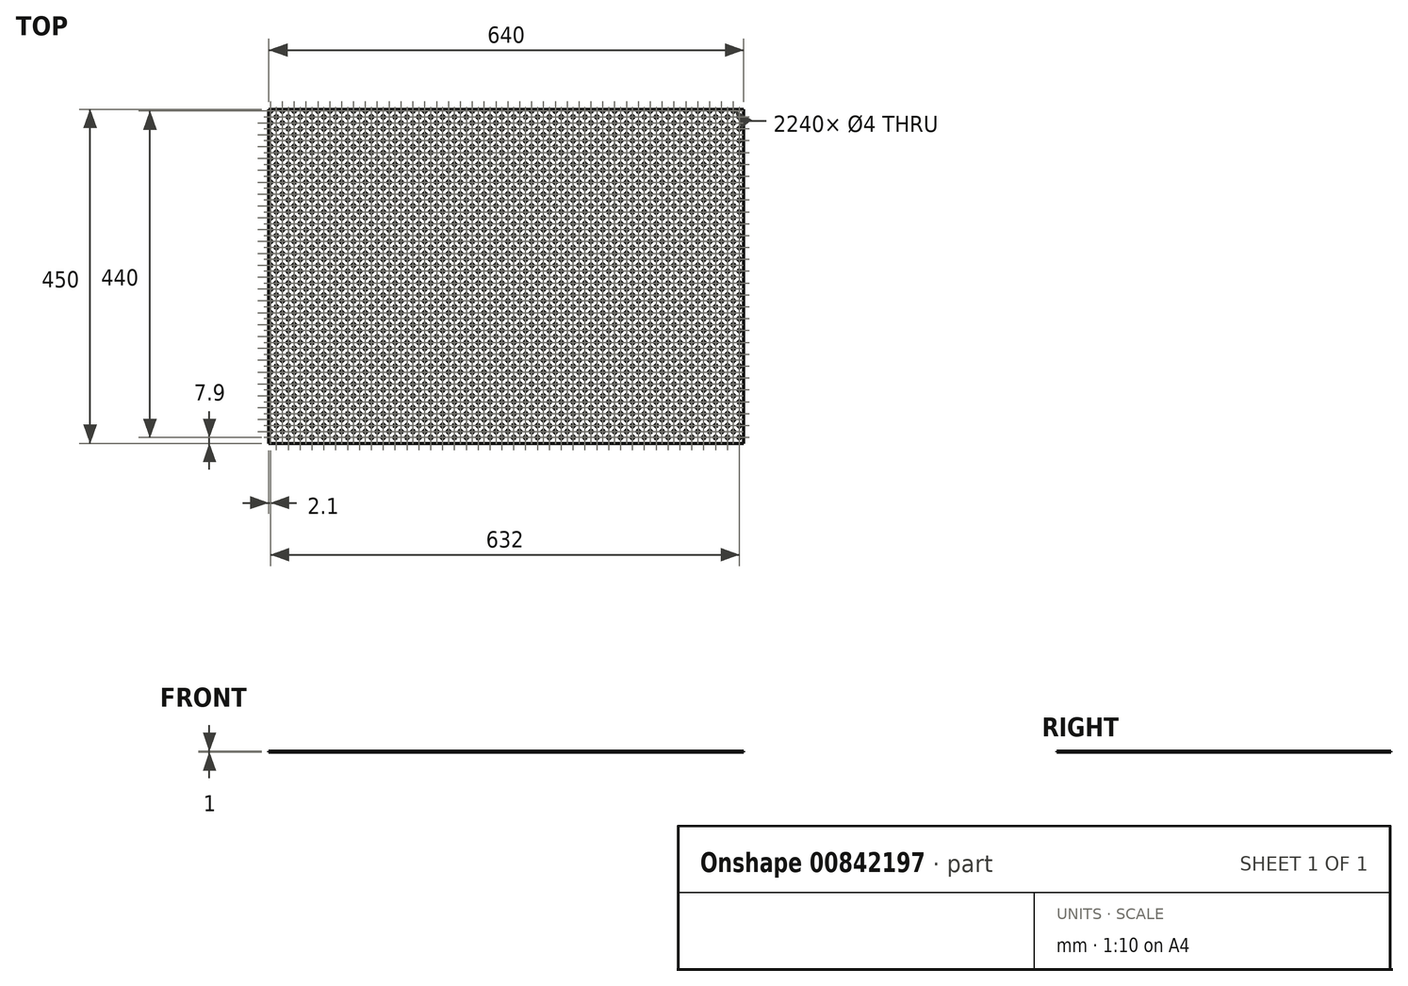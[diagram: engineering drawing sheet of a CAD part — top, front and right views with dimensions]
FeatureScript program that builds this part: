
annotation { "Feature Type Name" : "Feature", "Feature Type Description" : "" }
export const myFeature = defineFeature(function(context is Context, id is Id, definition is map)
    precondition{}
    {
        {
            var Q0;
            Q0=qCreatedBy(makeId("Top.planeOp"),FACE);
            var sketch = newSketch(context, id + "F0", { "sketchPlane" : qUnion([Q0])});
            skLineSegment(sketch, "E0.bottom", {"start": v(-115.44, 0) * mm, "end": v(524.56, 0) * mm});
            skLineSegment(sketch, "E0.top", {"start": v(-115.44, -450) * mm, "end": v(524.56, -450) * mm});
            skLineSegment(sketch, "E0.left", {"start": v(-115.44, 0) * mm, "end": v(-115.44, -450) * mm});
            skLineSegment(sketch, "E0.right", {"start": v(524.56, 0) * mm, "end": v(524.56, -450) * mm});
            skCircle(sketch, "E1", {"center": v(-113.34, -2.1) * mm, "radius": 2 * mm});
            skCircle(sketch, "E2.0.1.0", {"center": v(-113.34, -18.1) * mm, "radius": 2 * mm});
            skCircle(sketch, "E2.0.2.0", {"center": v(-113.34, -34.1) * mm, "radius": 2 * mm});
            skCircle(sketch, "E2.0.3.0", {"center": v(-113.34, -50.1) * mm, "radius": 2 * mm});
            skCircle(sketch, "E2.0.4.0", {"center": v(-113.34, -66.1) * mm, "radius": 2 * mm});
            skCircle(sketch, "E2.0.5.0", {"center": v(-113.34, -82.1) * mm, "radius": 2 * mm});
            skCircle(sketch, "E2.0.6.0", {"center": v(-113.34, -98.1) * mm, "radius": 2 * mm});
            skCircle(sketch, "E2.0.7.0", {"center": v(-113.34, -114.1) * mm, "radius": 2 * mm});
            skCircle(sketch, "E2.0.8.0", {"center": v(-113.34, -130.1) * mm, "radius": 2 * mm});
            skCircle(sketch, "E2.0.9.0", {"center": v(-113.34, -146.1) * mm, "radius": 2 * mm});
            skCircle(sketch, "E2.0.10.0", {"center": v(-113.34, -162.1) * mm, "radius": 2 * mm});
            skCircle(sketch, "E2.0.11.0", {"center": v(-113.34, -178.1) * mm, "radius": 2 * mm});
            skCircle(sketch, "E2.0.12.0", {"center": v(-113.34, -194.1) * mm, "radius": 2 * mm});
            skCircle(sketch, "E2.0.13.0", {"center": v(-113.34, -210.1) * mm, "radius": 2 * mm});
            skCircle(sketch, "E2.0.14.0", {"center": v(-113.34, -226.1) * mm, "radius": 2 * mm});
            skCircle(sketch, "E2.0.15.0", {"center": v(-113.34, -242.1) * mm, "radius": 2 * mm});
            skCircle(sketch, "E2.0.16.0", {"center": v(-113.34, -258.1) * mm, "radius": 2 * mm});
            skCircle(sketch, "E2.0.17.0", {"center": v(-113.34, -274.1) * mm, "radius": 2 * mm});
            skCircle(sketch, "E2.0.18.0", {"center": v(-113.34, -290.1) * mm, "radius": 2 * mm});
            skCircle(sketch, "E2.0.19.0", {"center": v(-113.34, -306.1) * mm, "radius": 2 * mm});
            skCircle(sketch, "E2.0.20.0", {"center": v(-113.34, -322.1) * mm, "radius": 2 * mm});
            skCircle(sketch, "E2.0.21.0", {"center": v(-113.34, -338.1) * mm, "radius": 2 * mm});
            skCircle(sketch, "E2.0.22.0", {"center": v(-113.34, -354.1) * mm, "radius": 2 * mm});
            skCircle(sketch, "E2.0.23.0", {"center": v(-113.34, -370.1) * mm, "radius": 2 * mm});
            skCircle(sketch, "E2.0.24.0", {"center": v(-113.34, -386.1) * mm, "radius": 2 * mm});
            skCircle(sketch, "E2.0.25.0", {"center": v(-113.34, -402.1) * mm, "radius": 2 * mm});
            skCircle(sketch, "E2.0.26.0", {"center": v(-113.34, -418.1) * mm, "radius": 2 * mm});
            skCircle(sketch, "E2.0.27.0", {"center": v(-113.34, -434.1) * mm, "radius": 2 * mm});
            skCircle(sketch, "E2.1.0.0", {"center": v(-97.34, -2.1) * mm, "radius": 2 * mm});
            skCircle(sketch, "E2.1.1.0", {"center": v(-97.34, -18.1) * mm, "radius": 2 * mm});
            skCircle(sketch, "E2.1.2.0", {"center": v(-97.34, -34.1) * mm, "radius": 2 * mm});
            skCircle(sketch, "E2.1.3.0", {"center": v(-97.34, -50.1) * mm, "radius": 2 * mm});
            skCircle(sketch, "E2.1.4.0", {"center": v(-97.34, -66.1) * mm, "radius": 2 * mm});
            skCircle(sketch, "E2.1.5.0", {"center": v(-97.34, -82.1) * mm, "radius": 2 * mm});
            skCircle(sketch, "E2.1.6.0", {"center": v(-97.34, -98.1) * mm, "radius": 2 * mm});
            skCircle(sketch, "E2.1.7.0", {"center": v(-97.34, -114.1) * mm, "radius": 2 * mm});
            skCircle(sketch, "E2.1.8.0", {"center": v(-97.34, -130.1) * mm, "radius": 2 * mm});
            skCircle(sketch, "E2.1.9.0", {"center": v(-97.34, -146.1) * mm, "radius": 2 * mm});
            skCircle(sketch, "E2.1.10.0", {"center": v(-97.34, -162.1) * mm, "radius": 2 * mm});
            skCircle(sketch, "E2.1.11.0", {"center": v(-97.34, -178.1) * mm, "radius": 2 * mm});
            skCircle(sketch, "E2.1.12.0", {"center": v(-97.34, -194.1) * mm, "radius": 2 * mm});
            skCircle(sketch, "E2.1.13.0", {"center": v(-97.34, -210.1) * mm, "radius": 2 * mm});
            skCircle(sketch, "E2.1.14.0", {"center": v(-97.34, -226.1) * mm, "radius": 2 * mm});
            skCircle(sketch, "E2.1.15.0", {"center": v(-97.34, -242.1) * mm, "radius": 2 * mm});
            skCircle(sketch, "E2.1.16.0", {"center": v(-97.34, -258.1) * mm, "radius": 2 * mm});
            skCircle(sketch, "E2.1.17.0", {"center": v(-97.34, -274.1) * mm, "radius": 2 * mm});
            skCircle(sketch, "E2.1.18.0", {"center": v(-97.34, -290.1) * mm, "radius": 2 * mm});
            skCircle(sketch, "E2.1.19.0", {"center": v(-97.34, -306.1) * mm, "radius": 2 * mm});
            skCircle(sketch, "E2.1.20.0", {"center": v(-97.34, -322.1) * mm, "radius": 2 * mm});
            skCircle(sketch, "E2.1.21.0", {"center": v(-97.34, -338.1) * mm, "radius": 2 * mm});
            skCircle(sketch, "E2.1.22.0", {"center": v(-97.34, -354.1) * mm, "radius": 2 * mm});
            skCircle(sketch, "E2.1.23.0", {"center": v(-97.34, -370.1) * mm, "radius": 2 * mm});
            skCircle(sketch, "E2.1.24.0", {"center": v(-97.34, -386.1) * mm, "radius": 2 * mm});
            skCircle(sketch, "E2.1.25.0", {"center": v(-97.34, -402.1) * mm, "radius": 2 * mm});
            skCircle(sketch, "E2.1.26.0", {"center": v(-97.34, -418.1) * mm, "radius": 2 * mm});
            skCircle(sketch, "E2.1.27.0", {"center": v(-97.34, -434.1) * mm, "radius": 2 * mm});
            skCircle(sketch, "E2.2.0.0", {"center": v(-81.34, -2.1) * mm, "radius": 2 * mm});
            skCircle(sketch, "E2.2.1.0", {"center": v(-81.34, -18.1) * mm, "radius": 2 * mm});
            skCircle(sketch, "E2.2.2.0", {"center": v(-81.34, -34.1) * mm, "radius": 2 * mm});
            skCircle(sketch, "E2.2.3.0", {"center": v(-81.34, -50.1) * mm, "radius": 2 * mm});
            skCircle(sketch, "E2.2.4.0", {"center": v(-81.34, -66.1) * mm, "radius": 2 * mm});
            skCircle(sketch, "E2.2.5.0", {"center": v(-81.34, -82.1) * mm, "radius": 2 * mm});
            skCircle(sketch, "E2.2.6.0", {"center": v(-81.34, -98.1) * mm, "radius": 2 * mm});
            skCircle(sketch, "E2.2.7.0", {"center": v(-81.34, -114.1) * mm, "radius": 2 * mm});
            skCircle(sketch, "E2.2.8.0", {"center": v(-81.34, -130.1) * mm, "radius": 2 * mm});
            skCircle(sketch, "E2.2.9.0", {"center": v(-81.34, -146.1) * mm, "radius": 2 * mm});
            skCircle(sketch, "E2.2.10.0", {"center": v(-81.34, -162.1) * mm, "radius": 2 * mm});
            skCircle(sketch, "E2.2.11.0", {"center": v(-81.34, -178.1) * mm, "radius": 2 * mm});
            skCircle(sketch, "E2.2.12.0", {"center": v(-81.34, -194.1) * mm, "radius": 2 * mm});
            skCircle(sketch, "E2.2.13.0", {"center": v(-81.34, -210.1) * mm, "radius": 2 * mm});
            skCircle(sketch, "E2.2.14.0", {"center": v(-81.34, -226.1) * mm, "radius": 2 * mm});
            skCircle(sketch, "E2.2.15.0", {"center": v(-81.34, -242.1) * mm, "radius": 2 * mm});
            skCircle(sketch, "E2.2.16.0", {"center": v(-81.34, -258.1) * mm, "radius": 2 * mm});
            skCircle(sketch, "E2.2.17.0", {"center": v(-81.34, -274.1) * mm, "radius": 2 * mm});
            skCircle(sketch, "E2.2.18.0", {"center": v(-81.34, -290.1) * mm, "radius": 2 * mm});
            skCircle(sketch, "E2.2.19.0", {"center": v(-81.34, -306.1) * mm, "radius": 2 * mm});
            skCircle(sketch, "E2.2.20.0", {"center": v(-81.34, -322.1) * mm, "radius": 2 * mm});
            skCircle(sketch, "E2.2.21.0", {"center": v(-81.34, -338.1) * mm, "radius": 2 * mm});
            skCircle(sketch, "E2.2.22.0", {"center": v(-81.34, -354.1) * mm, "radius": 2 * mm});
            skCircle(sketch, "E2.2.23.0", {"center": v(-81.34, -370.1) * mm, "radius": 2 * mm});
            skCircle(sketch, "E2.2.24.0", {"center": v(-81.34, -386.1) * mm, "radius": 2 * mm});
            skCircle(sketch, "E2.2.25.0", {"center": v(-81.34, -402.1) * mm, "radius": 2 * mm});
            skCircle(sketch, "E2.2.26.0", {"center": v(-81.34, -418.1) * mm, "radius": 2 * mm});
            skCircle(sketch, "E2.2.27.0", {"center": v(-81.34, -434.1) * mm, "radius": 2 * mm});
            skCircle(sketch, "E2.3.0.0", {"center": v(-65.34, -2.1) * mm, "radius": 2 * mm});
            skCircle(sketch, "E2.3.1.0", {"center": v(-65.34, -18.1) * mm, "radius": 2 * mm});
            skCircle(sketch, "E2.3.2.0", {"center": v(-65.34, -34.1) * mm, "radius": 2 * mm});
            skCircle(sketch, "E2.3.3.0", {"center": v(-65.34, -50.1) * mm, "radius": 2 * mm});
            skCircle(sketch, "E2.3.4.0", {"center": v(-65.34, -66.1) * mm, "radius": 2 * mm});
            skCircle(sketch, "E2.3.5.0", {"center": v(-65.34, -82.1) * mm, "radius": 2 * mm});
            skCircle(sketch, "E2.3.6.0", {"center": v(-65.34, -98.1) * mm, "radius": 2 * mm});
            skCircle(sketch, "E2.3.7.0", {"center": v(-65.34, -114.1) * mm, "radius": 2 * mm});
            skCircle(sketch, "E2.3.8.0", {"center": v(-65.34, -130.1) * mm, "radius": 2 * mm});
            skCircle(sketch, "E2.3.9.0", {"center": v(-65.34, -146.1) * mm, "radius": 2 * mm});
            skCircle(sketch, "E2.3.10.0", {"center": v(-65.34, -162.1) * mm, "radius": 2 * mm});
            skCircle(sketch, "E2.3.11.0", {"center": v(-65.34, -178.1) * mm, "radius": 2 * mm});
            skCircle(sketch, "E2.3.12.0", {"center": v(-65.34, -194.1) * mm, "radius": 2 * mm});
            skCircle(sketch, "E2.3.13.0", {"center": v(-65.34, -210.1) * mm, "radius": 2 * mm});
            skCircle(sketch, "E2.3.14.0", {"center": v(-65.34, -226.1) * mm, "radius": 2 * mm});
            skCircle(sketch, "E2.3.15.0", {"center": v(-65.34, -242.1) * mm, "radius": 2 * mm});
            skCircle(sketch, "E2.3.16.0", {"center": v(-65.34, -258.1) * mm, "radius": 2 * mm});
            skCircle(sketch, "E2.3.17.0", {"center": v(-65.34, -274.1) * mm, "radius": 2 * mm});
            skCircle(sketch, "E2.3.18.0", {"center": v(-65.34, -290.1) * mm, "radius": 2 * mm});
            skCircle(sketch, "E2.3.19.0", {"center": v(-65.34, -306.1) * mm, "radius": 2 * mm});
            skCircle(sketch, "E2.3.20.0", {"center": v(-65.34, -322.1) * mm, "radius": 2 * mm});
            skCircle(sketch, "E2.3.21.0", {"center": v(-65.34, -338.1) * mm, "radius": 2 * mm});
            skCircle(sketch, "E2.3.22.0", {"center": v(-65.34, -354.1) * mm, "radius": 2 * mm});
            skCircle(sketch, "E2.3.23.0", {"center": v(-65.34, -370.1) * mm, "radius": 2 * mm});
            skCircle(sketch, "E2.3.24.0", {"center": v(-65.34, -386.1) * mm, "radius": 2 * mm});
            skCircle(sketch, "E2.3.25.0", {"center": v(-65.34, -402.1) * mm, "radius": 2 * mm});
            skCircle(sketch, "E2.3.26.0", {"center": v(-65.34, -418.1) * mm, "radius": 2 * mm});
            skCircle(sketch, "E2.3.27.0", {"center": v(-65.34, -434.1) * mm, "radius": 2 * mm});
            skCircle(sketch, "E2.4.0.0", {"center": v(-49.34, -2.1) * mm, "radius": 2 * mm});
            skCircle(sketch, "E2.4.1.0", {"center": v(-49.34, -18.1) * mm, "radius": 2 * mm});
            skCircle(sketch, "E2.4.2.0", {"center": v(-49.34, -34.1) * mm, "radius": 2 * mm});
            skCircle(sketch, "E2.4.3.0", {"center": v(-49.34, -50.1) * mm, "radius": 2 * mm});
            skCircle(sketch, "E2.4.4.0", {"center": v(-49.34, -66.1) * mm, "radius": 2 * mm});
            skCircle(sketch, "E2.4.5.0", {"center": v(-49.34, -82.1) * mm, "radius": 2 * mm});
            skCircle(sketch, "E2.4.6.0", {"center": v(-49.34, -98.1) * mm, "radius": 2 * mm});
            skCircle(sketch, "E2.4.7.0", {"center": v(-49.34, -114.1) * mm, "radius": 2 * mm});
            skCircle(sketch, "E2.4.8.0", {"center": v(-49.34, -130.1) * mm, "radius": 2 * mm});
            skCircle(sketch, "E2.4.9.0", {"center": v(-49.34, -146.1) * mm, "radius": 2 * mm});
            skCircle(sketch, "E2.4.10.0", {"center": v(-49.34, -162.1) * mm, "radius": 2 * mm});
            skCircle(sketch, "E2.4.11.0", {"center": v(-49.34, -178.1) * mm, "radius": 2 * mm});
            skCircle(sketch, "E2.4.12.0", {"center": v(-49.34, -194.1) * mm, "radius": 2 * mm});
            skCircle(sketch, "E2.4.13.0", {"center": v(-49.34, -210.1) * mm, "radius": 2 * mm});
            skCircle(sketch, "E2.4.14.0", {"center": v(-49.34, -226.1) * mm, "radius": 2 * mm});
            skCircle(sketch, "E2.4.15.0", {"center": v(-49.34, -242.1) * mm, "radius": 2 * mm});
            skCircle(sketch, "E2.4.16.0", {"center": v(-49.34, -258.1) * mm, "radius": 2 * mm});
            skCircle(sketch, "E2.4.17.0", {"center": v(-49.34, -274.1) * mm, "radius": 2 * mm});
            skCircle(sketch, "E2.4.18.0", {"center": v(-49.34, -290.1) * mm, "radius": 2 * mm});
            skCircle(sketch, "E2.4.19.0", {"center": v(-49.34, -306.1) * mm, "radius": 2 * mm});
            skCircle(sketch, "E2.4.20.0", {"center": v(-49.34, -322.1) * mm, "radius": 2 * mm});
            skCircle(sketch, "E2.4.21.0", {"center": v(-49.34, -338.1) * mm, "radius": 2 * mm});
            skCircle(sketch, "E2.4.22.0", {"center": v(-49.34, -354.1) * mm, "radius": 2 * mm});
            skCircle(sketch, "E2.4.23.0", {"center": v(-49.34, -370.1) * mm, "radius": 2 * mm});
            skCircle(sketch, "E2.4.24.0", {"center": v(-49.34, -386.1) * mm, "radius": 2 * mm});
            skCircle(sketch, "E2.4.25.0", {"center": v(-49.34, -402.1) * mm, "radius": 2 * mm});
            skCircle(sketch, "E2.4.26.0", {"center": v(-49.34, -418.1) * mm, "radius": 2 * mm});
            skCircle(sketch, "E2.4.27.0", {"center": v(-49.34, -434.1) * mm, "radius": 2 * mm});
            skCircle(sketch, "E2.5.0.0", {"center": v(-33.34, -2.1) * mm, "radius": 2 * mm});
            skCircle(sketch, "E2.5.1.0", {"center": v(-33.34, -18.1) * mm, "radius": 2 * mm});
            skCircle(sketch, "E2.5.2.0", {"center": v(-33.34, -34.1) * mm, "radius": 2 * mm});
            skCircle(sketch, "E2.5.3.0", {"center": v(-33.34, -50.1) * mm, "radius": 2 * mm});
            skCircle(sketch, "E2.5.4.0", {"center": v(-33.34, -66.1) * mm, "radius": 2 * mm});
            skCircle(sketch, "E2.5.5.0", {"center": v(-33.34, -82.1) * mm, "radius": 2 * mm});
            skCircle(sketch, "E2.5.6.0", {"center": v(-33.34, -98.1) * mm, "radius": 2 * mm});
            skCircle(sketch, "E2.5.7.0", {"center": v(-33.34, -114.1) * mm, "radius": 2 * mm});
            skCircle(sketch, "E2.5.8.0", {"center": v(-33.34, -130.1) * mm, "radius": 2 * mm});
            skCircle(sketch, "E2.5.9.0", {"center": v(-33.34, -146.1) * mm, "radius": 2 * mm});
            skCircle(sketch, "E2.5.10.0", {"center": v(-33.34, -162.1) * mm, "radius": 2 * mm});
            skCircle(sketch, "E2.5.11.0", {"center": v(-33.34, -178.1) * mm, "radius": 2 * mm});
            skCircle(sketch, "E2.5.12.0", {"center": v(-33.34, -194.1) * mm, "radius": 2 * mm});
            skCircle(sketch, "E2.5.13.0", {"center": v(-33.34, -210.1) * mm, "radius": 2 * mm});
            skCircle(sketch, "E2.5.14.0", {"center": v(-33.34, -226.1) * mm, "radius": 2 * mm});
            skCircle(sketch, "E2.5.15.0", {"center": v(-33.34, -242.1) * mm, "radius": 2 * mm});
            skCircle(sketch, "E2.5.16.0", {"center": v(-33.34, -258.1) * mm, "radius": 2 * mm});
            skCircle(sketch, "E2.5.17.0", {"center": v(-33.34, -274.1) * mm, "radius": 2 * mm});
            skCircle(sketch, "E2.5.18.0", {"center": v(-33.34, -290.1) * mm, "radius": 2 * mm});
            skCircle(sketch, "E2.5.19.0", {"center": v(-33.34, -306.1) * mm, "radius": 2 * mm});
            skCircle(sketch, "E2.5.20.0", {"center": v(-33.34, -322.1) * mm, "radius": 2 * mm});
            skCircle(sketch, "E2.5.21.0", {"center": v(-33.34, -338.1) * mm, "radius": 2 * mm});
            skCircle(sketch, "E2.5.22.0", {"center": v(-33.34, -354.1) * mm, "radius": 2 * mm});
            skCircle(sketch, "E2.5.23.0", {"center": v(-33.34, -370.1) * mm, "radius": 2 * mm});
            skCircle(sketch, "E2.5.24.0", {"center": v(-33.34, -386.1) * mm, "radius": 2 * mm});
            skCircle(sketch, "E2.5.25.0", {"center": v(-33.34, -402.1) * mm, "radius": 2 * mm});
            skCircle(sketch, "E2.5.26.0", {"center": v(-33.34, -418.1) * mm, "radius": 2 * mm});
            skCircle(sketch, "E2.5.27.0", {"center": v(-33.34, -434.1) * mm, "radius": 2 * mm});
            skCircle(sketch, "E2.6.0.0", {"center": v(-17.34, -2.1) * mm, "radius": 2 * mm});
            skCircle(sketch, "E2.6.1.0", {"center": v(-17.34, -18.1) * mm, "radius": 2 * mm});
            skCircle(sketch, "E2.6.2.0", {"center": v(-17.34, -34.1) * mm, "radius": 2 * mm});
            skCircle(sketch, "E2.6.3.0", {"center": v(-17.34, -50.1) * mm, "radius": 2 * mm});
            skCircle(sketch, "E2.6.4.0", {"center": v(-17.34, -66.1) * mm, "radius": 2 * mm});
            skCircle(sketch, "E2.6.5.0", {"center": v(-17.34, -82.1) * mm, "radius": 2 * mm});
            skCircle(sketch, "E2.6.6.0", {"center": v(-17.34, -98.1) * mm, "radius": 2 * mm});
            skCircle(sketch, "E2.6.7.0", {"center": v(-17.34, -114.1) * mm, "radius": 2 * mm});
            skCircle(sketch, "E2.6.8.0", {"center": v(-17.34, -130.1) * mm, "radius": 2 * mm});
            skCircle(sketch, "E2.6.9.0", {"center": v(-17.34, -146.1) * mm, "radius": 2 * mm});
            skCircle(sketch, "E2.6.10.0", {"center": v(-17.34, -162.1) * mm, "radius": 2 * mm});
            skCircle(sketch, "E2.6.11.0", {"center": v(-17.34, -178.1) * mm, "radius": 2 * mm});
            skCircle(sketch, "E2.6.12.0", {"center": v(-17.34, -194.1) * mm, "radius": 2 * mm});
            skCircle(sketch, "E2.6.13.0", {"center": v(-17.34, -210.1) * mm, "radius": 2 * mm});
            skCircle(sketch, "E2.6.14.0", {"center": v(-17.34, -226.1) * mm, "radius": 2 * mm});
            skCircle(sketch, "E2.6.15.0", {"center": v(-17.34, -242.1) * mm, "radius": 2 * mm});
            skCircle(sketch, "E2.6.16.0", {"center": v(-17.34, -258.1) * mm, "radius": 2 * mm});
            skCircle(sketch, "E2.6.17.0", {"center": v(-17.34, -274.1) * mm, "radius": 2 * mm});
            skCircle(sketch, "E2.6.18.0", {"center": v(-17.34, -290.1) * mm, "radius": 2 * mm});
            skCircle(sketch, "E2.6.19.0", {"center": v(-17.34, -306.1) * mm, "radius": 2 * mm});
            skCircle(sketch, "E2.6.20.0", {"center": v(-17.34, -322.1) * mm, "radius": 2 * mm});
            skCircle(sketch, "E2.6.21.0", {"center": v(-17.34, -338.1) * mm, "radius": 2 * mm});
            skCircle(sketch, "E2.6.22.0", {"center": v(-17.34, -354.1) * mm, "radius": 2 * mm});
            skCircle(sketch, "E2.6.23.0", {"center": v(-17.34, -370.1) * mm, "radius": 2 * mm});
            skCircle(sketch, "E2.6.24.0", {"center": v(-17.34, -386.1) * mm, "radius": 2 * mm});
            skCircle(sketch, "E2.6.25.0", {"center": v(-17.34, -402.1) * mm, "radius": 2 * mm});
            skCircle(sketch, "E2.6.26.0", {"center": v(-17.34, -418.1) * mm, "radius": 2 * mm});
            skCircle(sketch, "E2.6.27.0", {"center": v(-17.34, -434.1) * mm, "radius": 2 * mm});
            skCircle(sketch, "E2.7.0.0", {"center": v(-1.34, -2.1) * mm, "radius": 2 * mm});
            skCircle(sketch, "E2.7.1.0", {"center": v(-1.34, -18.1) * mm, "radius": 2 * mm});
            skCircle(sketch, "E2.7.2.0", {"center": v(-1.34, -34.1) * mm, "radius": 2 * mm});
            skCircle(sketch, "E2.7.3.0", {"center": v(-1.34, -50.1) * mm, "radius": 2 * mm});
            skCircle(sketch, "E2.7.4.0", {"center": v(-1.34, -66.1) * mm, "radius": 2 * mm});
            skCircle(sketch, "E2.7.5.0", {"center": v(-1.34, -82.1) * mm, "radius": 2 * mm});
            skCircle(sketch, "E2.7.6.0", {"center": v(-1.34, -98.1) * mm, "radius": 2 * mm});
            skCircle(sketch, "E2.7.7.0", {"center": v(-1.34, -114.1) * mm, "radius": 2 * mm});
            skCircle(sketch, "E2.7.8.0", {"center": v(-1.34, -130.1) * mm, "radius": 2 * mm});
            skCircle(sketch, "E2.7.9.0", {"center": v(-1.34, -146.1) * mm, "radius": 2 * mm});
            skCircle(sketch, "E2.7.10.0", {"center": v(-1.34, -162.1) * mm, "radius": 2 * mm});
            skCircle(sketch, "E2.7.11.0", {"center": v(-1.34, -178.1) * mm, "radius": 2 * mm});
            skCircle(sketch, "E2.7.12.0", {"center": v(-1.34, -194.1) * mm, "radius": 2 * mm});
            skCircle(sketch, "E2.7.13.0", {"center": v(-1.34, -210.1) * mm, "radius": 2 * mm});
            skCircle(sketch, "E2.7.14.0", {"center": v(-1.34, -226.1) * mm, "radius": 2 * mm});
            skCircle(sketch, "E2.7.15.0", {"center": v(-1.34, -242.1) * mm, "radius": 2 * mm});
            skCircle(sketch, "E2.7.16.0", {"center": v(-1.34, -258.1) * mm, "radius": 2 * mm});
            skCircle(sketch, "E2.7.17.0", {"center": v(-1.34, -274.1) * mm, "radius": 2 * mm});
            skCircle(sketch, "E2.7.18.0", {"center": v(-1.34, -290.1) * mm, "radius": 2 * mm});
            skCircle(sketch, "E2.7.19.0", {"center": v(-1.34, -306.1) * mm, "radius": 2 * mm});
            skCircle(sketch, "E2.7.20.0", {"center": v(-1.34, -322.1) * mm, "radius": 2 * mm});
            skCircle(sketch, "E2.7.21.0", {"center": v(-1.34, -338.1) * mm, "radius": 2 * mm});
            skCircle(sketch, "E2.7.22.0", {"center": v(-1.34, -354.1) * mm, "radius": 2 * mm});
            skCircle(sketch, "E2.7.23.0", {"center": v(-1.34, -370.1) * mm, "radius": 2 * mm});
            skCircle(sketch, "E2.7.24.0", {"center": v(-1.34, -386.1) * mm, "radius": 2 * mm});
            skCircle(sketch, "E2.7.25.0", {"center": v(-1.34, -402.1) * mm, "radius": 2 * mm});
            skCircle(sketch, "E2.7.26.0", {"center": v(-1.34, -418.1) * mm, "radius": 2 * mm});
            skCircle(sketch, "E2.7.27.0", {"center": v(-1.34, -434.1) * mm, "radius": 2 * mm});
            skCircle(sketch, "E2.8.0.0", {"center": v(14.66, -2.1) * mm, "radius": 2 * mm});
            skCircle(sketch, "E2.8.1.0", {"center": v(14.66, -18.1) * mm, "radius": 2 * mm});
            skCircle(sketch, "E2.8.2.0", {"center": v(14.66, -34.1) * mm, "radius": 2 * mm});
            skCircle(sketch, "E2.8.3.0", {"center": v(14.66, -50.1) * mm, "radius": 2 * mm});
            skCircle(sketch, "E2.8.4.0", {"center": v(14.66, -66.1) * mm, "radius": 2 * mm});
            skCircle(sketch, "E2.8.5.0", {"center": v(14.66, -82.1) * mm, "radius": 2 * mm});
            skCircle(sketch, "E2.8.6.0", {"center": v(14.66, -98.1) * mm, "radius": 2 * mm});
            skCircle(sketch, "E2.8.7.0", {"center": v(14.66, -114.1) * mm, "radius": 2 * mm});
            skCircle(sketch, "E2.8.8.0", {"center": v(14.66, -130.1) * mm, "radius": 2 * mm});
            skCircle(sketch, "E2.8.9.0", {"center": v(14.66, -146.1) * mm, "radius": 2 * mm});
            skCircle(sketch, "E2.8.10.0", {"center": v(14.66, -162.1) * mm, "radius": 2 * mm});
            skCircle(sketch, "E2.8.11.0", {"center": v(14.66, -178.1) * mm, "radius": 2 * mm});
            skCircle(sketch, "E2.8.12.0", {"center": v(14.66, -194.1) * mm, "radius": 2 * mm});
            skCircle(sketch, "E2.8.13.0", {"center": v(14.66, -210.1) * mm, "radius": 2 * mm});
            skCircle(sketch, "E2.8.14.0", {"center": v(14.66, -226.1) * mm, "radius": 2 * mm});
            skCircle(sketch, "E2.8.15.0", {"center": v(14.66, -242.1) * mm, "radius": 2 * mm});
            skCircle(sketch, "E2.8.16.0", {"center": v(14.66, -258.1) * mm, "radius": 2 * mm});
            skCircle(sketch, "E2.8.17.0", {"center": v(14.66, -274.1) * mm, "radius": 2 * mm});
            skCircle(sketch, "E2.8.18.0", {"center": v(14.66, -290.1) * mm, "radius": 2 * mm});
            skCircle(sketch, "E2.8.19.0", {"center": v(14.66, -306.1) * mm, "radius": 2 * mm});
            skCircle(sketch, "E2.8.20.0", {"center": v(14.66, -322.1) * mm, "radius": 2 * mm});
            skCircle(sketch, "E2.8.21.0", {"center": v(14.66, -338.1) * mm, "radius": 2 * mm});
            skCircle(sketch, "E2.8.22.0", {"center": v(14.66, -354.1) * mm, "radius": 2 * mm});
            skCircle(sketch, "E2.8.23.0", {"center": v(14.66, -370.1) * mm, "radius": 2 * mm});
            skCircle(sketch, "E2.8.24.0", {"center": v(14.66, -386.1) * mm, "radius": 2 * mm});
            skCircle(sketch, "E2.8.25.0", {"center": v(14.66, -402.1) * mm, "radius": 2 * mm});
            skCircle(sketch, "E2.8.26.0", {"center": v(14.66, -418.1) * mm, "radius": 2 * mm});
            skCircle(sketch, "E2.8.27.0", {"center": v(14.66, -434.1) * mm, "radius": 2 * mm});
            skCircle(sketch, "E2.9.0.0", {"center": v(30.66, -2.1) * mm, "radius": 2 * mm});
            skCircle(sketch, "E2.9.1.0", {"center": v(30.66, -18.1) * mm, "radius": 2 * mm});
            skCircle(sketch, "E2.9.2.0", {"center": v(30.66, -34.1) * mm, "radius": 2 * mm});
            skCircle(sketch, "E2.9.3.0", {"center": v(30.66, -50.1) * mm, "radius": 2 * mm});
            skCircle(sketch, "E2.9.4.0", {"center": v(30.66, -66.1) * mm, "radius": 2 * mm});
            skCircle(sketch, "E2.9.5.0", {"center": v(30.66, -82.1) * mm, "radius": 2 * mm});
            skCircle(sketch, "E2.9.6.0", {"center": v(30.66, -98.1) * mm, "radius": 2 * mm});
            skCircle(sketch, "E2.9.7.0", {"center": v(30.66, -114.1) * mm, "radius": 2 * mm});
            skCircle(sketch, "E2.9.8.0", {"center": v(30.66, -130.1) * mm, "radius": 2 * mm});
            skCircle(sketch, "E2.9.9.0", {"center": v(30.66, -146.1) * mm, "radius": 2 * mm});
            skCircle(sketch, "E2.9.10.0", {"center": v(30.66, -162.1) * mm, "radius": 2 * mm});
            skCircle(sketch, "E2.9.11.0", {"center": v(30.66, -178.1) * mm, "radius": 2 * mm});
            skCircle(sketch, "E2.9.12.0", {"center": v(30.66, -194.1) * mm, "radius": 2 * mm});
            skCircle(sketch, "E2.9.13.0", {"center": v(30.66, -210.1) * mm, "radius": 2 * mm});
            skCircle(sketch, "E2.9.14.0", {"center": v(30.66, -226.1) * mm, "radius": 2 * mm});
            skCircle(sketch, "E2.9.15.0", {"center": v(30.66, -242.1) * mm, "radius": 2 * mm});
            skCircle(sketch, "E2.9.16.0", {"center": v(30.66, -258.1) * mm, "radius": 2 * mm});
            skCircle(sketch, "E2.9.17.0", {"center": v(30.66, -274.1) * mm, "radius": 2 * mm});
            skCircle(sketch, "E2.9.18.0", {"center": v(30.66, -290.1) * mm, "radius": 2 * mm});
            skCircle(sketch, "E2.9.19.0", {"center": v(30.66, -306.1) * mm, "radius": 2 * mm});
            skCircle(sketch, "E2.9.20.0", {"center": v(30.66, -322.1) * mm, "radius": 2 * mm});
            skCircle(sketch, "E2.9.21.0", {"center": v(30.66, -338.1) * mm, "radius": 2 * mm});
            skCircle(sketch, "E2.9.22.0", {"center": v(30.66, -354.1) * mm, "radius": 2 * mm});
            skCircle(sketch, "E2.9.23.0", {"center": v(30.66, -370.1) * mm, "radius": 2 * mm});
            skCircle(sketch, "E2.9.24.0", {"center": v(30.66, -386.1) * mm, "radius": 2 * mm});
            skCircle(sketch, "E2.9.25.0", {"center": v(30.66, -402.1) * mm, "radius": 2 * mm});
            skCircle(sketch, "E2.9.26.0", {"center": v(30.66, -418.1) * mm, "radius": 2 * mm});
            skCircle(sketch, "E2.9.27.0", {"center": v(30.66, -434.1) * mm, "radius": 2 * mm});
            skCircle(sketch, "E2.10.0.0", {"center": v(46.66, -2.1) * mm, "radius": 2 * mm});
            skCircle(sketch, "E2.10.1.0", {"center": v(46.66, -18.1) * mm, "radius": 2 * mm});
            skCircle(sketch, "E2.10.2.0", {"center": v(46.66, -34.1) * mm, "radius": 2 * mm});
            skCircle(sketch, "E2.10.3.0", {"center": v(46.66, -50.1) * mm, "radius": 2 * mm});
            skCircle(sketch, "E2.10.4.0", {"center": v(46.66, -66.1) * mm, "radius": 2 * mm});
            skCircle(sketch, "E2.10.5.0", {"center": v(46.66, -82.1) * mm, "radius": 2 * mm});
            skCircle(sketch, "E2.10.6.0", {"center": v(46.66, -98.1) * mm, "radius": 2 * mm});
            skCircle(sketch, "E2.10.7.0", {"center": v(46.66, -114.1) * mm, "radius": 2 * mm});
            skCircle(sketch, "E2.10.8.0", {"center": v(46.66, -130.1) * mm, "radius": 2 * mm});
            skCircle(sketch, "E2.10.9.0", {"center": v(46.66, -146.1) * mm, "radius": 2 * mm});
            skCircle(sketch, "E2.10.10.0", {"center": v(46.66, -162.1) * mm, "radius": 2 * mm});
            skCircle(sketch, "E2.10.11.0", {"center": v(46.66, -178.1) * mm, "radius": 2 * mm});
            skCircle(sketch, "E2.10.12.0", {"center": v(46.66, -194.1) * mm, "radius": 2 * mm});
            skCircle(sketch, "E2.10.13.0", {"center": v(46.66, -210.1) * mm, "radius": 2 * mm});
            skCircle(sketch, "E2.10.14.0", {"center": v(46.66, -226.1) * mm, "radius": 2 * mm});
            skCircle(sketch, "E2.10.15.0", {"center": v(46.66, -242.1) * mm, "radius": 2 * mm});
            skCircle(sketch, "E2.10.16.0", {"center": v(46.66, -258.1) * mm, "radius": 2 * mm});
            skCircle(sketch, "E2.10.17.0", {"center": v(46.66, -274.1) * mm, "radius": 2 * mm});
            skCircle(sketch, "E2.10.18.0", {"center": v(46.66, -290.1) * mm, "radius": 2 * mm});
            skCircle(sketch, "E2.10.19.0", {"center": v(46.66, -306.1) * mm, "radius": 2 * mm});
            skCircle(sketch, "E2.10.20.0", {"center": v(46.66, -322.1) * mm, "radius": 2 * mm});
            skCircle(sketch, "E2.10.21.0", {"center": v(46.66, -338.1) * mm, "radius": 2 * mm});
            skCircle(sketch, "E2.10.22.0", {"center": v(46.66, -354.1) * mm, "radius": 2 * mm});
            skCircle(sketch, "E2.10.23.0", {"center": v(46.66, -370.1) * mm, "radius": 2 * mm});
            skCircle(sketch, "E2.10.24.0", {"center": v(46.66, -386.1) * mm, "radius": 2 * mm});
            skCircle(sketch, "E2.10.25.0", {"center": v(46.66, -402.1) * mm, "radius": 2 * mm});
            skCircle(sketch, "E2.10.26.0", {"center": v(46.66, -418.1) * mm, "radius": 2 * mm});
            skCircle(sketch, "E2.10.27.0", {"center": v(46.66, -434.1) * mm, "radius": 2 * mm});
            skCircle(sketch, "E2.11.0.0", {"center": v(62.66, -2.1) * mm, "radius": 2 * mm});
            skCircle(sketch, "E2.11.1.0", {"center": v(62.66, -18.1) * mm, "radius": 2 * mm});
            skCircle(sketch, "E2.11.2.0", {"center": v(62.66, -34.1) * mm, "radius": 2 * mm});
            skCircle(sketch, "E2.11.3.0", {"center": v(62.66, -50.1) * mm, "radius": 2 * mm});
            skCircle(sketch, "E2.11.4.0", {"center": v(62.66, -66.1) * mm, "radius": 2 * mm});
            skCircle(sketch, "E2.11.5.0", {"center": v(62.66, -82.1) * mm, "radius": 2 * mm});
            skCircle(sketch, "E2.11.6.0", {"center": v(62.66, -98.1) * mm, "radius": 2 * mm});
            skCircle(sketch, "E2.11.7.0", {"center": v(62.66, -114.1) * mm, "radius": 2 * mm});
            skCircle(sketch, "E2.11.8.0", {"center": v(62.66, -130.1) * mm, "radius": 2 * mm});
            skCircle(sketch, "E2.11.9.0", {"center": v(62.66, -146.1) * mm, "radius": 2 * mm});
            skCircle(sketch, "E2.11.10.0", {"center": v(62.66, -162.1) * mm, "radius": 2 * mm});
            skCircle(sketch, "E2.11.11.0", {"center": v(62.66, -178.1) * mm, "radius": 2 * mm});
            skCircle(sketch, "E2.11.12.0", {"center": v(62.66, -194.1) * mm, "radius": 2 * mm});
            skCircle(sketch, "E2.11.13.0", {"center": v(62.66, -210.1) * mm, "radius": 2 * mm});
            skCircle(sketch, "E2.11.14.0", {"center": v(62.66, -226.1) * mm, "radius": 2 * mm});
            skCircle(sketch, "E2.11.15.0", {"center": v(62.66, -242.1) * mm, "radius": 2 * mm});
            skCircle(sketch, "E2.11.16.0", {"center": v(62.66, -258.1) * mm, "radius": 2 * mm});
            skCircle(sketch, "E2.11.17.0", {"center": v(62.66, -274.1) * mm, "radius": 2 * mm});
            skCircle(sketch, "E2.11.18.0", {"center": v(62.66, -290.1) * mm, "radius": 2 * mm});
            skCircle(sketch, "E2.11.19.0", {"center": v(62.66, -306.1) * mm, "radius": 2 * mm});
            skCircle(sketch, "E2.11.20.0", {"center": v(62.66, -322.1) * mm, "radius": 2 * mm});
            skCircle(sketch, "E2.11.21.0", {"center": v(62.66, -338.1) * mm, "radius": 2 * mm});
            skCircle(sketch, "E2.11.22.0", {"center": v(62.66, -354.1) * mm, "radius": 2 * mm});
            skCircle(sketch, "E2.11.23.0", {"center": v(62.66, -370.1) * mm, "radius": 2 * mm});
            skCircle(sketch, "E2.11.24.0", {"center": v(62.66, -386.1) * mm, "radius": 2 * mm});
            skCircle(sketch, "E2.11.25.0", {"center": v(62.66, -402.1) * mm, "radius": 2 * mm});
            skCircle(sketch, "E2.11.26.0", {"center": v(62.66, -418.1) * mm, "radius": 2 * mm});
            skCircle(sketch, "E2.11.27.0", {"center": v(62.66, -434.1) * mm, "radius": 2 * mm});
            skCircle(sketch, "E2.12.0.0", {"center": v(78.66, -2.1) * mm, "radius": 2 * mm});
            skCircle(sketch, "E2.12.1.0", {"center": v(78.66, -18.1) * mm, "radius": 2 * mm});
            skCircle(sketch, "E2.12.2.0", {"center": v(78.66, -34.1) * mm, "radius": 2 * mm});
            skCircle(sketch, "E2.12.3.0", {"center": v(78.66, -50.1) * mm, "radius": 2 * mm});
            skCircle(sketch, "E2.12.4.0", {"center": v(78.66, -66.1) * mm, "radius": 2 * mm});
            skCircle(sketch, "E2.12.5.0", {"center": v(78.66, -82.1) * mm, "radius": 2 * mm});
            skCircle(sketch, "E2.12.6.0", {"center": v(78.66, -98.1) * mm, "radius": 2 * mm});
            skCircle(sketch, "E2.12.7.0", {"center": v(78.66, -114.1) * mm, "radius": 2 * mm});
            skCircle(sketch, "E2.12.8.0", {"center": v(78.66, -130.1) * mm, "radius": 2 * mm});
            skCircle(sketch, "E2.12.9.0", {"center": v(78.66, -146.1) * mm, "radius": 2 * mm});
            skCircle(sketch, "E2.12.10.0", {"center": v(78.66, -162.1) * mm, "radius": 2 * mm});
            skCircle(sketch, "E2.12.11.0", {"center": v(78.66, -178.1) * mm, "radius": 2 * mm});
            skCircle(sketch, "E2.12.12.0", {"center": v(78.66, -194.1) * mm, "radius": 2 * mm});
            skCircle(sketch, "E2.12.13.0", {"center": v(78.66, -210.1) * mm, "radius": 2 * mm});
            skCircle(sketch, "E2.12.14.0", {"center": v(78.66, -226.1) * mm, "radius": 2 * mm});
            skCircle(sketch, "E2.12.15.0", {"center": v(78.66, -242.1) * mm, "radius": 2 * mm});
            skCircle(sketch, "E2.12.16.0", {"center": v(78.66, -258.1) * mm, "radius": 2 * mm});
            skCircle(sketch, "E2.12.17.0", {"center": v(78.66, -274.1) * mm, "radius": 2 * mm});
            skCircle(sketch, "E2.12.18.0", {"center": v(78.66, -290.1) * mm, "radius": 2 * mm});
            skCircle(sketch, "E2.12.19.0", {"center": v(78.66, -306.1) * mm, "radius": 2 * mm});
            skCircle(sketch, "E2.12.20.0", {"center": v(78.66, -322.1) * mm, "radius": 2 * mm});
            skCircle(sketch, "E2.12.21.0", {"center": v(78.66, -338.1) * mm, "radius": 2 * mm});
            skCircle(sketch, "E2.12.22.0", {"center": v(78.66, -354.1) * mm, "radius": 2 * mm});
            skCircle(sketch, "E2.12.23.0", {"center": v(78.66, -370.1) * mm, "radius": 2 * mm});
            skCircle(sketch, "E2.12.24.0", {"center": v(78.66, -386.1) * mm, "radius": 2 * mm});
            skCircle(sketch, "E2.12.25.0", {"center": v(78.66, -402.1) * mm, "radius": 2 * mm});
            skCircle(sketch, "E2.12.26.0", {"center": v(78.66, -418.1) * mm, "radius": 2 * mm});
            skCircle(sketch, "E2.12.27.0", {"center": v(78.66, -434.1) * mm, "radius": 2 * mm});
            skCircle(sketch, "E2.13.0.0", {"center": v(94.66, -2.1) * mm, "radius": 2 * mm});
            skCircle(sketch, "E2.13.1.0", {"center": v(94.66, -18.1) * mm, "radius": 2 * mm});
            skCircle(sketch, "E2.13.2.0", {"center": v(94.66, -34.1) * mm, "radius": 2 * mm});
            skCircle(sketch, "E2.13.3.0", {"center": v(94.66, -50.1) * mm, "radius": 2 * mm});
            skCircle(sketch, "E2.13.4.0", {"center": v(94.66, -66.1) * mm, "radius": 2 * mm});
            skCircle(sketch, "E2.13.5.0", {"center": v(94.66, -82.1) * mm, "radius": 2 * mm});
            skCircle(sketch, "E2.13.6.0", {"center": v(94.66, -98.1) * mm, "radius": 2 * mm});
            skCircle(sketch, "E2.13.7.0", {"center": v(94.66, -114.1) * mm, "radius": 2 * mm});
            skCircle(sketch, "E2.13.8.0", {"center": v(94.66, -130.1) * mm, "radius": 2 * mm});
            skCircle(sketch, "E2.13.9.0", {"center": v(94.66, -146.1) * mm, "radius": 2 * mm});
            skCircle(sketch, "E2.13.10.0", {"center": v(94.66, -162.1) * mm, "radius": 2 * mm});
            skCircle(sketch, "E2.13.11.0", {"center": v(94.66, -178.1) * mm, "radius": 2 * mm});
            skCircle(sketch, "E2.13.12.0", {"center": v(94.66, -194.1) * mm, "radius": 2 * mm});
            skCircle(sketch, "E2.13.13.0", {"center": v(94.66, -210.1) * mm, "radius": 2 * mm});
            skCircle(sketch, "E2.13.14.0", {"center": v(94.66, -226.1) * mm, "radius": 2 * mm});
            skCircle(sketch, "E2.13.15.0", {"center": v(94.66, -242.1) * mm, "radius": 2 * mm});
            skCircle(sketch, "E2.13.16.0", {"center": v(94.66, -258.1) * mm, "radius": 2 * mm});
            skCircle(sketch, "E2.13.17.0", {"center": v(94.66, -274.1) * mm, "radius": 2 * mm});
            skCircle(sketch, "E2.13.18.0", {"center": v(94.66, -290.1) * mm, "radius": 2 * mm});
            skCircle(sketch, "E2.13.19.0", {"center": v(94.66, -306.1) * mm, "radius": 2 * mm});
            skCircle(sketch, "E2.13.20.0", {"center": v(94.66, -322.1) * mm, "radius": 2 * mm});
            skCircle(sketch, "E2.13.21.0", {"center": v(94.66, -338.1) * mm, "radius": 2 * mm});
            skCircle(sketch, "E2.13.22.0", {"center": v(94.66, -354.1) * mm, "radius": 2 * mm});
            skCircle(sketch, "E2.13.23.0", {"center": v(94.66, -370.1) * mm, "radius": 2 * mm});
            skCircle(sketch, "E2.13.24.0", {"center": v(94.66, -386.1) * mm, "radius": 2 * mm});
            skCircle(sketch, "E2.13.25.0", {"center": v(94.66, -402.1) * mm, "radius": 2 * mm});
            skCircle(sketch, "E2.13.26.0", {"center": v(94.66, -418.1) * mm, "radius": 2 * mm});
            skCircle(sketch, "E2.13.27.0", {"center": v(94.66, -434.1) * mm, "radius": 2 * mm});
            skCircle(sketch, "E2.14.0.0", {"center": v(110.66, -2.1) * mm, "radius": 2 * mm});
            skCircle(sketch, "E2.14.1.0", {"center": v(110.66, -18.1) * mm, "radius": 2 * mm});
            skCircle(sketch, "E2.14.2.0", {"center": v(110.66, -34.1) * mm, "radius": 2 * mm});
            skCircle(sketch, "E2.14.3.0", {"center": v(110.66, -50.1) * mm, "radius": 2 * mm});
            skCircle(sketch, "E2.14.4.0", {"center": v(110.66, -66.1) * mm, "radius": 2 * mm});
            skCircle(sketch, "E2.14.5.0", {"center": v(110.66, -82.1) * mm, "radius": 2 * mm});
            skCircle(sketch, "E2.14.6.0", {"center": v(110.66, -98.1) * mm, "radius": 2 * mm});
            skCircle(sketch, "E2.14.7.0", {"center": v(110.66, -114.1) * mm, "radius": 2 * mm});
            skCircle(sketch, "E2.14.8.0", {"center": v(110.66, -130.1) * mm, "radius": 2 * mm});
            skCircle(sketch, "E2.14.9.0", {"center": v(110.66, -146.1) * mm, "radius": 2 * mm});
            skCircle(sketch, "E2.14.10.0", {"center": v(110.66, -162.1) * mm, "radius": 2 * mm});
            skCircle(sketch, "E2.14.11.0", {"center": v(110.66, -178.1) * mm, "radius": 2 * mm});
            skCircle(sketch, "E2.14.12.0", {"center": v(110.66, -194.1) * mm, "radius": 2 * mm});
            skCircle(sketch, "E2.14.13.0", {"center": v(110.66, -210.1) * mm, "radius": 2 * mm});
            skCircle(sketch, "E2.14.14.0", {"center": v(110.66, -226.1) * mm, "radius": 2 * mm});
            skCircle(sketch, "E2.14.15.0", {"center": v(110.66, -242.1) * mm, "radius": 2 * mm});
            skCircle(sketch, "E2.14.16.0", {"center": v(110.66, -258.1) * mm, "radius": 2 * mm});
            skCircle(sketch, "E2.14.17.0", {"center": v(110.66, -274.1) * mm, "radius": 2 * mm});
            skCircle(sketch, "E2.14.18.0", {"center": v(110.66, -290.1) * mm, "radius": 2 * mm});
            skCircle(sketch, "E2.14.19.0", {"center": v(110.66, -306.1) * mm, "radius": 2 * mm});
            skCircle(sketch, "E2.14.20.0", {"center": v(110.66, -322.1) * mm, "radius": 2 * mm});
            skCircle(sketch, "E2.14.21.0", {"center": v(110.66, -338.1) * mm, "radius": 2 * mm});
            skCircle(sketch, "E2.14.22.0", {"center": v(110.66, -354.1) * mm, "radius": 2 * mm});
            skCircle(sketch, "E2.14.23.0", {"center": v(110.66, -370.1) * mm, "radius": 2 * mm});
            skCircle(sketch, "E2.14.24.0", {"center": v(110.66, -386.1) * mm, "radius": 2 * mm});
            skCircle(sketch, "E2.14.25.0", {"center": v(110.66, -402.1) * mm, "radius": 2 * mm});
            skCircle(sketch, "E2.14.26.0", {"center": v(110.66, -418.1) * mm, "radius": 2 * mm});
            skCircle(sketch, "E2.14.27.0", {"center": v(110.66, -434.1) * mm, "radius": 2 * mm});
            skCircle(sketch, "E2.15.0.0", {"center": v(126.66, -2.1) * mm, "radius": 2 * mm});
            skCircle(sketch, "E2.15.1.0", {"center": v(126.66, -18.1) * mm, "radius": 2 * mm});
            skCircle(sketch, "E2.15.2.0", {"center": v(126.66, -34.1) * mm, "radius": 2 * mm});
            skCircle(sketch, "E2.15.3.0", {"center": v(126.66, -50.1) * mm, "radius": 2 * mm});
            skCircle(sketch, "E2.15.4.0", {"center": v(126.66, -66.1) * mm, "radius": 2 * mm});
            skCircle(sketch, "E2.15.5.0", {"center": v(126.66, -82.1) * mm, "radius": 2 * mm});
            skCircle(sketch, "E2.15.6.0", {"center": v(126.66, -98.1) * mm, "radius": 2 * mm});
            skCircle(sketch, "E2.15.7.0", {"center": v(126.66, -114.1) * mm, "radius": 2 * mm});
            skCircle(sketch, "E2.15.8.0", {"center": v(126.66, -130.1) * mm, "radius": 2 * mm});
            skCircle(sketch, "E2.15.9.0", {"center": v(126.66, -146.1) * mm, "radius": 2 * mm});
            skCircle(sketch, "E2.15.10.0", {"center": v(126.66, -162.1) * mm, "radius": 2 * mm});
            skCircle(sketch, "E2.15.11.0", {"center": v(126.66, -178.1) * mm, "radius": 2 * mm});
            skCircle(sketch, "E2.15.12.0", {"center": v(126.66, -194.1) * mm, "radius": 2 * mm});
            skCircle(sketch, "E2.15.13.0", {"center": v(126.66, -210.1) * mm, "radius": 2 * mm});
            skCircle(sketch, "E2.15.14.0", {"center": v(126.66, -226.1) * mm, "radius": 2 * mm});
            skCircle(sketch, "E2.15.15.0", {"center": v(126.66, -242.1) * mm, "radius": 2 * mm});
            skCircle(sketch, "E2.15.16.0", {"center": v(126.66, -258.1) * mm, "radius": 2 * mm});
            skCircle(sketch, "E2.15.17.0", {"center": v(126.66, -274.1) * mm, "radius": 2 * mm});
            skCircle(sketch, "E2.15.18.0", {"center": v(126.66, -290.1) * mm, "radius": 2 * mm});
            skCircle(sketch, "E2.15.19.0", {"center": v(126.66, -306.1) * mm, "radius": 2 * mm});
            skCircle(sketch, "E2.15.20.0", {"center": v(126.66, -322.1) * mm, "radius": 2 * mm});
            skCircle(sketch, "E2.15.21.0", {"center": v(126.66, -338.1) * mm, "radius": 2 * mm});
            skCircle(sketch, "E2.15.22.0", {"center": v(126.66, -354.1) * mm, "radius": 2 * mm});
            skCircle(sketch, "E2.15.23.0", {"center": v(126.66, -370.1) * mm, "radius": 2 * mm});
            skCircle(sketch, "E2.15.24.0", {"center": v(126.66, -386.1) * mm, "radius": 2 * mm});
            skCircle(sketch, "E2.15.25.0", {"center": v(126.66, -402.1) * mm, "radius": 2 * mm});
            skCircle(sketch, "E2.15.26.0", {"center": v(126.66, -418.1) * mm, "radius": 2 * mm});
            skCircle(sketch, "E2.15.27.0", {"center": v(126.66, -434.1) * mm, "radius": 2 * mm});
            skCircle(sketch, "E2.16.0.0", {"center": v(142.66, -2.1) * mm, "radius": 2 * mm});
            skCircle(sketch, "E2.16.1.0", {"center": v(142.66, -18.1) * mm, "radius": 2 * mm});
            skCircle(sketch, "E2.16.2.0", {"center": v(142.66, -34.1) * mm, "radius": 2 * mm});
            skCircle(sketch, "E2.16.3.0", {"center": v(142.66, -50.1) * mm, "radius": 2 * mm});
            skCircle(sketch, "E2.16.4.0", {"center": v(142.66, -66.1) * mm, "radius": 2 * mm});
            skCircle(sketch, "E2.16.5.0", {"center": v(142.66, -82.1) * mm, "radius": 2 * mm});
            skCircle(sketch, "E2.16.6.0", {"center": v(142.66, -98.1) * mm, "radius": 2 * mm});
            skCircle(sketch, "E2.16.7.0", {"center": v(142.66, -114.1) * mm, "radius": 2 * mm});
            skCircle(sketch, "E2.16.8.0", {"center": v(142.66, -130.1) * mm, "radius": 2 * mm});
            skCircle(sketch, "E2.16.9.0", {"center": v(142.66, -146.1) * mm, "radius": 2 * mm});
            skCircle(sketch, "E2.16.10.0", {"center": v(142.66, -162.1) * mm, "radius": 2 * mm});
            skCircle(sketch, "E2.16.11.0", {"center": v(142.66, -178.1) * mm, "radius": 2 * mm});
            skCircle(sketch, "E2.16.12.0", {"center": v(142.66, -194.1) * mm, "radius": 2 * mm});
            skCircle(sketch, "E2.16.13.0", {"center": v(142.66, -210.1) * mm, "radius": 2 * mm});
            skCircle(sketch, "E2.16.14.0", {"center": v(142.66, -226.1) * mm, "radius": 2 * mm});
            skCircle(sketch, "E2.16.15.0", {"center": v(142.66, -242.1) * mm, "radius": 2 * mm});
            skCircle(sketch, "E2.16.16.0", {"center": v(142.66, -258.1) * mm, "radius": 2 * mm});
            skCircle(sketch, "E2.16.17.0", {"center": v(142.66, -274.1) * mm, "radius": 2 * mm});
            skCircle(sketch, "E2.16.18.0", {"center": v(142.66, -290.1) * mm, "radius": 2 * mm});
            skCircle(sketch, "E2.16.19.0", {"center": v(142.66, -306.1) * mm, "radius": 2 * mm});
            skCircle(sketch, "E2.16.20.0", {"center": v(142.66, -322.1) * mm, "radius": 2 * mm});
            skCircle(sketch, "E2.16.21.0", {"center": v(142.66, -338.1) * mm, "radius": 2 * mm});
            skCircle(sketch, "E2.16.22.0", {"center": v(142.66, -354.1) * mm, "radius": 2 * mm});
            skCircle(sketch, "E2.16.23.0", {"center": v(142.66, -370.1) * mm, "radius": 2 * mm});
            skCircle(sketch, "E2.16.24.0", {"center": v(142.66, -386.1) * mm, "radius": 2 * mm});
            skCircle(sketch, "E2.16.25.0", {"center": v(142.66, -402.1) * mm, "radius": 2 * mm});
            skCircle(sketch, "E2.16.26.0", {"center": v(142.66, -418.1) * mm, "radius": 2 * mm});
            skCircle(sketch, "E2.16.27.0", {"center": v(142.66, -434.1) * mm, "radius": 2 * mm});
            skCircle(sketch, "E2.17.0.0", {"center": v(158.66, -2.1) * mm, "radius": 2 * mm});
            skCircle(sketch, "E2.17.1.0", {"center": v(158.66, -18.1) * mm, "radius": 2 * mm});
            skCircle(sketch, "E2.17.2.0", {"center": v(158.66, -34.1) * mm, "radius": 2 * mm});
            skCircle(sketch, "E2.17.3.0", {"center": v(158.66, -50.1) * mm, "radius": 2 * mm});
            skCircle(sketch, "E2.17.4.0", {"center": v(158.66, -66.1) * mm, "radius": 2 * mm});
            skCircle(sketch, "E2.17.5.0", {"center": v(158.66, -82.1) * mm, "radius": 2 * mm});
            skCircle(sketch, "E2.17.6.0", {"center": v(158.66, -98.1) * mm, "radius": 2 * mm});
            skCircle(sketch, "E2.17.7.0", {"center": v(158.66, -114.1) * mm, "radius": 2 * mm});
            skCircle(sketch, "E2.17.8.0", {"center": v(158.66, -130.1) * mm, "radius": 2 * mm});
            skCircle(sketch, "E2.17.9.0", {"center": v(158.66, -146.1) * mm, "radius": 2 * mm});
            skCircle(sketch, "E2.17.10.0", {"center": v(158.66, -162.1) * mm, "radius": 2 * mm});
            skCircle(sketch, "E2.17.11.0", {"center": v(158.66, -178.1) * mm, "radius": 2 * mm});
            skCircle(sketch, "E2.17.12.0", {"center": v(158.66, -194.1) * mm, "radius": 2 * mm});
            skCircle(sketch, "E2.17.13.0", {"center": v(158.66, -210.1) * mm, "radius": 2 * mm});
            skCircle(sketch, "E2.17.14.0", {"center": v(158.66, -226.1) * mm, "radius": 2 * mm});
            skCircle(sketch, "E2.17.15.0", {"center": v(158.66, -242.1) * mm, "radius": 2 * mm});
            skCircle(sketch, "E2.17.16.0", {"center": v(158.66, -258.1) * mm, "radius": 2 * mm});
            skCircle(sketch, "E2.17.17.0", {"center": v(158.66, -274.1) * mm, "radius": 2 * mm});
            skCircle(sketch, "E2.17.18.0", {"center": v(158.66, -290.1) * mm, "radius": 2 * mm});
            skCircle(sketch, "E2.17.19.0", {"center": v(158.66, -306.1) * mm, "radius": 2 * mm});
            skCircle(sketch, "E2.17.20.0", {"center": v(158.66, -322.1) * mm, "radius": 2 * mm});
            skCircle(sketch, "E2.17.21.0", {"center": v(158.66, -338.1) * mm, "radius": 2 * mm});
            skCircle(sketch, "E2.17.22.0", {"center": v(158.66, -354.1) * mm, "radius": 2 * mm});
            skCircle(sketch, "E2.17.23.0", {"center": v(158.66, -370.1) * mm, "radius": 2 * mm});
            skCircle(sketch, "E2.17.24.0", {"center": v(158.66, -386.1) * mm, "radius": 2 * mm});
            skCircle(sketch, "E2.17.25.0", {"center": v(158.66, -402.1) * mm, "radius": 2 * mm});
            skCircle(sketch, "E2.17.26.0", {"center": v(158.66, -418.1) * mm, "radius": 2 * mm});
            skCircle(sketch, "E2.17.27.0", {"center": v(158.66, -434.1) * mm, "radius": 2 * mm});
            skCircle(sketch, "E2.18.0.0", {"center": v(174.66, -2.1) * mm, "radius": 2 * mm});
            skCircle(sketch, "E2.18.1.0", {"center": v(174.66, -18.1) * mm, "radius": 2 * mm});
            skCircle(sketch, "E2.18.2.0", {"center": v(174.66, -34.1) * mm, "radius": 2 * mm});
            skCircle(sketch, "E2.18.3.0", {"center": v(174.66, -50.1) * mm, "radius": 2 * mm});
            skCircle(sketch, "E2.18.4.0", {"center": v(174.66, -66.1) * mm, "radius": 2 * mm});
            skCircle(sketch, "E2.18.5.0", {"center": v(174.66, -82.1) * mm, "radius": 2 * mm});
            skCircle(sketch, "E2.18.6.0", {"center": v(174.66, -98.1) * mm, "radius": 2 * mm});
            skCircle(sketch, "E2.18.7.0", {"center": v(174.66, -114.1) * mm, "radius": 2 * mm});
            skCircle(sketch, "E2.18.8.0", {"center": v(174.66, -130.1) * mm, "radius": 2 * mm});
            skCircle(sketch, "E2.18.9.0", {"center": v(174.66, -146.1) * mm, "radius": 2 * mm});
            skCircle(sketch, "E2.18.10.0", {"center": v(174.66, -162.1) * mm, "radius": 2 * mm});
            skCircle(sketch, "E2.18.11.0", {"center": v(174.66, -178.1) * mm, "radius": 2 * mm});
            skCircle(sketch, "E2.18.12.0", {"center": v(174.66, -194.1) * mm, "radius": 2 * mm});
            skCircle(sketch, "E2.18.13.0", {"center": v(174.66, -210.1) * mm, "radius": 2 * mm});
            skCircle(sketch, "E2.18.14.0", {"center": v(174.66, -226.1) * mm, "radius": 2 * mm});
            skCircle(sketch, "E2.18.15.0", {"center": v(174.66, -242.1) * mm, "radius": 2 * mm});
            skCircle(sketch, "E2.18.16.0", {"center": v(174.66, -258.1) * mm, "radius": 2 * mm});
            skCircle(sketch, "E2.18.17.0", {"center": v(174.66, -274.1) * mm, "radius": 2 * mm});
            skCircle(sketch, "E2.18.18.0", {"center": v(174.66, -290.1) * mm, "radius": 2 * mm});
            skCircle(sketch, "E2.18.19.0", {"center": v(174.66, -306.1) * mm, "radius": 2 * mm});
            skCircle(sketch, "E2.18.20.0", {"center": v(174.66, -322.1) * mm, "radius": 2 * mm});
            skCircle(sketch, "E2.18.21.0", {"center": v(174.66, -338.1) * mm, "radius": 2 * mm});
            skCircle(sketch, "E2.18.22.0", {"center": v(174.66, -354.1) * mm, "radius": 2 * mm});
            skCircle(sketch, "E2.18.23.0", {"center": v(174.66, -370.1) * mm, "radius": 2 * mm});
            skCircle(sketch, "E2.18.24.0", {"center": v(174.66, -386.1) * mm, "radius": 2 * mm});
            skCircle(sketch, "E2.18.25.0", {"center": v(174.66, -402.1) * mm, "radius": 2 * mm});
            skCircle(sketch, "E2.18.26.0", {"center": v(174.66, -418.1) * mm, "radius": 2 * mm});
            skCircle(sketch, "E2.18.27.0", {"center": v(174.66, -434.1) * mm, "radius": 2 * mm});
            skCircle(sketch, "E2.19.0.0", {"center": v(190.66, -2.1) * mm, "radius": 2 * mm});
            skCircle(sketch, "E2.19.1.0", {"center": v(190.66, -18.1) * mm, "radius": 2 * mm});
            skCircle(sketch, "E2.19.2.0", {"center": v(190.66, -34.1) * mm, "radius": 2 * mm});
            skCircle(sketch, "E2.19.3.0", {"center": v(190.66, -50.1) * mm, "radius": 2 * mm});
            skCircle(sketch, "E2.19.4.0", {"center": v(190.66, -66.1) * mm, "radius": 2 * mm});
            skCircle(sketch, "E2.19.5.0", {"center": v(190.66, -82.1) * mm, "radius": 2 * mm});
            skCircle(sketch, "E2.19.6.0", {"center": v(190.66, -98.1) * mm, "radius": 2 * mm});
            skCircle(sketch, "E2.19.7.0", {"center": v(190.66, -114.1) * mm, "radius": 2 * mm});
            skCircle(sketch, "E2.19.8.0", {"center": v(190.66, -130.1) * mm, "radius": 2 * mm});
            skCircle(sketch, "E2.19.9.0", {"center": v(190.66, -146.1) * mm, "radius": 2 * mm});
            skCircle(sketch, "E2.19.10.0", {"center": v(190.66, -162.1) * mm, "radius": 2 * mm});
            skCircle(sketch, "E2.19.11.0", {"center": v(190.66, -178.1) * mm, "radius": 2 * mm});
            skCircle(sketch, "E2.19.12.0", {"center": v(190.66, -194.1) * mm, "radius": 2 * mm});
            skCircle(sketch, "E2.19.13.0", {"center": v(190.66, -210.1) * mm, "radius": 2 * mm});
            skCircle(sketch, "E2.19.14.0", {"center": v(190.66, -226.1) * mm, "radius": 2 * mm});
            skCircle(sketch, "E2.19.15.0", {"center": v(190.66, -242.1) * mm, "radius": 2 * mm});
            skCircle(sketch, "E2.19.16.0", {"center": v(190.66, -258.1) * mm, "radius": 2 * mm});
            skCircle(sketch, "E2.19.17.0", {"center": v(190.66, -274.1) * mm, "radius": 2 * mm});
            skCircle(sketch, "E2.19.18.0", {"center": v(190.66, -290.1) * mm, "radius": 2 * mm});
            skCircle(sketch, "E2.19.19.0", {"center": v(190.66, -306.1) * mm, "radius": 2 * mm});
            skCircle(sketch, "E2.19.20.0", {"center": v(190.66, -322.1) * mm, "radius": 2 * mm});
            skCircle(sketch, "E2.19.21.0", {"center": v(190.66, -338.1) * mm, "radius": 2 * mm});
            skCircle(sketch, "E2.19.22.0", {"center": v(190.66, -354.1) * mm, "radius": 2 * mm});
            skCircle(sketch, "E2.19.23.0", {"center": v(190.66, -370.1) * mm, "radius": 2 * mm});
            skCircle(sketch, "E2.19.24.0", {"center": v(190.66, -386.1) * mm, "radius": 2 * mm});
            skCircle(sketch, "E2.19.25.0", {"center": v(190.66, -402.1) * mm, "radius": 2 * mm});
            skCircle(sketch, "E2.19.26.0", {"center": v(190.66, -418.1) * mm, "radius": 2 * mm});
            skCircle(sketch, "E2.19.27.0", {"center": v(190.66, -434.1) * mm, "radius": 2 * mm});
            skCircle(sketch, "E2.20.0.0", {"center": v(206.66, -2.1) * mm, "radius": 2 * mm});
            skCircle(sketch, "E2.20.1.0", {"center": v(206.66, -18.1) * mm, "radius": 2 * mm});
            skCircle(sketch, "E2.20.2.0", {"center": v(206.66, -34.1) * mm, "radius": 2 * mm});
            skCircle(sketch, "E2.20.3.0", {"center": v(206.66, -50.1) * mm, "radius": 2 * mm});
            skCircle(sketch, "E2.20.4.0", {"center": v(206.66, -66.1) * mm, "radius": 2 * mm});
            skCircle(sketch, "E2.20.5.0", {"center": v(206.66, -82.1) * mm, "radius": 2 * mm});
            skCircle(sketch, "E2.20.6.0", {"center": v(206.66, -98.1) * mm, "radius": 2 * mm});
            skCircle(sketch, "E2.20.7.0", {"center": v(206.66, -114.1) * mm, "radius": 2 * mm});
            skCircle(sketch, "E2.20.8.0", {"center": v(206.66, -130.1) * mm, "radius": 2 * mm});
            skCircle(sketch, "E2.20.9.0", {"center": v(206.66, -146.1) * mm, "radius": 2 * mm});
            skCircle(sketch, "E2.20.10.0", {"center": v(206.66, -162.1) * mm, "radius": 2 * mm});
            skCircle(sketch, "E2.20.11.0", {"center": v(206.66, -178.1) * mm, "radius": 2 * mm});
            skCircle(sketch, "E2.20.12.0", {"center": v(206.66, -194.1) * mm, "radius": 2 * mm});
            skCircle(sketch, "E2.20.13.0", {"center": v(206.66, -210.1) * mm, "radius": 2 * mm});
            skCircle(sketch, "E2.20.14.0", {"center": v(206.66, -226.1) * mm, "radius": 2 * mm});
            skCircle(sketch, "E2.20.15.0", {"center": v(206.66, -242.1) * mm, "radius": 2 * mm});
            skCircle(sketch, "E2.20.16.0", {"center": v(206.66, -258.1) * mm, "radius": 2 * mm});
            skCircle(sketch, "E2.20.17.0", {"center": v(206.66, -274.1) * mm, "radius": 2 * mm});
            skCircle(sketch, "E2.20.18.0", {"center": v(206.66, -290.1) * mm, "radius": 2 * mm});
            skCircle(sketch, "E2.20.19.0", {"center": v(206.66, -306.1) * mm, "radius": 2 * mm});
            skCircle(sketch, "E2.20.20.0", {"center": v(206.66, -322.1) * mm, "radius": 2 * mm});
            skCircle(sketch, "E2.20.21.0", {"center": v(206.66, -338.1) * mm, "radius": 2 * mm});
            skCircle(sketch, "E2.20.22.0", {"center": v(206.66, -354.1) * mm, "radius": 2 * mm});
            skCircle(sketch, "E2.20.23.0", {"center": v(206.66, -370.1) * mm, "radius": 2 * mm});
            skCircle(sketch, "E2.20.24.0", {"center": v(206.66, -386.1) * mm, "radius": 2 * mm});
            skCircle(sketch, "E2.20.25.0", {"center": v(206.66, -402.1) * mm, "radius": 2 * mm});
            skCircle(sketch, "E2.20.26.0", {"center": v(206.66, -418.1) * mm, "radius": 2 * mm});
            skCircle(sketch, "E2.20.27.0", {"center": v(206.66, -434.1) * mm, "radius": 2 * mm});
            skCircle(sketch, "E2.21.0.0", {"center": v(222.66, -2.1) * mm, "radius": 2 * mm});
            skCircle(sketch, "E2.21.1.0", {"center": v(222.66, -18.1) * mm, "radius": 2 * mm});
            skCircle(sketch, "E2.21.2.0", {"center": v(222.66, -34.1) * mm, "radius": 2 * mm});
            skCircle(sketch, "E2.21.3.0", {"center": v(222.66, -50.1) * mm, "radius": 2 * mm});
            skCircle(sketch, "E2.21.4.0", {"center": v(222.66, -66.1) * mm, "radius": 2 * mm});
            skCircle(sketch, "E2.21.5.0", {"center": v(222.66, -82.1) * mm, "radius": 2 * mm});
            skCircle(sketch, "E2.21.6.0", {"center": v(222.66, -98.1) * mm, "radius": 2 * mm});
            skCircle(sketch, "E2.21.7.0", {"center": v(222.66, -114.1) * mm, "radius": 2 * mm});
            skCircle(sketch, "E2.21.8.0", {"center": v(222.66, -130.1) * mm, "radius": 2 * mm});
            skCircle(sketch, "E2.21.9.0", {"center": v(222.66, -146.1) * mm, "radius": 2 * mm});
            skCircle(sketch, "E2.21.10.0", {"center": v(222.66, -162.1) * mm, "radius": 2 * mm});
            skCircle(sketch, "E2.21.11.0", {"center": v(222.66, -178.1) * mm, "radius": 2 * mm});
            skCircle(sketch, "E2.21.12.0", {"center": v(222.66, -194.1) * mm, "radius": 2 * mm});
            skCircle(sketch, "E2.21.13.0", {"center": v(222.66, -210.1) * mm, "radius": 2 * mm});
            skCircle(sketch, "E2.21.14.0", {"center": v(222.66, -226.1) * mm, "radius": 2 * mm});
            skCircle(sketch, "E2.21.15.0", {"center": v(222.66, -242.1) * mm, "radius": 2 * mm});
            skCircle(sketch, "E2.21.16.0", {"center": v(222.66, -258.1) * mm, "radius": 2 * mm});
            skCircle(sketch, "E2.21.17.0", {"center": v(222.66, -274.1) * mm, "radius": 2 * mm});
            skCircle(sketch, "E2.21.18.0", {"center": v(222.66, -290.1) * mm, "radius": 2 * mm});
            skCircle(sketch, "E2.21.19.0", {"center": v(222.66, -306.1) * mm, "radius": 2 * mm});
            skCircle(sketch, "E2.21.20.0", {"center": v(222.66, -322.1) * mm, "radius": 2 * mm});
            skCircle(sketch, "E2.21.21.0", {"center": v(222.66, -338.1) * mm, "radius": 2 * mm});
            skCircle(sketch, "E2.21.22.0", {"center": v(222.66, -354.1) * mm, "radius": 2 * mm});
            skCircle(sketch, "E2.21.23.0", {"center": v(222.66, -370.1) * mm, "radius": 2 * mm});
            skCircle(sketch, "E2.21.24.0", {"center": v(222.66, -386.1) * mm, "radius": 2 * mm});
            skCircle(sketch, "E2.21.25.0", {"center": v(222.66, -402.1) * mm, "radius": 2 * mm});
            skCircle(sketch, "E2.21.26.0", {"center": v(222.66, -418.1) * mm, "radius": 2 * mm});
            skCircle(sketch, "E2.21.27.0", {"center": v(222.66, -434.1) * mm, "radius": 2 * mm});
            skCircle(sketch, "E2.22.0.0", {"center": v(238.66, -2.1) * mm, "radius": 2 * mm});
            skCircle(sketch, "E2.22.1.0", {"center": v(238.66, -18.1) * mm, "radius": 2 * mm});
            skCircle(sketch, "E2.22.2.0", {"center": v(238.66, -34.1) * mm, "radius": 2 * mm});
            skCircle(sketch, "E2.22.3.0", {"center": v(238.66, -50.1) * mm, "radius": 2 * mm});
            skCircle(sketch, "E2.22.4.0", {"center": v(238.66, -66.1) * mm, "radius": 2 * mm});
            skCircle(sketch, "E2.22.5.0", {"center": v(238.66, -82.1) * mm, "radius": 2 * mm});
            skCircle(sketch, "E2.22.6.0", {"center": v(238.66, -98.1) * mm, "radius": 2 * mm});
            skCircle(sketch, "E2.22.7.0", {"center": v(238.66, -114.1) * mm, "radius": 2 * mm});
            skCircle(sketch, "E2.22.8.0", {"center": v(238.66, -130.1) * mm, "radius": 2 * mm});
            skCircle(sketch, "E2.22.9.0", {"center": v(238.66, -146.1) * mm, "radius": 2 * mm});
            skCircle(sketch, "E2.22.10.0", {"center": v(238.66, -162.1) * mm, "radius": 2 * mm});
            skCircle(sketch, "E2.22.11.0", {"center": v(238.66, -178.1) * mm, "radius": 2 * mm});
            skCircle(sketch, "E2.22.12.0", {"center": v(238.66, -194.1) * mm, "radius": 2 * mm});
            skCircle(sketch, "E2.22.13.0", {"center": v(238.66, -210.1) * mm, "radius": 2 * mm});
            skCircle(sketch, "E2.22.14.0", {"center": v(238.66, -226.1) * mm, "radius": 2 * mm});
            skCircle(sketch, "E2.22.15.0", {"center": v(238.66, -242.1) * mm, "radius": 2 * mm});
            skCircle(sketch, "E2.22.16.0", {"center": v(238.66, -258.1) * mm, "radius": 2 * mm});
            skCircle(sketch, "E2.22.17.0", {"center": v(238.66, -274.1) * mm, "radius": 2 * mm});
            skCircle(sketch, "E2.22.18.0", {"center": v(238.66, -290.1) * mm, "radius": 2 * mm});
            skCircle(sketch, "E2.22.19.0", {"center": v(238.66, -306.1) * mm, "radius": 2 * mm});
            skCircle(sketch, "E2.22.20.0", {"center": v(238.66, -322.1) * mm, "radius": 2 * mm});
            skCircle(sketch, "E2.22.21.0", {"center": v(238.66, -338.1) * mm, "radius": 2 * mm});
            skCircle(sketch, "E2.22.22.0", {"center": v(238.66, -354.1) * mm, "radius": 2 * mm});
            skCircle(sketch, "E2.22.23.0", {"center": v(238.66, -370.1) * mm, "radius": 2 * mm});
            skCircle(sketch, "E2.22.24.0", {"center": v(238.66, -386.1) * mm, "radius": 2 * mm});
            skCircle(sketch, "E2.22.25.0", {"center": v(238.66, -402.1) * mm, "radius": 2 * mm});
            skCircle(sketch, "E2.22.26.0", {"center": v(238.66, -418.1) * mm, "radius": 2 * mm});
            skCircle(sketch, "E2.22.27.0", {"center": v(238.66, -434.1) * mm, "radius": 2 * mm});
            skCircle(sketch, "E2.23.0.0", {"center": v(254.66, -2.1) * mm, "radius": 2 * mm});
            skCircle(sketch, "E2.23.1.0", {"center": v(254.66, -18.1) * mm, "radius": 2 * mm});
            skCircle(sketch, "E2.23.2.0", {"center": v(254.66, -34.1) * mm, "radius": 2 * mm});
            skCircle(sketch, "E2.23.3.0", {"center": v(254.66, -50.1) * mm, "radius": 2 * mm});
            skCircle(sketch, "E2.23.4.0", {"center": v(254.66, -66.1) * mm, "radius": 2 * mm});
            skCircle(sketch, "E2.23.5.0", {"center": v(254.66, -82.1) * mm, "radius": 2 * mm});
            skCircle(sketch, "E2.23.6.0", {"center": v(254.66, -98.1) * mm, "radius": 2 * mm});
            skCircle(sketch, "E2.23.7.0", {"center": v(254.66, -114.1) * mm, "radius": 2 * mm});
            skCircle(sketch, "E2.23.8.0", {"center": v(254.66, -130.1) * mm, "radius": 2 * mm});
            skCircle(sketch, "E2.23.9.0", {"center": v(254.66, -146.1) * mm, "radius": 2 * mm});
            skCircle(sketch, "E2.23.10.0", {"center": v(254.66, -162.1) * mm, "radius": 2 * mm});
            skCircle(sketch, "E2.23.11.0", {"center": v(254.66, -178.1) * mm, "radius": 2 * mm});
            skCircle(sketch, "E2.23.12.0", {"center": v(254.66, -194.1) * mm, "radius": 2 * mm});
            skCircle(sketch, "E2.23.13.0", {"center": v(254.66, -210.1) * mm, "radius": 2 * mm});
            skCircle(sketch, "E2.23.14.0", {"center": v(254.66, -226.1) * mm, "radius": 2 * mm});
            skCircle(sketch, "E2.23.15.0", {"center": v(254.66, -242.1) * mm, "radius": 2 * mm});
            skCircle(sketch, "E2.23.16.0", {"center": v(254.66, -258.1) * mm, "radius": 2 * mm});
            skCircle(sketch, "E2.23.17.0", {"center": v(254.66, -274.1) * mm, "radius": 2 * mm});
            skCircle(sketch, "E2.23.18.0", {"center": v(254.66, -290.1) * mm, "radius": 2 * mm});
            skCircle(sketch, "E2.23.19.0", {"center": v(254.66, -306.1) * mm, "radius": 2 * mm});
            skCircle(sketch, "E2.23.20.0", {"center": v(254.66, -322.1) * mm, "radius": 2 * mm});
            skCircle(sketch, "E2.23.21.0", {"center": v(254.66, -338.1) * mm, "radius": 2 * mm});
            skCircle(sketch, "E2.23.22.0", {"center": v(254.66, -354.1) * mm, "radius": 2 * mm});
            skCircle(sketch, "E2.23.23.0", {"center": v(254.66, -370.1) * mm, "radius": 2 * mm});
            skCircle(sketch, "E2.23.24.0", {"center": v(254.66, -386.1) * mm, "radius": 2 * mm});
            skCircle(sketch, "E2.23.25.0", {"center": v(254.66, -402.1) * mm, "radius": 2 * mm});
            skCircle(sketch, "E2.23.26.0", {"center": v(254.66, -418.1) * mm, "radius": 2 * mm});
            skCircle(sketch, "E2.23.27.0", {"center": v(254.66, -434.1) * mm, "radius": 2 * mm});
            skCircle(sketch, "E2.24.0.0", {"center": v(270.66, -2.1) * mm, "radius": 2 * mm});
            skCircle(sketch, "E2.24.1.0", {"center": v(270.66, -18.1) * mm, "radius": 2 * mm});
            skCircle(sketch, "E2.24.2.0", {"center": v(270.66, -34.1) * mm, "radius": 2 * mm});
            skCircle(sketch, "E2.24.3.0", {"center": v(270.66, -50.1) * mm, "radius": 2 * mm});
            skCircle(sketch, "E2.24.4.0", {"center": v(270.66, -66.1) * mm, "radius": 2 * mm});
            skCircle(sketch, "E2.24.5.0", {"center": v(270.66, -82.1) * mm, "radius": 2 * mm});
            skCircle(sketch, "E2.24.6.0", {"center": v(270.66, -98.1) * mm, "radius": 2 * mm});
            skCircle(sketch, "E2.24.7.0", {"center": v(270.66, -114.1) * mm, "radius": 2 * mm});
            skCircle(sketch, "E2.24.8.0", {"center": v(270.66, -130.1) * mm, "radius": 2 * mm});
            skCircle(sketch, "E2.24.9.0", {"center": v(270.66, -146.1) * mm, "radius": 2 * mm});
            skCircle(sketch, "E2.24.10.0", {"center": v(270.66, -162.1) * mm, "radius": 2 * mm});
            skCircle(sketch, "E2.24.11.0", {"center": v(270.66, -178.1) * mm, "radius": 2 * mm});
            skCircle(sketch, "E2.24.12.0", {"center": v(270.66, -194.1) * mm, "radius": 2 * mm});
            skCircle(sketch, "E2.24.13.0", {"center": v(270.66, -210.1) * mm, "radius": 2 * mm});
            skCircle(sketch, "E2.24.14.0", {"center": v(270.66, -226.1) * mm, "radius": 2 * mm});
            skCircle(sketch, "E2.24.15.0", {"center": v(270.66, -242.1) * mm, "radius": 2 * mm});
            skCircle(sketch, "E2.24.16.0", {"center": v(270.66, -258.1) * mm, "radius": 2 * mm});
            skCircle(sketch, "E2.24.17.0", {"center": v(270.66, -274.1) * mm, "radius": 2 * mm});
            skCircle(sketch, "E2.24.18.0", {"center": v(270.66, -290.1) * mm, "radius": 2 * mm});
            skCircle(sketch, "E2.24.19.0", {"center": v(270.66, -306.1) * mm, "radius": 2 * mm});
            skCircle(sketch, "E2.24.20.0", {"center": v(270.66, -322.1) * mm, "radius": 2 * mm});
            skCircle(sketch, "E2.24.21.0", {"center": v(270.66, -338.1) * mm, "radius": 2 * mm});
            skCircle(sketch, "E2.24.22.0", {"center": v(270.66, -354.1) * mm, "radius": 2 * mm});
            skCircle(sketch, "E2.24.23.0", {"center": v(270.66, -370.1) * mm, "radius": 2 * mm});
            skCircle(sketch, "E2.24.24.0", {"center": v(270.66, -386.1) * mm, "radius": 2 * mm});
            skCircle(sketch, "E2.24.25.0", {"center": v(270.66, -402.1) * mm, "radius": 2 * mm});
            skCircle(sketch, "E2.24.26.0", {"center": v(270.66, -418.1) * mm, "radius": 2 * mm});
            skCircle(sketch, "E2.24.27.0", {"center": v(270.66, -434.1) * mm, "radius": 2 * mm});
            skCircle(sketch, "E2.25.0.0", {"center": v(286.66, -2.1) * mm, "radius": 2 * mm});
            skCircle(sketch, "E2.25.1.0", {"center": v(286.66, -18.1) * mm, "radius": 2 * mm});
            skCircle(sketch, "E2.25.2.0", {"center": v(286.66, -34.1) * mm, "radius": 2 * mm});
            skCircle(sketch, "E2.25.3.0", {"center": v(286.66, -50.1) * mm, "radius": 2 * mm});
            skCircle(sketch, "E2.25.4.0", {"center": v(286.66, -66.1) * mm, "radius": 2 * mm});
            skCircle(sketch, "E2.25.5.0", {"center": v(286.66, -82.1) * mm, "radius": 2 * mm});
            skCircle(sketch, "E2.25.6.0", {"center": v(286.66, -98.1) * mm, "radius": 2 * mm});
            skCircle(sketch, "E2.25.7.0", {"center": v(286.66, -114.1) * mm, "radius": 2 * mm});
            skCircle(sketch, "E2.25.8.0", {"center": v(286.66, -130.1) * mm, "radius": 2 * mm});
            skCircle(sketch, "E2.25.9.0", {"center": v(286.66, -146.1) * mm, "radius": 2 * mm});
            skCircle(sketch, "E2.25.10.0", {"center": v(286.66, -162.1) * mm, "radius": 2 * mm});
            skCircle(sketch, "E2.25.11.0", {"center": v(286.66, -178.1) * mm, "radius": 2 * mm});
            skCircle(sketch, "E2.25.12.0", {"center": v(286.66, -194.1) * mm, "radius": 2 * mm});
            skCircle(sketch, "E2.25.13.0", {"center": v(286.66, -210.1) * mm, "radius": 2 * mm});
            skCircle(sketch, "E2.25.14.0", {"center": v(286.66, -226.1) * mm, "radius": 2 * mm});
            skCircle(sketch, "E2.25.15.0", {"center": v(286.66, -242.1) * mm, "radius": 2 * mm});
            skCircle(sketch, "E2.25.16.0", {"center": v(286.66, -258.1) * mm, "radius": 2 * mm});
            skCircle(sketch, "E2.25.17.0", {"center": v(286.66, -274.1) * mm, "radius": 2 * mm});
            skCircle(sketch, "E2.25.18.0", {"center": v(286.66, -290.1) * mm, "radius": 2 * mm});
            skCircle(sketch, "E2.25.19.0", {"center": v(286.66, -306.1) * mm, "radius": 2 * mm});
            skCircle(sketch, "E2.25.20.0", {"center": v(286.66, -322.1) * mm, "radius": 2 * mm});
            skCircle(sketch, "E2.25.21.0", {"center": v(286.66, -338.1) * mm, "radius": 2 * mm});
            skCircle(sketch, "E2.25.22.0", {"center": v(286.66, -354.1) * mm, "radius": 2 * mm});
            skCircle(sketch, "E2.25.23.0", {"center": v(286.66, -370.1) * mm, "radius": 2 * mm});
            skCircle(sketch, "E2.25.24.0", {"center": v(286.66, -386.1) * mm, "radius": 2 * mm});
            skCircle(sketch, "E2.25.25.0", {"center": v(286.66, -402.1) * mm, "radius": 2 * mm});
            skCircle(sketch, "E2.25.26.0", {"center": v(286.66, -418.1) * mm, "radius": 2 * mm});
            skCircle(sketch, "E2.25.27.0", {"center": v(286.66, -434.1) * mm, "radius": 2 * mm});
            skCircle(sketch, "E2.26.0.0", {"center": v(302.66, -2.1) * mm, "radius": 2 * mm});
            skCircle(sketch, "E2.26.1.0", {"center": v(302.66, -18.1) * mm, "radius": 2 * mm});
            skCircle(sketch, "E2.26.2.0", {"center": v(302.66, -34.1) * mm, "radius": 2 * mm});
            skCircle(sketch, "E2.26.3.0", {"center": v(302.66, -50.1) * mm, "radius": 2 * mm});
            skCircle(sketch, "E2.26.4.0", {"center": v(302.66, -66.1) * mm, "radius": 2 * mm});
            skCircle(sketch, "E2.26.5.0", {"center": v(302.66, -82.1) * mm, "radius": 2 * mm});
            skCircle(sketch, "E2.26.6.0", {"center": v(302.66, -98.1) * mm, "radius": 2 * mm});
            skCircle(sketch, "E2.26.7.0", {"center": v(302.66, -114.1) * mm, "radius": 2 * mm});
            skCircle(sketch, "E2.26.8.0", {"center": v(302.66, -130.1) * mm, "radius": 2 * mm});
            skCircle(sketch, "E2.26.9.0", {"center": v(302.66, -146.1) * mm, "radius": 2 * mm});
            skCircle(sketch, "E2.26.10.0", {"center": v(302.66, -162.1) * mm, "radius": 2 * mm});
            skCircle(sketch, "E2.26.11.0", {"center": v(302.66, -178.1) * mm, "radius": 2 * mm});
            skCircle(sketch, "E2.26.12.0", {"center": v(302.66, -194.1) * mm, "radius": 2 * mm});
            skCircle(sketch, "E2.26.13.0", {"center": v(302.66, -210.1) * mm, "radius": 2 * mm});
            skCircle(sketch, "E2.26.14.0", {"center": v(302.66, -226.1) * mm, "radius": 2 * mm});
            skCircle(sketch, "E2.26.15.0", {"center": v(302.66, -242.1) * mm, "radius": 2 * mm});
            skCircle(sketch, "E2.26.16.0", {"center": v(302.66, -258.1) * mm, "radius": 2 * mm});
            skCircle(sketch, "E2.26.17.0", {"center": v(302.66, -274.1) * mm, "radius": 2 * mm});
            skCircle(sketch, "E2.26.18.0", {"center": v(302.66, -290.1) * mm, "radius": 2 * mm});
            skCircle(sketch, "E2.26.19.0", {"center": v(302.66, -306.1) * mm, "radius": 2 * mm});
            skCircle(sketch, "E2.26.20.0", {"center": v(302.66, -322.1) * mm, "radius": 2 * mm});
            skCircle(sketch, "E2.26.21.0", {"center": v(302.66, -338.1) * mm, "radius": 2 * mm});
            skCircle(sketch, "E2.26.22.0", {"center": v(302.66, -354.1) * mm, "radius": 2 * mm});
            skCircle(sketch, "E2.26.23.0", {"center": v(302.66, -370.1) * mm, "radius": 2 * mm});
            skCircle(sketch, "E2.26.24.0", {"center": v(302.66, -386.1) * mm, "radius": 2 * mm});
            skCircle(sketch, "E2.26.25.0", {"center": v(302.66, -402.1) * mm, "radius": 2 * mm});
            skCircle(sketch, "E2.26.26.0", {"center": v(302.66, -418.1) * mm, "radius": 2 * mm});
            skCircle(sketch, "E2.26.27.0", {"center": v(302.66, -434.1) * mm, "radius": 2 * mm});
            skCircle(sketch, "E2.27.0.0", {"center": v(318.66, -2.1) * mm, "radius": 2 * mm});
            skCircle(sketch, "E2.27.1.0", {"center": v(318.66, -18.1) * mm, "radius": 2 * mm});
            skCircle(sketch, "E2.27.2.0", {"center": v(318.66, -34.1) * mm, "radius": 2 * mm});
            skCircle(sketch, "E2.27.3.0", {"center": v(318.66, -50.1) * mm, "radius": 2 * mm});
            skCircle(sketch, "E2.27.4.0", {"center": v(318.66, -66.1) * mm, "radius": 2 * mm});
            skCircle(sketch, "E2.27.5.0", {"center": v(318.66, -82.1) * mm, "radius": 2 * mm});
            skCircle(sketch, "E2.27.6.0", {"center": v(318.66, -98.1) * mm, "radius": 2 * mm});
            skCircle(sketch, "E2.27.7.0", {"center": v(318.66, -114.1) * mm, "radius": 2 * mm});
            skCircle(sketch, "E2.27.8.0", {"center": v(318.66, -130.1) * mm, "radius": 2 * mm});
            skCircle(sketch, "E2.27.9.0", {"center": v(318.66, -146.1) * mm, "radius": 2 * mm});
            skCircle(sketch, "E2.27.10.0", {"center": v(318.66, -162.1) * mm, "radius": 2 * mm});
            skCircle(sketch, "E2.27.11.0", {"center": v(318.66, -178.1) * mm, "radius": 2 * mm});
            skCircle(sketch, "E2.27.12.0", {"center": v(318.66, -194.1) * mm, "radius": 2 * mm});
            skCircle(sketch, "E2.27.13.0", {"center": v(318.66, -210.1) * mm, "radius": 2 * mm});
            skCircle(sketch, "E2.27.14.0", {"center": v(318.66, -226.1) * mm, "radius": 2 * mm});
            skCircle(sketch, "E2.27.15.0", {"center": v(318.66, -242.1) * mm, "radius": 2 * mm});
            skCircle(sketch, "E2.27.16.0", {"center": v(318.66, -258.1) * mm, "radius": 2 * mm});
            skCircle(sketch, "E2.27.17.0", {"center": v(318.66, -274.1) * mm, "radius": 2 * mm});
            skCircle(sketch, "E2.27.18.0", {"center": v(318.66, -290.1) * mm, "radius": 2 * mm});
            skCircle(sketch, "E2.27.19.0", {"center": v(318.66, -306.1) * mm, "radius": 2 * mm});
            skCircle(sketch, "E2.27.20.0", {"center": v(318.66, -322.1) * mm, "radius": 2 * mm});
            skCircle(sketch, "E2.27.21.0", {"center": v(318.66, -338.1) * mm, "radius": 2 * mm});
            skCircle(sketch, "E2.27.22.0", {"center": v(318.66, -354.1) * mm, "radius": 2 * mm});
            skCircle(sketch, "E2.27.23.0", {"center": v(318.66, -370.1) * mm, "radius": 2 * mm});
            skCircle(sketch, "E2.27.24.0", {"center": v(318.66, -386.1) * mm, "radius": 2 * mm});
            skCircle(sketch, "E2.27.25.0", {"center": v(318.66, -402.1) * mm, "radius": 2 * mm});
            skCircle(sketch, "E2.27.26.0", {"center": v(318.66, -418.1) * mm, "radius": 2 * mm});
            skCircle(sketch, "E2.27.27.0", {"center": v(318.66, -434.1) * mm, "radius": 2 * mm});
            skCircle(sketch, "E2.28.0.0", {"center": v(334.66, -2.1) * mm, "radius": 2 * mm});
            skCircle(sketch, "E2.28.1.0", {"center": v(334.66, -18.1) * mm, "radius": 2 * mm});
            skCircle(sketch, "E2.28.2.0", {"center": v(334.66, -34.1) * mm, "radius": 2 * mm});
            skCircle(sketch, "E2.28.3.0", {"center": v(334.66, -50.1) * mm, "radius": 2 * mm});
            skCircle(sketch, "E2.28.4.0", {"center": v(334.66, -66.1) * mm, "radius": 2 * mm});
            skCircle(sketch, "E2.28.5.0", {"center": v(334.66, -82.1) * mm, "radius": 2 * mm});
            skCircle(sketch, "E2.28.6.0", {"center": v(334.66, -98.1) * mm, "radius": 2 * mm});
            skCircle(sketch, "E2.28.7.0", {"center": v(334.66, -114.1) * mm, "radius": 2 * mm});
            skCircle(sketch, "E2.28.8.0", {"center": v(334.66, -130.1) * mm, "radius": 2 * mm});
            skCircle(sketch, "E2.28.9.0", {"center": v(334.66, -146.1) * mm, "radius": 2 * mm});
            skCircle(sketch, "E2.28.10.0", {"center": v(334.66, -162.1) * mm, "radius": 2 * mm});
            skCircle(sketch, "E2.28.11.0", {"center": v(334.66, -178.1) * mm, "radius": 2 * mm});
            skCircle(sketch, "E2.28.12.0", {"center": v(334.66, -194.1) * mm, "radius": 2 * mm});
            skCircle(sketch, "E2.28.13.0", {"center": v(334.66, -210.1) * mm, "radius": 2 * mm});
            skCircle(sketch, "E2.28.14.0", {"center": v(334.66, -226.1) * mm, "radius": 2 * mm});
            skCircle(sketch, "E2.28.15.0", {"center": v(334.66, -242.1) * mm, "radius": 2 * mm});
            skCircle(sketch, "E2.28.16.0", {"center": v(334.66, -258.1) * mm, "radius": 2 * mm});
            skCircle(sketch, "E2.28.17.0", {"center": v(334.66, -274.1) * mm, "radius": 2 * mm});
            skCircle(sketch, "E2.28.18.0", {"center": v(334.66, -290.1) * mm, "radius": 2 * mm});
            skCircle(sketch, "E2.28.19.0", {"center": v(334.66, -306.1) * mm, "radius": 2 * mm});
            skCircle(sketch, "E2.28.20.0", {"center": v(334.66, -322.1) * mm, "radius": 2 * mm});
            skCircle(sketch, "E2.28.21.0", {"center": v(334.66, -338.1) * mm, "radius": 2 * mm});
            skCircle(sketch, "E2.28.22.0", {"center": v(334.66, -354.1) * mm, "radius": 2 * mm});
            skCircle(sketch, "E2.28.23.0", {"center": v(334.66, -370.1) * mm, "radius": 2 * mm});
            skCircle(sketch, "E2.28.24.0", {"center": v(334.66, -386.1) * mm, "radius": 2 * mm});
            skCircle(sketch, "E2.28.25.0", {"center": v(334.66, -402.1) * mm, "radius": 2 * mm});
            skCircle(sketch, "E2.28.26.0", {"center": v(334.66, -418.1) * mm, "radius": 2 * mm});
            skCircle(sketch, "E2.28.27.0", {"center": v(334.66, -434.1) * mm, "radius": 2 * mm});
            skCircle(sketch, "E2.29.0.0", {"center": v(350.66, -2.1) * mm, "radius": 2 * mm});
            skCircle(sketch, "E2.29.1.0", {"center": v(350.66, -18.1) * mm, "radius": 2 * mm});
            skCircle(sketch, "E2.29.2.0", {"center": v(350.66, -34.1) * mm, "radius": 2 * mm});
            skCircle(sketch, "E2.29.3.0", {"center": v(350.66, -50.1) * mm, "radius": 2 * mm});
            skCircle(sketch, "E2.29.4.0", {"center": v(350.66, -66.1) * mm, "radius": 2 * mm});
            skCircle(sketch, "E2.29.5.0", {"center": v(350.66, -82.1) * mm, "radius": 2 * mm});
            skCircle(sketch, "E2.29.6.0", {"center": v(350.66, -98.1) * mm, "radius": 2 * mm});
            skCircle(sketch, "E2.29.7.0", {"center": v(350.66, -114.1) * mm, "radius": 2 * mm});
            skCircle(sketch, "E2.29.8.0", {"center": v(350.66, -130.1) * mm, "radius": 2 * mm});
            skCircle(sketch, "E2.29.9.0", {"center": v(350.66, -146.1) * mm, "radius": 2 * mm});
            skCircle(sketch, "E2.29.10.0", {"center": v(350.66, -162.1) * mm, "radius": 2 * mm});
            skCircle(sketch, "E2.29.11.0", {"center": v(350.66, -178.1) * mm, "radius": 2 * mm});
            skCircle(sketch, "E2.29.12.0", {"center": v(350.66, -194.1) * mm, "radius": 2 * mm});
            skCircle(sketch, "E2.29.13.0", {"center": v(350.66, -210.1) * mm, "radius": 2 * mm});
            skCircle(sketch, "E2.29.14.0", {"center": v(350.66, -226.1) * mm, "radius": 2 * mm});
            skCircle(sketch, "E2.29.15.0", {"center": v(350.66, -242.1) * mm, "radius": 2 * mm});
            skCircle(sketch, "E2.29.16.0", {"center": v(350.66, -258.1) * mm, "radius": 2 * mm});
            skCircle(sketch, "E2.29.17.0", {"center": v(350.66, -274.1) * mm, "radius": 2 * mm});
            skCircle(sketch, "E2.29.18.0", {"center": v(350.66, -290.1) * mm, "radius": 2 * mm});
            skCircle(sketch, "E2.29.19.0", {"center": v(350.66, -306.1) * mm, "radius": 2 * mm});
            skCircle(sketch, "E2.29.20.0", {"center": v(350.66, -322.1) * mm, "radius": 2 * mm});
            skCircle(sketch, "E2.29.21.0", {"center": v(350.66, -338.1) * mm, "radius": 2 * mm});
            skCircle(sketch, "E2.29.22.0", {"center": v(350.66, -354.1) * mm, "radius": 2 * mm});
            skCircle(sketch, "E2.29.23.0", {"center": v(350.66, -370.1) * mm, "radius": 2 * mm});
            skCircle(sketch, "E2.29.24.0", {"center": v(350.66, -386.1) * mm, "radius": 2 * mm});
            skCircle(sketch, "E2.29.25.0", {"center": v(350.66, -402.1) * mm, "radius": 2 * mm});
            skCircle(sketch, "E2.29.26.0", {"center": v(350.66, -418.1) * mm, "radius": 2 * mm});
            skCircle(sketch, "E2.29.27.0", {"center": v(350.66, -434.1) * mm, "radius": 2 * mm});
            skCircle(sketch, "E2.30.0.0", {"center": v(366.66, -2.1) * mm, "radius": 2 * mm});
            skCircle(sketch, "E2.30.1.0", {"center": v(366.66, -18.1) * mm, "radius": 2 * mm});
            skCircle(sketch, "E2.30.2.0", {"center": v(366.66, -34.1) * mm, "radius": 2 * mm});
            skCircle(sketch, "E2.30.3.0", {"center": v(366.66, -50.1) * mm, "radius": 2 * mm});
            skCircle(sketch, "E2.30.4.0", {"center": v(366.66, -66.1) * mm, "radius": 2 * mm});
            skCircle(sketch, "E2.30.5.0", {"center": v(366.66, -82.1) * mm, "radius": 2 * mm});
            skCircle(sketch, "E2.30.6.0", {"center": v(366.66, -98.1) * mm, "radius": 2 * mm});
            skCircle(sketch, "E2.30.7.0", {"center": v(366.66, -114.1) * mm, "radius": 2 * mm});
            skCircle(sketch, "E2.30.8.0", {"center": v(366.66, -130.1) * mm, "radius": 2 * mm});
            skCircle(sketch, "E2.30.9.0", {"center": v(366.66, -146.1) * mm, "radius": 2 * mm});
            skCircle(sketch, "E2.30.10.0", {"center": v(366.66, -162.1) * mm, "radius": 2 * mm});
            skCircle(sketch, "E2.30.11.0", {"center": v(366.66, -178.1) * mm, "radius": 2 * mm});
            skCircle(sketch, "E2.30.12.0", {"center": v(366.66, -194.1) * mm, "radius": 2 * mm});
            skCircle(sketch, "E2.30.13.0", {"center": v(366.66, -210.1) * mm, "radius": 2 * mm});
            skCircle(sketch, "E2.30.14.0", {"center": v(366.66, -226.1) * mm, "radius": 2 * mm});
            skCircle(sketch, "E2.30.15.0", {"center": v(366.66, -242.1) * mm, "radius": 2 * mm});
            skCircle(sketch, "E2.30.16.0", {"center": v(366.66, -258.1) * mm, "radius": 2 * mm});
            skCircle(sketch, "E2.30.17.0", {"center": v(366.66, -274.1) * mm, "radius": 2 * mm});
            skCircle(sketch, "E2.30.18.0", {"center": v(366.66, -290.1) * mm, "radius": 2 * mm});
            skCircle(sketch, "E2.30.19.0", {"center": v(366.66, -306.1) * mm, "radius": 2 * mm});
            skCircle(sketch, "E2.30.20.0", {"center": v(366.66, -322.1) * mm, "radius": 2 * mm});
            skCircle(sketch, "E2.30.21.0", {"center": v(366.66, -338.1) * mm, "radius": 2 * mm});
            skCircle(sketch, "E2.30.22.0", {"center": v(366.66, -354.1) * mm, "radius": 2 * mm});
            skCircle(sketch, "E2.30.23.0", {"center": v(366.66, -370.1) * mm, "radius": 2 * mm});
            skCircle(sketch, "E2.30.24.0", {"center": v(366.66, -386.1) * mm, "radius": 2 * mm});
            skCircle(sketch, "E2.30.25.0", {"center": v(366.66, -402.1) * mm, "radius": 2 * mm});
            skCircle(sketch, "E2.30.26.0", {"center": v(366.66, -418.1) * mm, "radius": 2 * mm});
            skCircle(sketch, "E2.30.27.0", {"center": v(366.66, -434.1) * mm, "radius": 2 * mm});
            skCircle(sketch, "E2.31.0.0", {"center": v(382.66, -2.1) * mm, "radius": 2 * mm});
            skCircle(sketch, "E2.31.1.0", {"center": v(382.66, -18.1) * mm, "radius": 2 * mm});
            skCircle(sketch, "E2.31.2.0", {"center": v(382.66, -34.1) * mm, "radius": 2 * mm});
            skCircle(sketch, "E2.31.3.0", {"center": v(382.66, -50.1) * mm, "radius": 2 * mm});
            skCircle(sketch, "E2.31.4.0", {"center": v(382.66, -66.1) * mm, "radius": 2 * mm});
            skCircle(sketch, "E2.31.5.0", {"center": v(382.66, -82.1) * mm, "radius": 2 * mm});
            skCircle(sketch, "E2.31.6.0", {"center": v(382.66, -98.1) * mm, "radius": 2 * mm});
            skCircle(sketch, "E2.31.7.0", {"center": v(382.66, -114.1) * mm, "radius": 2 * mm});
            skCircle(sketch, "E2.31.8.0", {"center": v(382.66, -130.1) * mm, "radius": 2 * mm});
            skCircle(sketch, "E2.31.9.0", {"center": v(382.66, -146.1) * mm, "radius": 2 * mm});
            skCircle(sketch, "E2.31.10.0", {"center": v(382.66, -162.1) * mm, "radius": 2 * mm});
            skCircle(sketch, "E2.31.11.0", {"center": v(382.66, -178.1) * mm, "radius": 2 * mm});
            skCircle(sketch, "E2.31.12.0", {"center": v(382.66, -194.1) * mm, "radius": 2 * mm});
            skCircle(sketch, "E2.31.13.0", {"center": v(382.66, -210.1) * mm, "radius": 2 * mm});
            skCircle(sketch, "E2.31.14.0", {"center": v(382.66, -226.1) * mm, "radius": 2 * mm});
            skCircle(sketch, "E2.31.15.0", {"center": v(382.66, -242.1) * mm, "radius": 2 * mm});
            skCircle(sketch, "E2.31.16.0", {"center": v(382.66, -258.1) * mm, "radius": 2 * mm});
            skCircle(sketch, "E2.31.17.0", {"center": v(382.66, -274.1) * mm, "radius": 2 * mm});
            skCircle(sketch, "E2.31.18.0", {"center": v(382.66, -290.1) * mm, "radius": 2 * mm});
            skCircle(sketch, "E2.31.19.0", {"center": v(382.66, -306.1) * mm, "radius": 2 * mm});
            skCircle(sketch, "E2.31.20.0", {"center": v(382.66, -322.1) * mm, "radius": 2 * mm});
            skCircle(sketch, "E2.31.21.0", {"center": v(382.66, -338.1) * mm, "radius": 2 * mm});
            skCircle(sketch, "E2.31.22.0", {"center": v(382.66, -354.1) * mm, "radius": 2 * mm});
            skCircle(sketch, "E2.31.23.0", {"center": v(382.66, -370.1) * mm, "radius": 2 * mm});
            skCircle(sketch, "E2.31.24.0", {"center": v(382.66, -386.1) * mm, "radius": 2 * mm});
            skCircle(sketch, "E2.31.25.0", {"center": v(382.66, -402.1) * mm, "radius": 2 * mm});
            skCircle(sketch, "E2.31.26.0", {"center": v(382.66, -418.1) * mm, "radius": 2 * mm});
            skCircle(sketch, "E2.31.27.0", {"center": v(382.66, -434.1) * mm, "radius": 2 * mm});
            skCircle(sketch, "E2.32.0.0", {"center": v(398.66, -2.1) * mm, "radius": 2 * mm});
            skCircle(sketch, "E2.32.1.0", {"center": v(398.66, -18.1) * mm, "radius": 2 * mm});
            skCircle(sketch, "E2.32.2.0", {"center": v(398.66, -34.1) * mm, "radius": 2 * mm});
            skCircle(sketch, "E2.32.3.0", {"center": v(398.66, -50.1) * mm, "radius": 2 * mm});
            skCircle(sketch, "E2.32.4.0", {"center": v(398.66, -66.1) * mm, "radius": 2 * mm});
            skCircle(sketch, "E2.32.5.0", {"center": v(398.66, -82.1) * mm, "radius": 2 * mm});
            skCircle(sketch, "E2.32.6.0", {"center": v(398.66, -98.1) * mm, "radius": 2 * mm});
            skCircle(sketch, "E2.32.7.0", {"center": v(398.66, -114.1) * mm, "radius": 2 * mm});
            skCircle(sketch, "E2.32.8.0", {"center": v(398.66, -130.1) * mm, "radius": 2 * mm});
            skCircle(sketch, "E2.32.9.0", {"center": v(398.66, -146.1) * mm, "radius": 2 * mm});
            skCircle(sketch, "E2.32.10.0", {"center": v(398.66, -162.1) * mm, "radius": 2 * mm});
            skCircle(sketch, "E2.32.11.0", {"center": v(398.66, -178.1) * mm, "radius": 2 * mm});
            skCircle(sketch, "E2.32.12.0", {"center": v(398.66, -194.1) * mm, "radius": 2 * mm});
            skCircle(sketch, "E2.32.13.0", {"center": v(398.66, -210.1) * mm, "radius": 2 * mm});
            skCircle(sketch, "E2.32.14.0", {"center": v(398.66, -226.1) * mm, "radius": 2 * mm});
            skCircle(sketch, "E2.32.15.0", {"center": v(398.66, -242.1) * mm, "radius": 2 * mm});
            skCircle(sketch, "E2.32.16.0", {"center": v(398.66, -258.1) * mm, "radius": 2 * mm});
            skCircle(sketch, "E2.32.17.0", {"center": v(398.66, -274.1) * mm, "radius": 2 * mm});
            skCircle(sketch, "E2.32.18.0", {"center": v(398.66, -290.1) * mm, "radius": 2 * mm});
            skCircle(sketch, "E2.32.19.0", {"center": v(398.66, -306.1) * mm, "radius": 2 * mm});
            skCircle(sketch, "E2.32.20.0", {"center": v(398.66, -322.1) * mm, "radius": 2 * mm});
            skCircle(sketch, "E2.32.21.0", {"center": v(398.66, -338.1) * mm, "radius": 2 * mm});
            skCircle(sketch, "E2.32.22.0", {"center": v(398.66, -354.1) * mm, "radius": 2 * mm});
            skCircle(sketch, "E2.32.23.0", {"center": v(398.66, -370.1) * mm, "radius": 2 * mm});
            skCircle(sketch, "E2.32.24.0", {"center": v(398.66, -386.1) * mm, "radius": 2 * mm});
            skCircle(sketch, "E2.32.25.0", {"center": v(398.66, -402.1) * mm, "radius": 2 * mm});
            skCircle(sketch, "E2.32.26.0", {"center": v(398.66, -418.1) * mm, "radius": 2 * mm});
            skCircle(sketch, "E2.32.27.0", {"center": v(398.66, -434.1) * mm, "radius": 2 * mm});
            skCircle(sketch, "E2.33.0.0", {"center": v(414.66, -2.1) * mm, "radius": 2 * mm});
            skCircle(sketch, "E2.33.1.0", {"center": v(414.66, -18.1) * mm, "radius": 2 * mm});
            skCircle(sketch, "E2.33.2.0", {"center": v(414.66, -34.1) * mm, "radius": 2 * mm});
            skCircle(sketch, "E2.33.3.0", {"center": v(414.66, -50.1) * mm, "radius": 2 * mm});
            skCircle(sketch, "E2.33.4.0", {"center": v(414.66, -66.1) * mm, "radius": 2 * mm});
            skCircle(sketch, "E2.33.5.0", {"center": v(414.66, -82.1) * mm, "radius": 2 * mm});
            skCircle(sketch, "E2.33.6.0", {"center": v(414.66, -98.1) * mm, "radius": 2 * mm});
            skCircle(sketch, "E2.33.7.0", {"center": v(414.66, -114.1) * mm, "radius": 2 * mm});
            skCircle(sketch, "E2.33.8.0", {"center": v(414.66, -130.1) * mm, "radius": 2 * mm});
            skCircle(sketch, "E2.33.9.0", {"center": v(414.66, -146.1) * mm, "radius": 2 * mm});
            skCircle(sketch, "E2.33.10.0", {"center": v(414.66, -162.1) * mm, "radius": 2 * mm});
            skCircle(sketch, "E2.33.11.0", {"center": v(414.66, -178.1) * mm, "radius": 2 * mm});
            skCircle(sketch, "E2.33.12.0", {"center": v(414.66, -194.1) * mm, "radius": 2 * mm});
            skCircle(sketch, "E2.33.13.0", {"center": v(414.66, -210.1) * mm, "radius": 2 * mm});
            skCircle(sketch, "E2.33.14.0", {"center": v(414.66, -226.1) * mm, "radius": 2 * mm});
            skCircle(sketch, "E2.33.15.0", {"center": v(414.66, -242.1) * mm, "radius": 2 * mm});
            skCircle(sketch, "E2.33.16.0", {"center": v(414.66, -258.1) * mm, "radius": 2 * mm});
            skCircle(sketch, "E2.33.17.0", {"center": v(414.66, -274.1) * mm, "radius": 2 * mm});
            skCircle(sketch, "E2.33.18.0", {"center": v(414.66, -290.1) * mm, "radius": 2 * mm});
            skCircle(sketch, "E2.33.19.0", {"center": v(414.66, -306.1) * mm, "radius": 2 * mm});
            skCircle(sketch, "E2.33.20.0", {"center": v(414.66, -322.1) * mm, "radius": 2 * mm});
            skCircle(sketch, "E2.33.21.0", {"center": v(414.66, -338.1) * mm, "radius": 2 * mm});
            skCircle(sketch, "E2.33.22.0", {"center": v(414.66, -354.1) * mm, "radius": 2 * mm});
            skCircle(sketch, "E2.33.23.0", {"center": v(414.66, -370.1) * mm, "radius": 2 * mm});
            skCircle(sketch, "E2.33.24.0", {"center": v(414.66, -386.1) * mm, "radius": 2 * mm});
            skCircle(sketch, "E2.33.25.0", {"center": v(414.66, -402.1) * mm, "radius": 2 * mm});
            skCircle(sketch, "E2.33.26.0", {"center": v(414.66, -418.1) * mm, "radius": 2 * mm});
            skCircle(sketch, "E2.33.27.0", {"center": v(414.66, -434.1) * mm, "radius": 2 * mm});
            skCircle(sketch, "E2.34.0.0", {"center": v(430.66, -2.1) * mm, "radius": 2 * mm});
            skCircle(sketch, "E2.34.1.0", {"center": v(430.66, -18.1) * mm, "radius": 2 * mm});
            skCircle(sketch, "E2.34.2.0", {"center": v(430.66, -34.1) * mm, "radius": 2 * mm});
            skCircle(sketch, "E2.34.3.0", {"center": v(430.66, -50.1) * mm, "radius": 2 * mm});
            skCircle(sketch, "E2.34.4.0", {"center": v(430.66, -66.1) * mm, "radius": 2 * mm});
            skCircle(sketch, "E2.34.5.0", {"center": v(430.66, -82.1) * mm, "radius": 2 * mm});
            skCircle(sketch, "E2.34.6.0", {"center": v(430.66, -98.1) * mm, "radius": 2 * mm});
            skCircle(sketch, "E2.34.7.0", {"center": v(430.66, -114.1) * mm, "radius": 2 * mm});
            skCircle(sketch, "E2.34.8.0", {"center": v(430.66, -130.1) * mm, "radius": 2 * mm});
            skCircle(sketch, "E2.34.9.0", {"center": v(430.66, -146.1) * mm, "radius": 2 * mm});
            skCircle(sketch, "E2.34.10.0", {"center": v(430.66, -162.1) * mm, "radius": 2 * mm});
            skCircle(sketch, "E2.34.11.0", {"center": v(430.66, -178.1) * mm, "radius": 2 * mm});
            skCircle(sketch, "E2.34.12.0", {"center": v(430.66, -194.1) * mm, "radius": 2 * mm});
            skCircle(sketch, "E2.34.13.0", {"center": v(430.66, -210.1) * mm, "radius": 2 * mm});
            skCircle(sketch, "E2.34.14.0", {"center": v(430.66, -226.1) * mm, "radius": 2 * mm});
            skCircle(sketch, "E2.34.15.0", {"center": v(430.66, -242.1) * mm, "radius": 2 * mm});
            skCircle(sketch, "E2.34.16.0", {"center": v(430.66, -258.1) * mm, "radius": 2 * mm});
            skCircle(sketch, "E2.34.17.0", {"center": v(430.66, -274.1) * mm, "radius": 2 * mm});
            skCircle(sketch, "E2.34.18.0", {"center": v(430.66, -290.1) * mm, "radius": 2 * mm});
            skCircle(sketch, "E2.34.19.0", {"center": v(430.66, -306.1) * mm, "radius": 2 * mm});
            skCircle(sketch, "E2.34.20.0", {"center": v(430.66, -322.1) * mm, "radius": 2 * mm});
            skCircle(sketch, "E2.34.21.0", {"center": v(430.66, -338.1) * mm, "radius": 2 * mm});
            skCircle(sketch, "E2.34.22.0", {"center": v(430.66, -354.1) * mm, "radius": 2 * mm});
            skCircle(sketch, "E2.34.23.0", {"center": v(430.66, -370.1) * mm, "radius": 2 * mm});
            skCircle(sketch, "E2.34.24.0", {"center": v(430.66, -386.1) * mm, "radius": 2 * mm});
            skCircle(sketch, "E2.34.25.0", {"center": v(430.66, -402.1) * mm, "radius": 2 * mm});
            skCircle(sketch, "E2.34.26.0", {"center": v(430.66, -418.1) * mm, "radius": 2 * mm});
            skCircle(sketch, "E2.34.27.0", {"center": v(430.66, -434.1) * mm, "radius": 2 * mm});
            skCircle(sketch, "E2.35.0.0", {"center": v(446.66, -2.1) * mm, "radius": 2 * mm});
            skCircle(sketch, "E2.35.1.0", {"center": v(446.66, -18.1) * mm, "radius": 2 * mm});
            skCircle(sketch, "E2.35.2.0", {"center": v(446.66, -34.1) * mm, "radius": 2 * mm});
            skCircle(sketch, "E2.35.3.0", {"center": v(446.66, -50.1) * mm, "radius": 2 * mm});
            skCircle(sketch, "E2.35.4.0", {"center": v(446.66, -66.1) * mm, "radius": 2 * mm});
            skCircle(sketch, "E2.35.5.0", {"center": v(446.66, -82.1) * mm, "radius": 2 * mm});
            skCircle(sketch, "E2.35.6.0", {"center": v(446.66, -98.1) * mm, "radius": 2 * mm});
            skCircle(sketch, "E2.35.7.0", {"center": v(446.66, -114.1) * mm, "radius": 2 * mm});
            skCircle(sketch, "E2.35.8.0", {"center": v(446.66, -130.1) * mm, "radius": 2 * mm});
            skCircle(sketch, "E2.35.9.0", {"center": v(446.66, -146.1) * mm, "radius": 2 * mm});
            skCircle(sketch, "E2.35.10.0", {"center": v(446.66, -162.1) * mm, "radius": 2 * mm});
            skCircle(sketch, "E2.35.11.0", {"center": v(446.66, -178.1) * mm, "radius": 2 * mm});
            skCircle(sketch, "E2.35.12.0", {"center": v(446.66, -194.1) * mm, "radius": 2 * mm});
            skCircle(sketch, "E2.35.13.0", {"center": v(446.66, -210.1) * mm, "radius": 2 * mm});
            skCircle(sketch, "E2.35.14.0", {"center": v(446.66, -226.1) * mm, "radius": 2 * mm});
            skCircle(sketch, "E2.35.15.0", {"center": v(446.66, -242.1) * mm, "radius": 2 * mm});
            skCircle(sketch, "E2.35.16.0", {"center": v(446.66, -258.1) * mm, "radius": 2 * mm});
            skCircle(sketch, "E2.35.17.0", {"center": v(446.66, -274.1) * mm, "radius": 2 * mm});
            skCircle(sketch, "E2.35.18.0", {"center": v(446.66, -290.1) * mm, "radius": 2 * mm});
            skCircle(sketch, "E2.35.19.0", {"center": v(446.66, -306.1) * mm, "radius": 2 * mm});
            skCircle(sketch, "E2.35.20.0", {"center": v(446.66, -322.1) * mm, "radius": 2 * mm});
            skCircle(sketch, "E2.35.21.0", {"center": v(446.66, -338.1) * mm, "radius": 2 * mm});
            skCircle(sketch, "E2.35.22.0", {"center": v(446.66, -354.1) * mm, "radius": 2 * mm});
            skCircle(sketch, "E2.35.23.0", {"center": v(446.66, -370.1) * mm, "radius": 2 * mm});
            skCircle(sketch, "E2.35.24.0", {"center": v(446.66, -386.1) * mm, "radius": 2 * mm});
            skCircle(sketch, "E2.35.25.0", {"center": v(446.66, -402.1) * mm, "radius": 2 * mm});
            skCircle(sketch, "E2.35.26.0", {"center": v(446.66, -418.1) * mm, "radius": 2 * mm});
            skCircle(sketch, "E2.35.27.0", {"center": v(446.66, -434.1) * mm, "radius": 2 * mm});
            skCircle(sketch, "E2.36.0.0", {"center": v(462.66, -2.1) * mm, "radius": 2 * mm});
            skCircle(sketch, "E2.36.1.0", {"center": v(462.66, -18.1) * mm, "radius": 2 * mm});
            skCircle(sketch, "E2.36.2.0", {"center": v(462.66, -34.1) * mm, "radius": 2 * mm});
            skCircle(sketch, "E2.36.3.0", {"center": v(462.66, -50.1) * mm, "radius": 2 * mm});
            skCircle(sketch, "E2.36.4.0", {"center": v(462.66, -66.1) * mm, "radius": 2 * mm});
            skCircle(sketch, "E2.36.5.0", {"center": v(462.66, -82.1) * mm, "radius": 2 * mm});
            skCircle(sketch, "E2.36.6.0", {"center": v(462.66, -98.1) * mm, "radius": 2 * mm});
            skCircle(sketch, "E2.36.7.0", {"center": v(462.66, -114.1) * mm, "radius": 2 * mm});
            skCircle(sketch, "E2.36.8.0", {"center": v(462.66, -130.1) * mm, "radius": 2 * mm});
            skCircle(sketch, "E2.36.9.0", {"center": v(462.66, -146.1) * mm, "radius": 2 * mm});
            skCircle(sketch, "E2.36.10.0", {"center": v(462.66, -162.1) * mm, "radius": 2 * mm});
            skCircle(sketch, "E2.36.11.0", {"center": v(462.66, -178.1) * mm, "radius": 2 * mm});
            skCircle(sketch, "E2.36.12.0", {"center": v(462.66, -194.1) * mm, "radius": 2 * mm});
            skCircle(sketch, "E2.36.13.0", {"center": v(462.66, -210.1) * mm, "radius": 2 * mm});
            skCircle(sketch, "E2.36.14.0", {"center": v(462.66, -226.1) * mm, "radius": 2 * mm});
            skCircle(sketch, "E2.36.15.0", {"center": v(462.66, -242.1) * mm, "radius": 2 * mm});
            skCircle(sketch, "E2.36.16.0", {"center": v(462.66, -258.1) * mm, "radius": 2 * mm});
            skCircle(sketch, "E2.36.17.0", {"center": v(462.66, -274.1) * mm, "radius": 2 * mm});
            skCircle(sketch, "E2.36.18.0", {"center": v(462.66, -290.1) * mm, "radius": 2 * mm});
            skCircle(sketch, "E2.36.19.0", {"center": v(462.66, -306.1) * mm, "radius": 2 * mm});
            skCircle(sketch, "E2.36.20.0", {"center": v(462.66, -322.1) * mm, "radius": 2 * mm});
            skCircle(sketch, "E2.36.21.0", {"center": v(462.66, -338.1) * mm, "radius": 2 * mm});
            skCircle(sketch, "E2.36.22.0", {"center": v(462.66, -354.1) * mm, "radius": 2 * mm});
            skCircle(sketch, "E2.36.23.0", {"center": v(462.66, -370.1) * mm, "radius": 2 * mm});
            skCircle(sketch, "E2.36.24.0", {"center": v(462.66, -386.1) * mm, "radius": 2 * mm});
            skCircle(sketch, "E2.36.25.0", {"center": v(462.66, -402.1) * mm, "radius": 2 * mm});
            skCircle(sketch, "E2.36.26.0", {"center": v(462.66, -418.1) * mm, "radius": 2 * mm});
            skCircle(sketch, "E2.36.27.0", {"center": v(462.66, -434.1) * mm, "radius": 2 * mm});
            skCircle(sketch, "E2.37.0.0", {"center": v(478.66, -2.1) * mm, "radius": 2 * mm});
            skCircle(sketch, "E2.37.1.0", {"center": v(478.66, -18.1) * mm, "radius": 2 * mm});
            skCircle(sketch, "E2.37.2.0", {"center": v(478.66, -34.1) * mm, "radius": 2 * mm});
            skCircle(sketch, "E2.37.3.0", {"center": v(478.66, -50.1) * mm, "radius": 2 * mm});
            skCircle(sketch, "E2.37.4.0", {"center": v(478.66, -66.1) * mm, "radius": 2 * mm});
            skCircle(sketch, "E2.37.5.0", {"center": v(478.66, -82.1) * mm, "radius": 2 * mm});
            skCircle(sketch, "E2.37.6.0", {"center": v(478.66, -98.1) * mm, "radius": 2 * mm});
            skCircle(sketch, "E2.37.7.0", {"center": v(478.66, -114.1) * mm, "radius": 2 * mm});
            skCircle(sketch, "E2.37.8.0", {"center": v(478.66, -130.1) * mm, "radius": 2 * mm});
            skCircle(sketch, "E2.37.9.0", {"center": v(478.66, -146.1) * mm, "radius": 2 * mm});
            skCircle(sketch, "E2.37.10.0", {"center": v(478.66, -162.1) * mm, "radius": 2 * mm});
            skCircle(sketch, "E2.37.11.0", {"center": v(478.66, -178.1) * mm, "radius": 2 * mm});
            skCircle(sketch, "E2.37.12.0", {"center": v(478.66, -194.1) * mm, "radius": 2 * mm});
            skCircle(sketch, "E2.37.13.0", {"center": v(478.66, -210.1) * mm, "radius": 2 * mm});
            skCircle(sketch, "E2.37.14.0", {"center": v(478.66, -226.1) * mm, "radius": 2 * mm});
            skCircle(sketch, "E2.37.15.0", {"center": v(478.66, -242.1) * mm, "radius": 2 * mm});
            skCircle(sketch, "E2.37.16.0", {"center": v(478.66, -258.1) * mm, "radius": 2 * mm});
            skCircle(sketch, "E2.37.17.0", {"center": v(478.66, -274.1) * mm, "radius": 2 * mm});
            skCircle(sketch, "E2.37.18.0", {"center": v(478.66, -290.1) * mm, "radius": 2 * mm});
            skCircle(sketch, "E2.37.19.0", {"center": v(478.66, -306.1) * mm, "radius": 2 * mm});
            skCircle(sketch, "E2.37.20.0", {"center": v(478.66, -322.1) * mm, "radius": 2 * mm});
            skCircle(sketch, "E2.37.21.0", {"center": v(478.66, -338.1) * mm, "radius": 2 * mm});
            skCircle(sketch, "E2.37.22.0", {"center": v(478.66, -354.1) * mm, "radius": 2 * mm});
            skCircle(sketch, "E2.37.23.0", {"center": v(478.66, -370.1) * mm, "radius": 2 * mm});
            skCircle(sketch, "E2.37.24.0", {"center": v(478.66, -386.1) * mm, "radius": 2 * mm});
            skCircle(sketch, "E2.37.25.0", {"center": v(478.66, -402.1) * mm, "radius": 2 * mm});
            skCircle(sketch, "E2.37.26.0", {"center": v(478.66, -418.1) * mm, "radius": 2 * mm});
            skCircle(sketch, "E2.37.27.0", {"center": v(478.66, -434.1) * mm, "radius": 2 * mm});
            skCircle(sketch, "E2.38.0.0", {"center": v(494.66, -2.1) * mm, "radius": 2 * mm});
            skCircle(sketch, "E2.38.1.0", {"center": v(494.66, -18.1) * mm, "radius": 2 * mm});
            skCircle(sketch, "E2.38.2.0", {"center": v(494.66, -34.1) * mm, "radius": 2 * mm});
            skCircle(sketch, "E2.38.3.0", {"center": v(494.66, -50.1) * mm, "radius": 2 * mm});
            skCircle(sketch, "E2.38.4.0", {"center": v(494.66, -66.1) * mm, "radius": 2 * mm});
            skCircle(sketch, "E2.38.5.0", {"center": v(494.66, -82.1) * mm, "radius": 2 * mm});
            skCircle(sketch, "E2.38.6.0", {"center": v(494.66, -98.1) * mm, "radius": 2 * mm});
            skCircle(sketch, "E2.38.7.0", {"center": v(494.66, -114.1) * mm, "radius": 2 * mm});
            skCircle(sketch, "E2.38.8.0", {"center": v(494.66, -130.1) * mm, "radius": 2 * mm});
            skCircle(sketch, "E2.38.9.0", {"center": v(494.66, -146.1) * mm, "radius": 2 * mm});
            skCircle(sketch, "E2.38.10.0", {"center": v(494.66, -162.1) * mm, "radius": 2 * mm});
            skCircle(sketch, "E2.38.11.0", {"center": v(494.66, -178.1) * mm, "radius": 2 * mm});
            skCircle(sketch, "E2.38.12.0", {"center": v(494.66, -194.1) * mm, "radius": 2 * mm});
            skCircle(sketch, "E2.38.13.0", {"center": v(494.66, -210.1) * mm, "radius": 2 * mm});
            skCircle(sketch, "E2.38.14.0", {"center": v(494.66, -226.1) * mm, "radius": 2 * mm});
            skCircle(sketch, "E2.38.15.0", {"center": v(494.66, -242.1) * mm, "radius": 2 * mm});
            skCircle(sketch, "E2.38.16.0", {"center": v(494.66, -258.1) * mm, "radius": 2 * mm});
            skCircle(sketch, "E2.38.17.0", {"center": v(494.66, -274.1) * mm, "radius": 2 * mm});
            skCircle(sketch, "E2.38.18.0", {"center": v(494.66, -290.1) * mm, "radius": 2 * mm});
            skCircle(sketch, "E2.38.19.0", {"center": v(494.66, -306.1) * mm, "radius": 2 * mm});
            skCircle(sketch, "E2.38.20.0", {"center": v(494.66, -322.1) * mm, "radius": 2 * mm});
            skCircle(sketch, "E2.38.21.0", {"center": v(494.66, -338.1) * mm, "radius": 2 * mm});
            skCircle(sketch, "E2.38.22.0", {"center": v(494.66, -354.1) * mm, "radius": 2 * mm});
            skCircle(sketch, "E2.38.23.0", {"center": v(494.66, -370.1) * mm, "radius": 2 * mm});
            skCircle(sketch, "E2.38.24.0", {"center": v(494.66, -386.1) * mm, "radius": 2 * mm});
            skCircle(sketch, "E2.38.25.0", {"center": v(494.66, -402.1) * mm, "radius": 2 * mm});
            skCircle(sketch, "E2.38.26.0", {"center": v(494.66, -418.1) * mm, "radius": 2 * mm});
            skCircle(sketch, "E2.38.27.0", {"center": v(494.66, -434.1) * mm, "radius": 2 * mm});
            skCircle(sketch, "E2.39.0.0", {"center": v(510.66, -2.1) * mm, "radius": 2 * mm});
            skCircle(sketch, "E2.39.1.0", {"center": v(510.66, -18.1) * mm, "radius": 2 * mm});
            skCircle(sketch, "E2.39.2.0", {"center": v(510.66, -34.1) * mm, "radius": 2 * mm});
            skCircle(sketch, "E2.39.3.0", {"center": v(510.66, -50.1) * mm, "radius": 2 * mm});
            skCircle(sketch, "E2.39.4.0", {"center": v(510.66, -66.1) * mm, "radius": 2 * mm});
            skCircle(sketch, "E2.39.5.0", {"center": v(510.66, -82.1) * mm, "radius": 2 * mm});
            skCircle(sketch, "E2.39.6.0", {"center": v(510.66, -98.1) * mm, "radius": 2 * mm});
            skCircle(sketch, "E2.39.7.0", {"center": v(510.66, -114.1) * mm, "radius": 2 * mm});
            skCircle(sketch, "E2.39.8.0", {"center": v(510.66, -130.1) * mm, "radius": 2 * mm});
            skCircle(sketch, "E2.39.9.0", {"center": v(510.66, -146.1) * mm, "radius": 2 * mm});
            skCircle(sketch, "E2.39.10.0", {"center": v(510.66, -162.1) * mm, "radius": 2 * mm});
            skCircle(sketch, "E2.39.11.0", {"center": v(510.66, -178.1) * mm, "radius": 2 * mm});
            skCircle(sketch, "E2.39.12.0", {"center": v(510.66, -194.1) * mm, "radius": 2 * mm});
            skCircle(sketch, "E2.39.13.0", {"center": v(510.66, -210.1) * mm, "radius": 2 * mm});
            skCircle(sketch, "E2.39.14.0", {"center": v(510.66, -226.1) * mm, "radius": 2 * mm});
            skCircle(sketch, "E2.39.15.0", {"center": v(510.66, -242.1) * mm, "radius": 2 * mm});
            skCircle(sketch, "E2.39.16.0", {"center": v(510.66, -258.1) * mm, "radius": 2 * mm});
            skCircle(sketch, "E2.39.17.0", {"center": v(510.66, -274.1) * mm, "radius": 2 * mm});
            skCircle(sketch, "E2.39.18.0", {"center": v(510.66, -290.1) * mm, "radius": 2 * mm});
            skCircle(sketch, "E2.39.19.0", {"center": v(510.66, -306.1) * mm, "radius": 2 * mm});
            skCircle(sketch, "E2.39.20.0", {"center": v(510.66, -322.1) * mm, "radius": 2 * mm});
            skCircle(sketch, "E2.39.21.0", {"center": v(510.66, -338.1) * mm, "radius": 2 * mm});
            skCircle(sketch, "E2.39.22.0", {"center": v(510.66, -354.1) * mm, "radius": 2 * mm});
            skCircle(sketch, "E2.39.23.0", {"center": v(510.66, -370.1) * mm, "radius": 2 * mm});
            skCircle(sketch, "E2.39.24.0", {"center": v(510.66, -386.1) * mm, "radius": 2 * mm});
            skCircle(sketch, "E2.39.25.0", {"center": v(510.66, -402.1) * mm, "radius": 2 * mm});
            skCircle(sketch, "E2.39.26.0", {"center": v(510.66, -418.1) * mm, "radius": 2 * mm});
            skCircle(sketch, "E2.39.27.0", {"center": v(510.66, -434.1) * mm, "radius": 2 * mm});
            skLineSegment(sketch, "E2.direction1", {"start": v(-113.34, -2.1) * mm, "end": v(-97.34, -2.1) * mm, "construction": true});
            skLineSegment(sketch, "E2.direction2", {"start": v(-113.34, -2.1) * mm, "end": v(-113.34, -18.1) * mm, "construction": true});
            skCircle(sketch, "E3", {"center": v(-105.34, -10.1) * mm, "radius": 2 * mm});
            skCircle(sketch, "E4.0.1.0", {"center": v(-105.34, -26.1) * mm, "radius": 2 * mm});
            skCircle(sketch, "E4.0.2.0", {"center": v(-105.34, -42.1) * mm, "radius": 2 * mm});
            skCircle(sketch, "E4.0.3.0", {"center": v(-105.34, -58.1) * mm, "radius": 2 * mm});
            skCircle(sketch, "E4.0.4.0", {"center": v(-105.34, -74.1) * mm, "radius": 2 * mm});
            skCircle(sketch, "E4.0.5.0", {"center": v(-105.34, -90.1) * mm, "radius": 2 * mm});
            skCircle(sketch, "E4.0.6.0", {"center": v(-105.34, -106.1) * mm, "radius": 2 * mm});
            skCircle(sketch, "E4.0.7.0", {"center": v(-105.34, -122.1) * mm, "radius": 2 * mm});
            skCircle(sketch, "E4.0.8.0", {"center": v(-105.34, -138.1) * mm, "radius": 2 * mm});
            skCircle(sketch, "E4.0.9.0", {"center": v(-105.34, -154.1) * mm, "radius": 2 * mm});
            skCircle(sketch, "E4.0.10.0", {"center": v(-105.34, -170.1) * mm, "radius": 2 * mm});
            skCircle(sketch, "E4.0.11.0", {"center": v(-105.34, -186.1) * mm, "radius": 2 * mm});
            skCircle(sketch, "E4.0.12.0", {"center": v(-105.34, -202.1) * mm, "radius": 2 * mm});
            skCircle(sketch, "E4.0.13.0", {"center": v(-105.34, -218.1) * mm, "radius": 2 * mm});
            skCircle(sketch, "E4.0.14.0", {"center": v(-105.34, -234.1) * mm, "radius": 2 * mm});
            skCircle(sketch, "E4.0.15.0", {"center": v(-105.34, -250.1) * mm, "radius": 2 * mm});
            skCircle(sketch, "E4.0.16.0", {"center": v(-105.34, -266.1) * mm, "radius": 2 * mm});
            skCircle(sketch, "E4.0.17.0", {"center": v(-105.34, -282.1) * mm, "radius": 2 * mm});
            skCircle(sketch, "E4.0.18.0", {"center": v(-105.34, -298.1) * mm, "radius": 2 * mm});
            skCircle(sketch, "E4.0.19.0", {"center": v(-105.34, -314.1) * mm, "radius": 2 * mm});
            skCircle(sketch, "E4.0.20.0", {"center": v(-105.34, -330.1) * mm, "radius": 2 * mm});
            skCircle(sketch, "E4.0.21.0", {"center": v(-105.34, -346.1) * mm, "radius": 2 * mm});
            skCircle(sketch, "E4.0.22.0", {"center": v(-105.34, -362.1) * mm, "radius": 2 * mm});
            skCircle(sketch, "E4.0.23.0", {"center": v(-105.34, -378.1) * mm, "radius": 2 * mm});
            skCircle(sketch, "E4.0.24.0", {"center": v(-105.34, -394.1) * mm, "radius": 2 * mm});
            skCircle(sketch, "E4.0.25.0", {"center": v(-105.34, -410.1) * mm, "radius": 2 * mm});
            skCircle(sketch, "E4.0.26.0", {"center": v(-105.34, -426.1) * mm, "radius": 2 * mm});
            skCircle(sketch, "E4.0.27.0", {"center": v(-105.34, -442.1) * mm, "radius": 2 * mm});
            skCircle(sketch, "E4.1.0.0", {"center": v(-89.34, -10.1) * mm, "radius": 2 * mm});
            skCircle(sketch, "E4.1.1.0", {"center": v(-89.34, -26.1) * mm, "radius": 2 * mm});
            skCircle(sketch, "E4.1.2.0", {"center": v(-89.34, -42.1) * mm, "radius": 2 * mm});
            skCircle(sketch, "E4.1.3.0", {"center": v(-89.34, -58.1) * mm, "radius": 2 * mm});
            skCircle(sketch, "E4.1.4.0", {"center": v(-89.34, -74.1) * mm, "radius": 2 * mm});
            skCircle(sketch, "E4.1.5.0", {"center": v(-89.34, -90.1) * mm, "radius": 2 * mm});
            skCircle(sketch, "E4.1.6.0", {"center": v(-89.34, -106.1) * mm, "radius": 2 * mm});
            skCircle(sketch, "E4.1.7.0", {"center": v(-89.34, -122.1) * mm, "radius": 2 * mm});
            skCircle(sketch, "E4.1.8.0", {"center": v(-89.34, -138.1) * mm, "radius": 2 * mm});
            skCircle(sketch, "E4.1.9.0", {"center": v(-89.34, -154.1) * mm, "radius": 2 * mm});
            skCircle(sketch, "E4.1.10.0", {"center": v(-89.34, -170.1) * mm, "radius": 2 * mm});
            skCircle(sketch, "E4.1.11.0", {"center": v(-89.34, -186.1) * mm, "radius": 2 * mm});
            skCircle(sketch, "E4.1.12.0", {"center": v(-89.34, -202.1) * mm, "radius": 2 * mm});
            skCircle(sketch, "E4.1.13.0", {"center": v(-89.34, -218.1) * mm, "radius": 2 * mm});
            skCircle(sketch, "E4.1.14.0", {"center": v(-89.34, -234.1) * mm, "radius": 2 * mm});
            skCircle(sketch, "E4.1.15.0", {"center": v(-89.34, -250.1) * mm, "radius": 2 * mm});
            skCircle(sketch, "E4.1.16.0", {"center": v(-89.34, -266.1) * mm, "radius": 2 * mm});
            skCircle(sketch, "E4.1.17.0", {"center": v(-89.34, -282.1) * mm, "radius": 2 * mm});
            skCircle(sketch, "E4.1.18.0", {"center": v(-89.34, -298.1) * mm, "radius": 2 * mm});
            skCircle(sketch, "E4.1.19.0", {"center": v(-89.34, -314.1) * mm, "radius": 2 * mm});
            skCircle(sketch, "E4.1.20.0", {"center": v(-89.34, -330.1) * mm, "radius": 2 * mm});
            skCircle(sketch, "E4.1.21.0", {"center": v(-89.34, -346.1) * mm, "radius": 2 * mm});
            skCircle(sketch, "E4.1.22.0", {"center": v(-89.34, -362.1) * mm, "radius": 2 * mm});
            skCircle(sketch, "E4.1.23.0", {"center": v(-89.34, -378.1) * mm, "radius": 2 * mm});
            skCircle(sketch, "E4.1.24.0", {"center": v(-89.34, -394.1) * mm, "radius": 2 * mm});
            skCircle(sketch, "E4.1.25.0", {"center": v(-89.34, -410.1) * mm, "radius": 2 * mm});
            skCircle(sketch, "E4.1.26.0", {"center": v(-89.34, -426.1) * mm, "radius": 2 * mm});
            skCircle(sketch, "E4.1.27.0", {"center": v(-89.34, -442.1) * mm, "radius": 2 * mm});
            skCircle(sketch, "E4.2.0.0", {"center": v(-73.34, -10.1) * mm, "radius": 2 * mm});
            skCircle(sketch, "E4.2.1.0", {"center": v(-73.34, -26.1) * mm, "radius": 2 * mm});
            skCircle(sketch, "E4.2.2.0", {"center": v(-73.34, -42.1) * mm, "radius": 2 * mm});
            skCircle(sketch, "E4.2.3.0", {"center": v(-73.34, -58.1) * mm, "radius": 2 * mm});
            skCircle(sketch, "E4.2.4.0", {"center": v(-73.34, -74.1) * mm, "radius": 2 * mm});
            skCircle(sketch, "E4.2.5.0", {"center": v(-73.34, -90.1) * mm, "radius": 2 * mm});
            skCircle(sketch, "E4.2.6.0", {"center": v(-73.34, -106.1) * mm, "radius": 2 * mm});
            skCircle(sketch, "E4.2.7.0", {"center": v(-73.34, -122.1) * mm, "radius": 2 * mm});
            skCircle(sketch, "E4.2.8.0", {"center": v(-73.34, -138.1) * mm, "radius": 2 * mm});
            skCircle(sketch, "E4.2.9.0", {"center": v(-73.34, -154.1) * mm, "radius": 2 * mm});
            skCircle(sketch, "E4.2.10.0", {"center": v(-73.34, -170.1) * mm, "radius": 2 * mm});
            skCircle(sketch, "E4.2.11.0", {"center": v(-73.34, -186.1) * mm, "radius": 2 * mm});
            skCircle(sketch, "E4.2.12.0", {"center": v(-73.34, -202.1) * mm, "radius": 2 * mm});
            skCircle(sketch, "E4.2.13.0", {"center": v(-73.34, -218.1) * mm, "radius": 2 * mm});
            skCircle(sketch, "E4.2.14.0", {"center": v(-73.34, -234.1) * mm, "radius": 2 * mm});
            skCircle(sketch, "E4.2.15.0", {"center": v(-73.34, -250.1) * mm, "radius": 2 * mm});
            skCircle(sketch, "E4.2.16.0", {"center": v(-73.34, -266.1) * mm, "radius": 2 * mm});
            skCircle(sketch, "E4.2.17.0", {"center": v(-73.34, -282.1) * mm, "radius": 2 * mm});
            skCircle(sketch, "E4.2.18.0", {"center": v(-73.34, -298.1) * mm, "radius": 2 * mm});
            skCircle(sketch, "E4.2.19.0", {"center": v(-73.34, -314.1) * mm, "radius": 2 * mm});
            skCircle(sketch, "E4.2.20.0", {"center": v(-73.34, -330.1) * mm, "radius": 2 * mm});
            skCircle(sketch, "E4.2.21.0", {"center": v(-73.34, -346.1) * mm, "radius": 2 * mm});
            skCircle(sketch, "E4.2.22.0", {"center": v(-73.34, -362.1) * mm, "radius": 2 * mm});
            skCircle(sketch, "E4.2.23.0", {"center": v(-73.34, -378.1) * mm, "radius": 2 * mm});
            skCircle(sketch, "E4.2.24.0", {"center": v(-73.34, -394.1) * mm, "radius": 2 * mm});
            skCircle(sketch, "E4.2.25.0", {"center": v(-73.34, -410.1) * mm, "radius": 2 * mm});
            skCircle(sketch, "E4.2.26.0", {"center": v(-73.34, -426.1) * mm, "radius": 2 * mm});
            skCircle(sketch, "E4.2.27.0", {"center": v(-73.34, -442.1) * mm, "radius": 2 * mm});
            skCircle(sketch, "E4.3.0.0", {"center": v(-57.34, -10.1) * mm, "radius": 2 * mm});
            skCircle(sketch, "E4.3.1.0", {"center": v(-57.34, -26.1) * mm, "radius": 2 * mm});
            skCircle(sketch, "E4.3.2.0", {"center": v(-57.34, -42.1) * mm, "radius": 2 * mm});
            skCircle(sketch, "E4.3.3.0", {"center": v(-57.34, -58.1) * mm, "radius": 2 * mm});
            skCircle(sketch, "E4.3.4.0", {"center": v(-57.34, -74.1) * mm, "radius": 2 * mm});
            skCircle(sketch, "E4.3.5.0", {"center": v(-57.34, -90.1) * mm, "radius": 2 * mm});
            skCircle(sketch, "E4.3.6.0", {"center": v(-57.34, -106.1) * mm, "radius": 2 * mm});
            skCircle(sketch, "E4.3.7.0", {"center": v(-57.34, -122.1) * mm, "radius": 2 * mm});
            skCircle(sketch, "E4.3.8.0", {"center": v(-57.34, -138.1) * mm, "radius": 2 * mm});
            skCircle(sketch, "E4.3.9.0", {"center": v(-57.34, -154.1) * mm, "radius": 2 * mm});
            skCircle(sketch, "E4.3.10.0", {"center": v(-57.34, -170.1) * mm, "radius": 2 * mm});
            skCircle(sketch, "E4.3.11.0", {"center": v(-57.34, -186.1) * mm, "radius": 2 * mm});
            skCircle(sketch, "E4.3.12.0", {"center": v(-57.34, -202.1) * mm, "radius": 2 * mm});
            skCircle(sketch, "E4.3.13.0", {"center": v(-57.34, -218.1) * mm, "radius": 2 * mm});
            skCircle(sketch, "E4.3.14.0", {"center": v(-57.34, -234.1) * mm, "radius": 2 * mm});
            skCircle(sketch, "E4.3.15.0", {"center": v(-57.34, -250.1) * mm, "radius": 2 * mm});
            skCircle(sketch, "E4.3.16.0", {"center": v(-57.34, -266.1) * mm, "radius": 2 * mm});
            skCircle(sketch, "E4.3.17.0", {"center": v(-57.34, -282.1) * mm, "radius": 2 * mm});
            skCircle(sketch, "E4.3.18.0", {"center": v(-57.34, -298.1) * mm, "radius": 2 * mm});
            skCircle(sketch, "E4.3.19.0", {"center": v(-57.34, -314.1) * mm, "radius": 2 * mm});
            skCircle(sketch, "E4.3.20.0", {"center": v(-57.34, -330.1) * mm, "radius": 2 * mm});
            skCircle(sketch, "E4.3.21.0", {"center": v(-57.34, -346.1) * mm, "radius": 2 * mm});
            skCircle(sketch, "E4.3.22.0", {"center": v(-57.34, -362.1) * mm, "radius": 2 * mm});
            skCircle(sketch, "E4.3.23.0", {"center": v(-57.34, -378.1) * mm, "radius": 2 * mm});
            skCircle(sketch, "E4.3.24.0", {"center": v(-57.34, -394.1) * mm, "radius": 2 * mm});
            skCircle(sketch, "E4.3.25.0", {"center": v(-57.34, -410.1) * mm, "radius": 2 * mm});
            skCircle(sketch, "E4.3.26.0", {"center": v(-57.34, -426.1) * mm, "radius": 2 * mm});
            skCircle(sketch, "E4.3.27.0", {"center": v(-57.34, -442.1) * mm, "radius": 2 * mm});
            skCircle(sketch, "E4.4.0.0", {"center": v(-41.34, -10.1) * mm, "radius": 2 * mm});
            skCircle(sketch, "E4.4.1.0", {"center": v(-41.34, -26.1) * mm, "radius": 2 * mm});
            skCircle(sketch, "E4.4.2.0", {"center": v(-41.34, -42.1) * mm, "radius": 2 * mm});
            skCircle(sketch, "E4.4.3.0", {"center": v(-41.34, -58.1) * mm, "radius": 2 * mm});
            skCircle(sketch, "E4.4.4.0", {"center": v(-41.34, -74.1) * mm, "radius": 2 * mm});
            skCircle(sketch, "E4.4.5.0", {"center": v(-41.34, -90.1) * mm, "radius": 2 * mm});
            skCircle(sketch, "E4.4.6.0", {"center": v(-41.34, -106.1) * mm, "radius": 2 * mm});
            skCircle(sketch, "E4.4.7.0", {"center": v(-41.34, -122.1) * mm, "radius": 2 * mm});
            skCircle(sketch, "E4.4.8.0", {"center": v(-41.34, -138.1) * mm, "radius": 2 * mm});
            skCircle(sketch, "E4.4.9.0", {"center": v(-41.34, -154.1) * mm, "radius": 2 * mm});
            skCircle(sketch, "E4.4.10.0", {"center": v(-41.34, -170.1) * mm, "radius": 2 * mm});
            skCircle(sketch, "E4.4.11.0", {"center": v(-41.34, -186.1) * mm, "radius": 2 * mm});
            skCircle(sketch, "E4.4.12.0", {"center": v(-41.34, -202.1) * mm, "radius": 2 * mm});
            skCircle(sketch, "E4.4.13.0", {"center": v(-41.34, -218.1) * mm, "radius": 2 * mm});
            skCircle(sketch, "E4.4.14.0", {"center": v(-41.34, -234.1) * mm, "radius": 2 * mm});
            skCircle(sketch, "E4.4.15.0", {"center": v(-41.34, -250.1) * mm, "radius": 2 * mm});
            skCircle(sketch, "E4.4.16.0", {"center": v(-41.34, -266.1) * mm, "radius": 2 * mm});
            skCircle(sketch, "E4.4.17.0", {"center": v(-41.34, -282.1) * mm, "radius": 2 * mm});
            skCircle(sketch, "E4.4.18.0", {"center": v(-41.34, -298.1) * mm, "radius": 2 * mm});
            skCircle(sketch, "E4.4.19.0", {"center": v(-41.34, -314.1) * mm, "radius": 2 * mm});
            skCircle(sketch, "E4.4.20.0", {"center": v(-41.34, -330.1) * mm, "radius": 2 * mm});
            skCircle(sketch, "E4.4.21.0", {"center": v(-41.34, -346.1) * mm, "radius": 2 * mm});
            skCircle(sketch, "E4.4.22.0", {"center": v(-41.34, -362.1) * mm, "radius": 2 * mm});
            skCircle(sketch, "E4.4.23.0", {"center": v(-41.34, -378.1) * mm, "radius": 2 * mm});
            skCircle(sketch, "E4.4.24.0", {"center": v(-41.34, -394.1) * mm, "radius": 2 * mm});
            skCircle(sketch, "E4.4.25.0", {"center": v(-41.34, -410.1) * mm, "radius": 2 * mm});
            skCircle(sketch, "E4.4.26.0", {"center": v(-41.34, -426.1) * mm, "radius": 2 * mm});
            skCircle(sketch, "E4.4.27.0", {"center": v(-41.34, -442.1) * mm, "radius": 2 * mm});
            skCircle(sketch, "E4.5.0.0", {"center": v(-25.34, -10.1) * mm, "radius": 2 * mm});
            skCircle(sketch, "E4.5.1.0", {"center": v(-25.34, -26.1) * mm, "radius": 2 * mm});
            skCircle(sketch, "E4.5.2.0", {"center": v(-25.34, -42.1) * mm, "radius": 2 * mm});
            skCircle(sketch, "E4.5.3.0", {"center": v(-25.34, -58.1) * mm, "radius": 2 * mm});
            skCircle(sketch, "E4.5.4.0", {"center": v(-25.34, -74.1) * mm, "radius": 2 * mm});
            skCircle(sketch, "E4.5.5.0", {"center": v(-25.34, -90.1) * mm, "radius": 2 * mm});
            skCircle(sketch, "E4.5.6.0", {"center": v(-25.34, -106.1) * mm, "radius": 2 * mm});
            skCircle(sketch, "E4.5.7.0", {"center": v(-25.34, -122.1) * mm, "radius": 2 * mm});
            skCircle(sketch, "E4.5.8.0", {"center": v(-25.34, -138.1) * mm, "radius": 2 * mm});
            skCircle(sketch, "E4.5.9.0", {"center": v(-25.34, -154.1) * mm, "radius": 2 * mm});
            skCircle(sketch, "E4.5.10.0", {"center": v(-25.34, -170.1) * mm, "radius": 2 * mm});
            skCircle(sketch, "E4.5.11.0", {"center": v(-25.34, -186.1) * mm, "radius": 2 * mm});
            skCircle(sketch, "E4.5.12.0", {"center": v(-25.34, -202.1) * mm, "radius": 2 * mm});
            skCircle(sketch, "E4.5.13.0", {"center": v(-25.34, -218.1) * mm, "radius": 2 * mm});
            skCircle(sketch, "E4.5.14.0", {"center": v(-25.34, -234.1) * mm, "radius": 2 * mm});
            skCircle(sketch, "E4.5.15.0", {"center": v(-25.34, -250.1) * mm, "radius": 2 * mm});
            skCircle(sketch, "E4.5.16.0", {"center": v(-25.34, -266.1) * mm, "radius": 2 * mm});
            skCircle(sketch, "E4.5.17.0", {"center": v(-25.34, -282.1) * mm, "radius": 2 * mm});
            skCircle(sketch, "E4.5.18.0", {"center": v(-25.34, -298.1) * mm, "radius": 2 * mm});
            skCircle(sketch, "E4.5.19.0", {"center": v(-25.34, -314.1) * mm, "radius": 2 * mm});
            skCircle(sketch, "E4.5.20.0", {"center": v(-25.34, -330.1) * mm, "radius": 2 * mm});
            skCircle(sketch, "E4.5.21.0", {"center": v(-25.34, -346.1) * mm, "radius": 2 * mm});
            skCircle(sketch, "E4.5.22.0", {"center": v(-25.34, -362.1) * mm, "radius": 2 * mm});
            skCircle(sketch, "E4.5.23.0", {"center": v(-25.34, -378.1) * mm, "radius": 2 * mm});
            skCircle(sketch, "E4.5.24.0", {"center": v(-25.34, -394.1) * mm, "radius": 2 * mm});
            skCircle(sketch, "E4.5.25.0", {"center": v(-25.34, -410.1) * mm, "radius": 2 * mm});
            skCircle(sketch, "E4.5.26.0", {"center": v(-25.34, -426.1) * mm, "radius": 2 * mm});
            skCircle(sketch, "E4.5.27.0", {"center": v(-25.34, -442.1) * mm, "radius": 2 * mm});
            skCircle(sketch, "E4.6.0.0", {"center": v(-9.34, -10.1) * mm, "radius": 2 * mm});
            skCircle(sketch, "E4.6.1.0", {"center": v(-9.34, -26.1) * mm, "radius": 2 * mm});
            skCircle(sketch, "E4.6.2.0", {"center": v(-9.34, -42.1) * mm, "radius": 2 * mm});
            skCircle(sketch, "E4.6.3.0", {"center": v(-9.34, -58.1) * mm, "radius": 2 * mm});
            skCircle(sketch, "E4.6.4.0", {"center": v(-9.34, -74.1) * mm, "radius": 2 * mm});
            skCircle(sketch, "E4.6.5.0", {"center": v(-9.34, -90.1) * mm, "radius": 2 * mm});
            skCircle(sketch, "E4.6.6.0", {"center": v(-9.34, -106.1) * mm, "radius": 2 * mm});
            skCircle(sketch, "E4.6.7.0", {"center": v(-9.34, -122.1) * mm, "radius": 2 * mm});
            skCircle(sketch, "E4.6.8.0", {"center": v(-9.34, -138.1) * mm, "radius": 2 * mm});
            skCircle(sketch, "E4.6.9.0", {"center": v(-9.34, -154.1) * mm, "radius": 2 * mm});
            skCircle(sketch, "E4.6.10.0", {"center": v(-9.34, -170.1) * mm, "radius": 2 * mm});
            skCircle(sketch, "E4.6.11.0", {"center": v(-9.34, -186.1) * mm, "radius": 2 * mm});
            skCircle(sketch, "E4.6.12.0", {"center": v(-9.34, -202.1) * mm, "radius": 2 * mm});
            skCircle(sketch, "E4.6.13.0", {"center": v(-9.34, -218.1) * mm, "radius": 2 * mm});
            skCircle(sketch, "E4.6.14.0", {"center": v(-9.34, -234.1) * mm, "radius": 2 * mm});
            skCircle(sketch, "E4.6.15.0", {"center": v(-9.34, -250.1) * mm, "radius": 2 * mm});
            skCircle(sketch, "E4.6.16.0", {"center": v(-9.34, -266.1) * mm, "radius": 2 * mm});
            skCircle(sketch, "E4.6.17.0", {"center": v(-9.34, -282.1) * mm, "radius": 2 * mm});
            skCircle(sketch, "E4.6.18.0", {"center": v(-9.34, -298.1) * mm, "radius": 2 * mm});
            skCircle(sketch, "E4.6.19.0", {"center": v(-9.34, -314.1) * mm, "radius": 2 * mm});
            skCircle(sketch, "E4.6.20.0", {"center": v(-9.34, -330.1) * mm, "radius": 2 * mm});
            skCircle(sketch, "E4.6.21.0", {"center": v(-9.34, -346.1) * mm, "radius": 2 * mm});
            skCircle(sketch, "E4.6.22.0", {"center": v(-9.34, -362.1) * mm, "radius": 2 * mm});
            skCircle(sketch, "E4.6.23.0", {"center": v(-9.34, -378.1) * mm, "radius": 2 * mm});
            skCircle(sketch, "E4.6.24.0", {"center": v(-9.34, -394.1) * mm, "radius": 2 * mm});
            skCircle(sketch, "E4.6.25.0", {"center": v(-9.34, -410.1) * mm, "radius": 2 * mm});
            skCircle(sketch, "E4.6.26.0", {"center": v(-9.34, -426.1) * mm, "radius": 2 * mm});
            skCircle(sketch, "E4.6.27.0", {"center": v(-9.34, -442.1) * mm, "radius": 2 * mm});
            skCircle(sketch, "E4.7.0.0", {"center": v(6.66, -10.1) * mm, "radius": 2 * mm});
            skCircle(sketch, "E4.7.1.0", {"center": v(6.66, -26.1) * mm, "radius": 2 * mm});
            skCircle(sketch, "E4.7.2.0", {"center": v(6.66, -42.1) * mm, "radius": 2 * mm});
            skCircle(sketch, "E4.7.3.0", {"center": v(6.66, -58.1) * mm, "radius": 2 * mm});
            skCircle(sketch, "E4.7.4.0", {"center": v(6.66, -74.1) * mm, "radius": 2 * mm});
            skCircle(sketch, "E4.7.5.0", {"center": v(6.66, -90.1) * mm, "radius": 2 * mm});
            skCircle(sketch, "E4.7.6.0", {"center": v(6.66, -106.1) * mm, "radius": 2 * mm});
            skCircle(sketch, "E4.7.7.0", {"center": v(6.66, -122.1) * mm, "radius": 2 * mm});
            skCircle(sketch, "E4.7.8.0", {"center": v(6.66, -138.1) * mm, "radius": 2 * mm});
            skCircle(sketch, "E4.7.9.0", {"center": v(6.66, -154.1) * mm, "radius": 2 * mm});
            skCircle(sketch, "E4.7.10.0", {"center": v(6.66, -170.1) * mm, "radius": 2 * mm});
            skCircle(sketch, "E4.7.11.0", {"center": v(6.66, -186.1) * mm, "radius": 2 * mm});
            skCircle(sketch, "E4.7.12.0", {"center": v(6.66, -202.1) * mm, "radius": 2 * mm});
            skCircle(sketch, "E4.7.13.0", {"center": v(6.66, -218.1) * mm, "radius": 2 * mm});
            skCircle(sketch, "E4.7.14.0", {"center": v(6.66, -234.1) * mm, "radius": 2 * mm});
            skCircle(sketch, "E4.7.15.0", {"center": v(6.66, -250.1) * mm, "radius": 2 * mm});
            skCircle(sketch, "E4.7.16.0", {"center": v(6.66, -266.1) * mm, "radius": 2 * mm});
            skCircle(sketch, "E4.7.17.0", {"center": v(6.66, -282.1) * mm, "radius": 2 * mm});
            skCircle(sketch, "E4.7.18.0", {"center": v(6.66, -298.1) * mm, "radius": 2 * mm});
            skCircle(sketch, "E4.7.19.0", {"center": v(6.66, -314.1) * mm, "radius": 2 * mm});
            skCircle(sketch, "E4.7.20.0", {"center": v(6.66, -330.1) * mm, "radius": 2 * mm});
            skCircle(sketch, "E4.7.21.0", {"center": v(6.66, -346.1) * mm, "radius": 2 * mm});
            skCircle(sketch, "E4.7.22.0", {"center": v(6.66, -362.1) * mm, "radius": 2 * mm});
            skCircle(sketch, "E4.7.23.0", {"center": v(6.66, -378.1) * mm, "radius": 2 * mm});
            skCircle(sketch, "E4.7.24.0", {"center": v(6.66, -394.1) * mm, "radius": 2 * mm});
            skCircle(sketch, "E4.7.25.0", {"center": v(6.66, -410.1) * mm, "radius": 2 * mm});
            skCircle(sketch, "E4.7.26.0", {"center": v(6.66, -426.1) * mm, "radius": 2 * mm});
            skCircle(sketch, "E4.7.27.0", {"center": v(6.66, -442.1) * mm, "radius": 2 * mm});
            skCircle(sketch, "E4.8.0.0", {"center": v(22.66, -10.1) * mm, "radius": 2 * mm});
            skCircle(sketch, "E4.8.1.0", {"center": v(22.66, -26.1) * mm, "radius": 2 * mm});
            skCircle(sketch, "E4.8.2.0", {"center": v(22.66, -42.1) * mm, "radius": 2 * mm});
            skCircle(sketch, "E4.8.3.0", {"center": v(22.66, -58.1) * mm, "radius": 2 * mm});
            skCircle(sketch, "E4.8.4.0", {"center": v(22.66, -74.1) * mm, "radius": 2 * mm});
            skCircle(sketch, "E4.8.5.0", {"center": v(22.66, -90.1) * mm, "radius": 2 * mm});
            skCircle(sketch, "E4.8.6.0", {"center": v(22.66, -106.1) * mm, "radius": 2 * mm});
            skCircle(sketch, "E4.8.7.0", {"center": v(22.66, -122.1) * mm, "radius": 2 * mm});
            skCircle(sketch, "E4.8.8.0", {"center": v(22.66, -138.1) * mm, "radius": 2 * mm});
            skCircle(sketch, "E4.8.9.0", {"center": v(22.66, -154.1) * mm, "radius": 2 * mm});
            skCircle(sketch, "E4.8.10.0", {"center": v(22.66, -170.1) * mm, "radius": 2 * mm});
            skCircle(sketch, "E4.8.11.0", {"center": v(22.66, -186.1) * mm, "radius": 2 * mm});
            skCircle(sketch, "E4.8.12.0", {"center": v(22.66, -202.1) * mm, "radius": 2 * mm});
            skCircle(sketch, "E4.8.13.0", {"center": v(22.66, -218.1) * mm, "radius": 2 * mm});
            skCircle(sketch, "E4.8.14.0", {"center": v(22.66, -234.1) * mm, "radius": 2 * mm});
            skCircle(sketch, "E4.8.15.0", {"center": v(22.66, -250.1) * mm, "radius": 2 * mm});
            skCircle(sketch, "E4.8.16.0", {"center": v(22.66, -266.1) * mm, "radius": 2 * mm});
            skCircle(sketch, "E4.8.17.0", {"center": v(22.66, -282.1) * mm, "radius": 2 * mm});
            skCircle(sketch, "E4.8.18.0", {"center": v(22.66, -298.1) * mm, "radius": 2 * mm});
            skCircle(sketch, "E4.8.19.0", {"center": v(22.66, -314.1) * mm, "radius": 2 * mm});
            skCircle(sketch, "E4.8.20.0", {"center": v(22.66, -330.1) * mm, "radius": 2 * mm});
            skCircle(sketch, "E4.8.21.0", {"center": v(22.66, -346.1) * mm, "radius": 2 * mm});
            skCircle(sketch, "E4.8.22.0", {"center": v(22.66, -362.1) * mm, "radius": 2 * mm});
            skCircle(sketch, "E4.8.23.0", {"center": v(22.66, -378.1) * mm, "radius": 2 * mm});
            skCircle(sketch, "E4.8.24.0", {"center": v(22.66, -394.1) * mm, "radius": 2 * mm});
            skCircle(sketch, "E4.8.25.0", {"center": v(22.66, -410.1) * mm, "radius": 2 * mm});
            skCircle(sketch, "E4.8.26.0", {"center": v(22.66, -426.1) * mm, "radius": 2 * mm});
            skCircle(sketch, "E4.8.27.0", {"center": v(22.66, -442.1) * mm, "radius": 2 * mm});
            skCircle(sketch, "E4.9.0.0", {"center": v(38.66, -10.1) * mm, "radius": 2 * mm});
            skCircle(sketch, "E4.9.1.0", {"center": v(38.66, -26.1) * mm, "radius": 2 * mm});
            skCircle(sketch, "E4.9.2.0", {"center": v(38.66, -42.1) * mm, "radius": 2 * mm});
            skCircle(sketch, "E4.9.3.0", {"center": v(38.66, -58.1) * mm, "radius": 2 * mm});
            skCircle(sketch, "E4.9.4.0", {"center": v(38.66, -74.1) * mm, "radius": 2 * mm});
            skCircle(sketch, "E4.9.5.0", {"center": v(38.66, -90.1) * mm, "radius": 2 * mm});
            skCircle(sketch, "E4.9.6.0", {"center": v(38.66, -106.1) * mm, "radius": 2 * mm});
            skCircle(sketch, "E4.9.7.0", {"center": v(38.66, -122.1) * mm, "radius": 2 * mm});
            skCircle(sketch, "E4.9.8.0", {"center": v(38.66, -138.1) * mm, "radius": 2 * mm});
            skCircle(sketch, "E4.9.9.0", {"center": v(38.66, -154.1) * mm, "radius": 2 * mm});
            skCircle(sketch, "E4.9.10.0", {"center": v(38.66, -170.1) * mm, "radius": 2 * mm});
            skCircle(sketch, "E4.9.11.0", {"center": v(38.66, -186.1) * mm, "radius": 2 * mm});
            skCircle(sketch, "E4.9.12.0", {"center": v(38.66, -202.1) * mm, "radius": 2 * mm});
            skCircle(sketch, "E4.9.13.0", {"center": v(38.66, -218.1) * mm, "radius": 2 * mm});
            skCircle(sketch, "E4.9.14.0", {"center": v(38.66, -234.1) * mm, "radius": 2 * mm});
            skCircle(sketch, "E4.9.15.0", {"center": v(38.66, -250.1) * mm, "radius": 2 * mm});
            skCircle(sketch, "E4.9.16.0", {"center": v(38.66, -266.1) * mm, "radius": 2 * mm});
            skCircle(sketch, "E4.9.17.0", {"center": v(38.66, -282.1) * mm, "radius": 2 * mm});
            skCircle(sketch, "E4.9.18.0", {"center": v(38.66, -298.1) * mm, "radius": 2 * mm});
            skCircle(sketch, "E4.9.19.0", {"center": v(38.66, -314.1) * mm, "radius": 2 * mm});
            skCircle(sketch, "E4.9.20.0", {"center": v(38.66, -330.1) * mm, "radius": 2 * mm});
            skCircle(sketch, "E4.9.21.0", {"center": v(38.66, -346.1) * mm, "radius": 2 * mm});
            skCircle(sketch, "E4.9.22.0", {"center": v(38.66, -362.1) * mm, "radius": 2 * mm});
            skCircle(sketch, "E4.9.23.0", {"center": v(38.66, -378.1) * mm, "radius": 2 * mm});
            skCircle(sketch, "E4.9.24.0", {"center": v(38.66, -394.1) * mm, "radius": 2 * mm});
            skCircle(sketch, "E4.9.25.0", {"center": v(38.66, -410.1) * mm, "radius": 2 * mm});
            skCircle(sketch, "E4.9.26.0", {"center": v(38.66, -426.1) * mm, "radius": 2 * mm});
            skCircle(sketch, "E4.9.27.0", {"center": v(38.66, -442.1) * mm, "radius": 2 * mm});
            skCircle(sketch, "E4.10.0.0", {"center": v(54.66, -10.1) * mm, "radius": 2 * mm});
            skCircle(sketch, "E4.10.1.0", {"center": v(54.66, -26.1) * mm, "radius": 2 * mm});
            skCircle(sketch, "E4.10.2.0", {"center": v(54.66, -42.1) * mm, "radius": 2 * mm});
            skCircle(sketch, "E4.10.3.0", {"center": v(54.66, -58.1) * mm, "radius": 2 * mm});
            skCircle(sketch, "E4.10.4.0", {"center": v(54.66, -74.1) * mm, "radius": 2 * mm});
            skCircle(sketch, "E4.10.5.0", {"center": v(54.66, -90.1) * mm, "radius": 2 * mm});
            skCircle(sketch, "E4.10.6.0", {"center": v(54.66, -106.1) * mm, "radius": 2 * mm});
            skCircle(sketch, "E4.10.7.0", {"center": v(54.66, -122.1) * mm, "radius": 2 * mm});
            skCircle(sketch, "E4.10.8.0", {"center": v(54.66, -138.1) * mm, "radius": 2 * mm});
            skCircle(sketch, "E4.10.9.0", {"center": v(54.66, -154.1) * mm, "radius": 2 * mm});
            skCircle(sketch, "E4.10.10.0", {"center": v(54.66, -170.1) * mm, "radius": 2 * mm});
            skCircle(sketch, "E4.10.11.0", {"center": v(54.66, -186.1) * mm, "radius": 2 * mm});
            skCircle(sketch, "E4.10.12.0", {"center": v(54.66, -202.1) * mm, "radius": 2 * mm});
            skCircle(sketch, "E4.10.13.0", {"center": v(54.66, -218.1) * mm, "radius": 2 * mm});
            skCircle(sketch, "E4.10.14.0", {"center": v(54.66, -234.1) * mm, "radius": 2 * mm});
            skCircle(sketch, "E4.10.15.0", {"center": v(54.66, -250.1) * mm, "radius": 2 * mm});
            skCircle(sketch, "E4.10.16.0", {"center": v(54.66, -266.1) * mm, "radius": 2 * mm});
            skCircle(sketch, "E4.10.17.0", {"center": v(54.66, -282.1) * mm, "radius": 2 * mm});
            skCircle(sketch, "E4.10.18.0", {"center": v(54.66, -298.1) * mm, "radius": 2 * mm});
            skCircle(sketch, "E4.10.19.0", {"center": v(54.66, -314.1) * mm, "radius": 2 * mm});
            skCircle(sketch, "E4.10.20.0", {"center": v(54.66, -330.1) * mm, "radius": 2 * mm});
            skCircle(sketch, "E4.10.21.0", {"center": v(54.66, -346.1) * mm, "radius": 2 * mm});
            skCircle(sketch, "E4.10.22.0", {"center": v(54.66, -362.1) * mm, "radius": 2 * mm});
            skCircle(sketch, "E4.10.23.0", {"center": v(54.66, -378.1) * mm, "radius": 2 * mm});
            skCircle(sketch, "E4.10.24.0", {"center": v(54.66, -394.1) * mm, "radius": 2 * mm});
            skCircle(sketch, "E4.10.25.0", {"center": v(54.66, -410.1) * mm, "radius": 2 * mm});
            skCircle(sketch, "E4.10.26.0", {"center": v(54.66, -426.1) * mm, "radius": 2 * mm});
            skCircle(sketch, "E4.10.27.0", {"center": v(54.66, -442.1) * mm, "radius": 2 * mm});
            skCircle(sketch, "E4.11.0.0", {"center": v(70.66, -10.1) * mm, "radius": 2 * mm});
            skCircle(sketch, "E4.11.1.0", {"center": v(70.66, -26.1) * mm, "radius": 2 * mm});
            skCircle(sketch, "E4.11.2.0", {"center": v(70.66, -42.1) * mm, "radius": 2 * mm});
            skCircle(sketch, "E4.11.3.0", {"center": v(70.66, -58.1) * mm, "radius": 2 * mm});
            skCircle(sketch, "E4.11.4.0", {"center": v(70.66, -74.1) * mm, "radius": 2 * mm});
            skCircle(sketch, "E4.11.5.0", {"center": v(70.66, -90.1) * mm, "radius": 2 * mm});
            skCircle(sketch, "E4.11.6.0", {"center": v(70.66, -106.1) * mm, "radius": 2 * mm});
            skCircle(sketch, "E4.11.7.0", {"center": v(70.66, -122.1) * mm, "radius": 2 * mm});
            skCircle(sketch, "E4.11.8.0", {"center": v(70.66, -138.1) * mm, "radius": 2 * mm});
            skCircle(sketch, "E4.11.9.0", {"center": v(70.66, -154.1) * mm, "radius": 2 * mm});
            skCircle(sketch, "E4.11.10.0", {"center": v(70.66, -170.1) * mm, "radius": 2 * mm});
            skCircle(sketch, "E4.11.11.0", {"center": v(70.66, -186.1) * mm, "radius": 2 * mm});
            skCircle(sketch, "E4.11.12.0", {"center": v(70.66, -202.1) * mm, "radius": 2 * mm});
            skCircle(sketch, "E4.11.13.0", {"center": v(70.66, -218.1) * mm, "radius": 2 * mm});
            skCircle(sketch, "E4.11.14.0", {"center": v(70.66, -234.1) * mm, "radius": 2 * mm});
            skCircle(sketch, "E4.11.15.0", {"center": v(70.66, -250.1) * mm, "radius": 2 * mm});
            skCircle(sketch, "E4.11.16.0", {"center": v(70.66, -266.1) * mm, "radius": 2 * mm});
            skCircle(sketch, "E4.11.17.0", {"center": v(70.66, -282.1) * mm, "radius": 2 * mm});
            skCircle(sketch, "E4.11.18.0", {"center": v(70.66, -298.1) * mm, "radius": 2 * mm});
            skCircle(sketch, "E4.11.19.0", {"center": v(70.66, -314.1) * mm, "radius": 2 * mm});
            skCircle(sketch, "E4.11.20.0", {"center": v(70.66, -330.1) * mm, "radius": 2 * mm});
            skCircle(sketch, "E4.11.21.0", {"center": v(70.66, -346.1) * mm, "radius": 2 * mm});
            skCircle(sketch, "E4.11.22.0", {"center": v(70.66, -362.1) * mm, "radius": 2 * mm});
            skCircle(sketch, "E4.11.23.0", {"center": v(70.66, -378.1) * mm, "radius": 2 * mm});
            skCircle(sketch, "E4.11.24.0", {"center": v(70.66, -394.1) * mm, "radius": 2 * mm});
            skCircle(sketch, "E4.11.25.0", {"center": v(70.66, -410.1) * mm, "radius": 2 * mm});
            skCircle(sketch, "E4.11.26.0", {"center": v(70.66, -426.1) * mm, "radius": 2 * mm});
            skCircle(sketch, "E4.11.27.0", {"center": v(70.66, -442.1) * mm, "radius": 2 * mm});
            skCircle(sketch, "E4.12.0.0", {"center": v(86.66, -10.1) * mm, "radius": 2 * mm});
            skCircle(sketch, "E4.12.1.0", {"center": v(86.66, -26.1) * mm, "radius": 2 * mm});
            skCircle(sketch, "E4.12.2.0", {"center": v(86.66, -42.1) * mm, "radius": 2 * mm});
            skCircle(sketch, "E4.12.3.0", {"center": v(86.66, -58.1) * mm, "radius": 2 * mm});
            skCircle(sketch, "E4.12.4.0", {"center": v(86.66, -74.1) * mm, "radius": 2 * mm});
            skCircle(sketch, "E4.12.5.0", {"center": v(86.66, -90.1) * mm, "radius": 2 * mm});
            skCircle(sketch, "E4.12.6.0", {"center": v(86.66, -106.1) * mm, "radius": 2 * mm});
            skCircle(sketch, "E4.12.7.0", {"center": v(86.66, -122.1) * mm, "radius": 2 * mm});
            skCircle(sketch, "E4.12.8.0", {"center": v(86.66, -138.1) * mm, "radius": 2 * mm});
            skCircle(sketch, "E4.12.9.0", {"center": v(86.66, -154.1) * mm, "radius": 2 * mm});
            skCircle(sketch, "E4.12.10.0", {"center": v(86.66, -170.1) * mm, "radius": 2 * mm});
            skCircle(sketch, "E4.12.11.0", {"center": v(86.66, -186.1) * mm, "radius": 2 * mm});
            skCircle(sketch, "E4.12.12.0", {"center": v(86.66, -202.1) * mm, "radius": 2 * mm});
            skCircle(sketch, "E4.12.13.0", {"center": v(86.66, -218.1) * mm, "radius": 2 * mm});
            skCircle(sketch, "E4.12.14.0", {"center": v(86.66, -234.1) * mm, "radius": 2 * mm});
            skCircle(sketch, "E4.12.15.0", {"center": v(86.66, -250.1) * mm, "radius": 2 * mm});
            skCircle(sketch, "E4.12.16.0", {"center": v(86.66, -266.1) * mm, "radius": 2 * mm});
            skCircle(sketch, "E4.12.17.0", {"center": v(86.66, -282.1) * mm, "radius": 2 * mm});
            skCircle(sketch, "E4.12.18.0", {"center": v(86.66, -298.1) * mm, "radius": 2 * mm});
            skCircle(sketch, "E4.12.19.0", {"center": v(86.66, -314.1) * mm, "radius": 2 * mm});
            skCircle(sketch, "E4.12.20.0", {"center": v(86.66, -330.1) * mm, "radius": 2 * mm});
            skCircle(sketch, "E4.12.21.0", {"center": v(86.66, -346.1) * mm, "radius": 2 * mm});
            skCircle(sketch, "E4.12.22.0", {"center": v(86.66, -362.1) * mm, "radius": 2 * mm});
            skCircle(sketch, "E4.12.23.0", {"center": v(86.66, -378.1) * mm, "radius": 2 * mm});
            skCircle(sketch, "E4.12.24.0", {"center": v(86.66, -394.1) * mm, "radius": 2 * mm});
            skCircle(sketch, "E4.12.25.0", {"center": v(86.66, -410.1) * mm, "radius": 2 * mm});
            skCircle(sketch, "E4.12.26.0", {"center": v(86.66, -426.1) * mm, "radius": 2 * mm});
            skCircle(sketch, "E4.12.27.0", {"center": v(86.66, -442.1) * mm, "radius": 2 * mm});
            skCircle(sketch, "E4.13.0.0", {"center": v(102.66, -10.1) * mm, "radius": 2 * mm});
            skCircle(sketch, "E4.13.1.0", {"center": v(102.66, -26.1) * mm, "radius": 2 * mm});
            skCircle(sketch, "E4.13.2.0", {"center": v(102.66, -42.1) * mm, "radius": 2 * mm});
            skCircle(sketch, "E4.13.3.0", {"center": v(102.66, -58.1) * mm, "radius": 2 * mm});
            skCircle(sketch, "E4.13.4.0", {"center": v(102.66, -74.1) * mm, "radius": 2 * mm});
            skCircle(sketch, "E4.13.5.0", {"center": v(102.66, -90.1) * mm, "radius": 2 * mm});
            skCircle(sketch, "E4.13.6.0", {"center": v(102.66, -106.1) * mm, "radius": 2 * mm});
            skCircle(sketch, "E4.13.7.0", {"center": v(102.66, -122.1) * mm, "radius": 2 * mm});
            skCircle(sketch, "E4.13.8.0", {"center": v(102.66, -138.1) * mm, "radius": 2 * mm});
            skCircle(sketch, "E4.13.9.0", {"center": v(102.66, -154.1) * mm, "radius": 2 * mm});
            skCircle(sketch, "E4.13.10.0", {"center": v(102.66, -170.1) * mm, "radius": 2 * mm});
            skCircle(sketch, "E4.13.11.0", {"center": v(102.66, -186.1) * mm, "radius": 2 * mm});
            skCircle(sketch, "E4.13.12.0", {"center": v(102.66, -202.1) * mm, "radius": 2 * mm});
            skCircle(sketch, "E4.13.13.0", {"center": v(102.66, -218.1) * mm, "radius": 2 * mm});
            skCircle(sketch, "E4.13.14.0", {"center": v(102.66, -234.1) * mm, "radius": 2 * mm});
            skCircle(sketch, "E4.13.15.0", {"center": v(102.66, -250.1) * mm, "radius": 2 * mm});
            skCircle(sketch, "E4.13.16.0", {"center": v(102.66, -266.1) * mm, "radius": 2 * mm});
            skCircle(sketch, "E4.13.17.0", {"center": v(102.66, -282.1) * mm, "radius": 2 * mm});
            skCircle(sketch, "E4.13.18.0", {"center": v(102.66, -298.1) * mm, "radius": 2 * mm});
            skCircle(sketch, "E4.13.19.0", {"center": v(102.66, -314.1) * mm, "radius": 2 * mm});
            skCircle(sketch, "E4.13.20.0", {"center": v(102.66, -330.1) * mm, "radius": 2 * mm});
            skCircle(sketch, "E4.13.21.0", {"center": v(102.66, -346.1) * mm, "radius": 2 * mm});
            skCircle(sketch, "E4.13.22.0", {"center": v(102.66, -362.1) * mm, "radius": 2 * mm});
            skCircle(sketch, "E4.13.23.0", {"center": v(102.66, -378.1) * mm, "radius": 2 * mm});
            skCircle(sketch, "E4.13.24.0", {"center": v(102.66, -394.1) * mm, "radius": 2 * mm});
            skCircle(sketch, "E4.13.25.0", {"center": v(102.66, -410.1) * mm, "radius": 2 * mm});
            skCircle(sketch, "E4.13.26.0", {"center": v(102.66, -426.1) * mm, "radius": 2 * mm});
            skCircle(sketch, "E4.13.27.0", {"center": v(102.66, -442.1) * mm, "radius": 2 * mm});
            skCircle(sketch, "E4.14.0.0", {"center": v(118.66, -10.1) * mm, "radius": 2 * mm});
            skCircle(sketch, "E4.14.1.0", {"center": v(118.66, -26.1) * mm, "radius": 2 * mm});
            skCircle(sketch, "E4.14.2.0", {"center": v(118.66, -42.1) * mm, "radius": 2 * mm});
            skCircle(sketch, "E4.14.3.0", {"center": v(118.66, -58.1) * mm, "radius": 2 * mm});
            skCircle(sketch, "E4.14.4.0", {"center": v(118.66, -74.1) * mm, "radius": 2 * mm});
            skCircle(sketch, "E4.14.5.0", {"center": v(118.66, -90.1) * mm, "radius": 2 * mm});
            skCircle(sketch, "E4.14.6.0", {"center": v(118.66, -106.1) * mm, "radius": 2 * mm});
            skCircle(sketch, "E4.14.7.0", {"center": v(118.66, -122.1) * mm, "radius": 2 * mm});
            skCircle(sketch, "E4.14.8.0", {"center": v(118.66, -138.1) * mm, "radius": 2 * mm});
            skCircle(sketch, "E4.14.9.0", {"center": v(118.66, -154.1) * mm, "radius": 2 * mm});
            skCircle(sketch, "E4.14.10.0", {"center": v(118.66, -170.1) * mm, "radius": 2 * mm});
            skCircle(sketch, "E4.14.11.0", {"center": v(118.66, -186.1) * mm, "radius": 2 * mm});
            skCircle(sketch, "E4.14.12.0", {"center": v(118.66, -202.1) * mm, "radius": 2 * mm});
            skCircle(sketch, "E4.14.13.0", {"center": v(118.66, -218.1) * mm, "radius": 2 * mm});
            skCircle(sketch, "E4.14.14.0", {"center": v(118.66, -234.1) * mm, "radius": 2 * mm});
            skCircle(sketch, "E4.14.15.0", {"center": v(118.66, -250.1) * mm, "radius": 2 * mm});
            skCircle(sketch, "E4.14.16.0", {"center": v(118.66, -266.1) * mm, "radius": 2 * mm});
            skCircle(sketch, "E4.14.17.0", {"center": v(118.66, -282.1) * mm, "radius": 2 * mm});
            skCircle(sketch, "E4.14.18.0", {"center": v(118.66, -298.1) * mm, "radius": 2 * mm});
            skCircle(sketch, "E4.14.19.0", {"center": v(118.66, -314.1) * mm, "radius": 2 * mm});
            skCircle(sketch, "E4.14.20.0", {"center": v(118.66, -330.1) * mm, "radius": 2 * mm});
            skCircle(sketch, "E4.14.21.0", {"center": v(118.66, -346.1) * mm, "radius": 2 * mm});
            skCircle(sketch, "E4.14.22.0", {"center": v(118.66, -362.1) * mm, "radius": 2 * mm});
            skCircle(sketch, "E4.14.23.0", {"center": v(118.66, -378.1) * mm, "radius": 2 * mm});
            skCircle(sketch, "E4.14.24.0", {"center": v(118.66, -394.1) * mm, "radius": 2 * mm});
            skCircle(sketch, "E4.14.25.0", {"center": v(118.66, -410.1) * mm, "radius": 2 * mm});
            skCircle(sketch, "E4.14.26.0", {"center": v(118.66, -426.1) * mm, "radius": 2 * mm});
            skCircle(sketch, "E4.14.27.0", {"center": v(118.66, -442.1) * mm, "radius": 2 * mm});
            skCircle(sketch, "E4.15.0.0", {"center": v(134.66, -10.1) * mm, "radius": 2 * mm});
            skCircle(sketch, "E4.15.1.0", {"center": v(134.66, -26.1) * mm, "radius": 2 * mm});
            skCircle(sketch, "E4.15.2.0", {"center": v(134.66, -42.1) * mm, "radius": 2 * mm});
            skCircle(sketch, "E4.15.3.0", {"center": v(134.66, -58.1) * mm, "radius": 2 * mm});
            skCircle(sketch, "E4.15.4.0", {"center": v(134.66, -74.1) * mm, "radius": 2 * mm});
            skCircle(sketch, "E4.15.5.0", {"center": v(134.66, -90.1) * mm, "radius": 2 * mm});
            skCircle(sketch, "E4.15.6.0", {"center": v(134.66, -106.1) * mm, "radius": 2 * mm});
            skCircle(sketch, "E4.15.7.0", {"center": v(134.66, -122.1) * mm, "radius": 2 * mm});
            skCircle(sketch, "E4.15.8.0", {"center": v(134.66, -138.1) * mm, "radius": 2 * mm});
            skCircle(sketch, "E4.15.9.0", {"center": v(134.66, -154.1) * mm, "radius": 2 * mm});
            skCircle(sketch, "E4.15.10.0", {"center": v(134.66, -170.1) * mm, "radius": 2 * mm});
            skCircle(sketch, "E4.15.11.0", {"center": v(134.66, -186.1) * mm, "radius": 2 * mm});
            skCircle(sketch, "E4.15.12.0", {"center": v(134.66, -202.1) * mm, "radius": 2 * mm});
            skCircle(sketch, "E4.15.13.0", {"center": v(134.66, -218.1) * mm, "radius": 2 * mm});
            skCircle(sketch, "E4.15.14.0", {"center": v(134.66, -234.1) * mm, "radius": 2 * mm});
            skCircle(sketch, "E4.15.15.0", {"center": v(134.66, -250.1) * mm, "radius": 2 * mm});
            skCircle(sketch, "E4.15.16.0", {"center": v(134.66, -266.1) * mm, "radius": 2 * mm});
            skCircle(sketch, "E4.15.17.0", {"center": v(134.66, -282.1) * mm, "radius": 2 * mm});
            skCircle(sketch, "E4.15.18.0", {"center": v(134.66, -298.1) * mm, "radius": 2 * mm});
            skCircle(sketch, "E4.15.19.0", {"center": v(134.66, -314.1) * mm, "radius": 2 * mm});
            skCircle(sketch, "E4.15.20.0", {"center": v(134.66, -330.1) * mm, "radius": 2 * mm});
            skCircle(sketch, "E4.15.21.0", {"center": v(134.66, -346.1) * mm, "radius": 2 * mm});
            skCircle(sketch, "E4.15.22.0", {"center": v(134.66, -362.1) * mm, "radius": 2 * mm});
            skCircle(sketch, "E4.15.23.0", {"center": v(134.66, -378.1) * mm, "radius": 2 * mm});
            skCircle(sketch, "E4.15.24.0", {"center": v(134.66, -394.1) * mm, "radius": 2 * mm});
            skCircle(sketch, "E4.15.25.0", {"center": v(134.66, -410.1) * mm, "radius": 2 * mm});
            skCircle(sketch, "E4.15.26.0", {"center": v(134.66, -426.1) * mm, "radius": 2 * mm});
            skCircle(sketch, "E4.15.27.0", {"center": v(134.66, -442.1) * mm, "radius": 2 * mm});
            skCircle(sketch, "E4.16.0.0", {"center": v(150.66, -10.1) * mm, "radius": 2 * mm});
            skCircle(sketch, "E4.16.1.0", {"center": v(150.66, -26.1) * mm, "radius": 2 * mm});
            skCircle(sketch, "E4.16.2.0", {"center": v(150.66, -42.1) * mm, "radius": 2 * mm});
            skCircle(sketch, "E4.16.3.0", {"center": v(150.66, -58.1) * mm, "radius": 2 * mm});
            skCircle(sketch, "E4.16.4.0", {"center": v(150.66, -74.1) * mm, "radius": 2 * mm});
            skCircle(sketch, "E4.16.5.0", {"center": v(150.66, -90.1) * mm, "radius": 2 * mm});
            skCircle(sketch, "E4.16.6.0", {"center": v(150.66, -106.1) * mm, "radius": 2 * mm});
            skCircle(sketch, "E4.16.7.0", {"center": v(150.66, -122.1) * mm, "radius": 2 * mm});
            skCircle(sketch, "E4.16.8.0", {"center": v(150.66, -138.1) * mm, "radius": 2 * mm});
            skCircle(sketch, "E4.16.9.0", {"center": v(150.66, -154.1) * mm, "radius": 2 * mm});
            skCircle(sketch, "E4.16.10.0", {"center": v(150.66, -170.1) * mm, "radius": 2 * mm});
            skCircle(sketch, "E4.16.11.0", {"center": v(150.66, -186.1) * mm, "radius": 2 * mm});
            skCircle(sketch, "E4.16.12.0", {"center": v(150.66, -202.1) * mm, "radius": 2 * mm});
            skCircle(sketch, "E4.16.13.0", {"center": v(150.66, -218.1) * mm, "radius": 2 * mm});
            skCircle(sketch, "E4.16.14.0", {"center": v(150.66, -234.1) * mm, "radius": 2 * mm});
            skCircle(sketch, "E4.16.15.0", {"center": v(150.66, -250.1) * mm, "radius": 2 * mm});
            skCircle(sketch, "E4.16.16.0", {"center": v(150.66, -266.1) * mm, "radius": 2 * mm});
            skCircle(sketch, "E4.16.17.0", {"center": v(150.66, -282.1) * mm, "radius": 2 * mm});
            skCircle(sketch, "E4.16.18.0", {"center": v(150.66, -298.1) * mm, "radius": 2 * mm});
            skCircle(sketch, "E4.16.19.0", {"center": v(150.66, -314.1) * mm, "radius": 2 * mm});
            skCircle(sketch, "E4.16.20.0", {"center": v(150.66, -330.1) * mm, "radius": 2 * mm});
            skCircle(sketch, "E4.16.21.0", {"center": v(150.66, -346.1) * mm, "radius": 2 * mm});
            skCircle(sketch, "E4.16.22.0", {"center": v(150.66, -362.1) * mm, "radius": 2 * mm});
            skCircle(sketch, "E4.16.23.0", {"center": v(150.66, -378.1) * mm, "radius": 2 * mm});
            skCircle(sketch, "E4.16.24.0", {"center": v(150.66, -394.1) * mm, "radius": 2 * mm});
            skCircle(sketch, "E4.16.25.0", {"center": v(150.66, -410.1) * mm, "radius": 2 * mm});
            skCircle(sketch, "E4.16.26.0", {"center": v(150.66, -426.1) * mm, "radius": 2 * mm});
            skCircle(sketch, "E4.16.27.0", {"center": v(150.66, -442.1) * mm, "radius": 2 * mm});
            skCircle(sketch, "E4.17.0.0", {"center": v(166.66, -10.1) * mm, "radius": 2 * mm});
            skCircle(sketch, "E4.17.1.0", {"center": v(166.66, -26.1) * mm, "radius": 2 * mm});
            skCircle(sketch, "E4.17.2.0", {"center": v(166.66, -42.1) * mm, "radius": 2 * mm});
            skCircle(sketch, "E4.17.3.0", {"center": v(166.66, -58.1) * mm, "radius": 2 * mm});
            skCircle(sketch, "E4.17.4.0", {"center": v(166.66, -74.1) * mm, "radius": 2 * mm});
            skCircle(sketch, "E4.17.5.0", {"center": v(166.66, -90.1) * mm, "radius": 2 * mm});
            skCircle(sketch, "E4.17.6.0", {"center": v(166.66, -106.1) * mm, "radius": 2 * mm});
            skCircle(sketch, "E4.17.7.0", {"center": v(166.66, -122.1) * mm, "radius": 2 * mm});
            skCircle(sketch, "E4.17.8.0", {"center": v(166.66, -138.1) * mm, "radius": 2 * mm});
            skCircle(sketch, "E4.17.9.0", {"center": v(166.66, -154.1) * mm, "radius": 2 * mm});
            skCircle(sketch, "E4.17.10.0", {"center": v(166.66, -170.1) * mm, "radius": 2 * mm});
            skCircle(sketch, "E4.17.11.0", {"center": v(166.66, -186.1) * mm, "radius": 2 * mm});
            skCircle(sketch, "E4.17.12.0", {"center": v(166.66, -202.1) * mm, "radius": 2 * mm});
            skCircle(sketch, "E4.17.13.0", {"center": v(166.66, -218.1) * mm, "radius": 2 * mm});
            skCircle(sketch, "E4.17.14.0", {"center": v(166.66, -234.1) * mm, "radius": 2 * mm});
            skCircle(sketch, "E4.17.15.0", {"center": v(166.66, -250.1) * mm, "radius": 2 * mm});
            skCircle(sketch, "E4.17.16.0", {"center": v(166.66, -266.1) * mm, "radius": 2 * mm});
            skCircle(sketch, "E4.17.17.0", {"center": v(166.66, -282.1) * mm, "radius": 2 * mm});
            skCircle(sketch, "E4.17.18.0", {"center": v(166.66, -298.1) * mm, "radius": 2 * mm});
            skCircle(sketch, "E4.17.19.0", {"center": v(166.66, -314.1) * mm, "radius": 2 * mm});
            skCircle(sketch, "E4.17.20.0", {"center": v(166.66, -330.1) * mm, "radius": 2 * mm});
            skCircle(sketch, "E4.17.21.0", {"center": v(166.66, -346.1) * mm, "radius": 2 * mm});
            skCircle(sketch, "E4.17.22.0", {"center": v(166.66, -362.1) * mm, "radius": 2 * mm});
            skCircle(sketch, "E4.17.23.0", {"center": v(166.66, -378.1) * mm, "radius": 2 * mm});
            skCircle(sketch, "E4.17.24.0", {"center": v(166.66, -394.1) * mm, "radius": 2 * mm});
            skCircle(sketch, "E4.17.25.0", {"center": v(166.66, -410.1) * mm, "radius": 2 * mm});
            skCircle(sketch, "E4.17.26.0", {"center": v(166.66, -426.1) * mm, "radius": 2 * mm});
            skCircle(sketch, "E4.17.27.0", {"center": v(166.66, -442.1) * mm, "radius": 2 * mm});
            skCircle(sketch, "E4.18.0.0", {"center": v(182.66, -10.1) * mm, "radius": 2 * mm});
            skCircle(sketch, "E4.18.1.0", {"center": v(182.66, -26.1) * mm, "radius": 2 * mm});
            skCircle(sketch, "E4.18.2.0", {"center": v(182.66, -42.1) * mm, "radius": 2 * mm});
            skCircle(sketch, "E4.18.3.0", {"center": v(182.66, -58.1) * mm, "radius": 2 * mm});
            skCircle(sketch, "E4.18.4.0", {"center": v(182.66, -74.1) * mm, "radius": 2 * mm});
            skCircle(sketch, "E4.18.5.0", {"center": v(182.66, -90.1) * mm, "radius": 2 * mm});
            skCircle(sketch, "E4.18.6.0", {"center": v(182.66, -106.1) * mm, "radius": 2 * mm});
            skCircle(sketch, "E4.18.7.0", {"center": v(182.66, -122.1) * mm, "radius": 2 * mm});
            skCircle(sketch, "E4.18.8.0", {"center": v(182.66, -138.1) * mm, "radius": 2 * mm});
            skCircle(sketch, "E4.18.9.0", {"center": v(182.66, -154.1) * mm, "radius": 2 * mm});
            skCircle(sketch, "E4.18.10.0", {"center": v(182.66, -170.1) * mm, "radius": 2 * mm});
            skCircle(sketch, "E4.18.11.0", {"center": v(182.66, -186.1) * mm, "radius": 2 * mm});
            skCircle(sketch, "E4.18.12.0", {"center": v(182.66, -202.1) * mm, "radius": 2 * mm});
            skCircle(sketch, "E4.18.13.0", {"center": v(182.66, -218.1) * mm, "radius": 2 * mm});
            skCircle(sketch, "E4.18.14.0", {"center": v(182.66, -234.1) * mm, "radius": 2 * mm});
            skCircle(sketch, "E4.18.15.0", {"center": v(182.66, -250.1) * mm, "radius": 2 * mm});
            skCircle(sketch, "E4.18.16.0", {"center": v(182.66, -266.1) * mm, "radius": 2 * mm});
            skCircle(sketch, "E4.18.17.0", {"center": v(182.66, -282.1) * mm, "radius": 2 * mm});
            skCircle(sketch, "E4.18.18.0", {"center": v(182.66, -298.1) * mm, "radius": 2 * mm});
            skCircle(sketch, "E4.18.19.0", {"center": v(182.66, -314.1) * mm, "radius": 2 * mm});
            skCircle(sketch, "E4.18.20.0", {"center": v(182.66, -330.1) * mm, "radius": 2 * mm});
            skCircle(sketch, "E4.18.21.0", {"center": v(182.66, -346.1) * mm, "radius": 2 * mm});
            skCircle(sketch, "E4.18.22.0", {"center": v(182.66, -362.1) * mm, "radius": 2 * mm});
            skCircle(sketch, "E4.18.23.0", {"center": v(182.66, -378.1) * mm, "radius": 2 * mm});
            skCircle(sketch, "E4.18.24.0", {"center": v(182.66, -394.1) * mm, "radius": 2 * mm});
            skCircle(sketch, "E4.18.25.0", {"center": v(182.66, -410.1) * mm, "radius": 2 * mm});
            skCircle(sketch, "E4.18.26.0", {"center": v(182.66, -426.1) * mm, "radius": 2 * mm});
            skCircle(sketch, "E4.18.27.0", {"center": v(182.66, -442.1) * mm, "radius": 2 * mm});
            skCircle(sketch, "E4.19.0.0", {"center": v(198.66, -10.1) * mm, "radius": 2 * mm});
            skCircle(sketch, "E4.19.1.0", {"center": v(198.66, -26.1) * mm, "radius": 2 * mm});
            skCircle(sketch, "E4.19.2.0", {"center": v(198.66, -42.1) * mm, "radius": 2 * mm});
            skCircle(sketch, "E4.19.3.0", {"center": v(198.66, -58.1) * mm, "radius": 2 * mm});
            skCircle(sketch, "E4.19.4.0", {"center": v(198.66, -74.1) * mm, "radius": 2 * mm});
            skCircle(sketch, "E4.19.5.0", {"center": v(198.66, -90.1) * mm, "radius": 2 * mm});
            skCircle(sketch, "E4.19.6.0", {"center": v(198.66, -106.1) * mm, "radius": 2 * mm});
            skCircle(sketch, "E4.19.7.0", {"center": v(198.66, -122.1) * mm, "radius": 2 * mm});
            skCircle(sketch, "E4.19.8.0", {"center": v(198.66, -138.1) * mm, "radius": 2 * mm});
            skCircle(sketch, "E4.19.9.0", {"center": v(198.66, -154.1) * mm, "radius": 2 * mm});
            skCircle(sketch, "E4.19.10.0", {"center": v(198.66, -170.1) * mm, "radius": 2 * mm});
            skCircle(sketch, "E4.19.11.0", {"center": v(198.66, -186.1) * mm, "radius": 2 * mm});
            skCircle(sketch, "E4.19.12.0", {"center": v(198.66, -202.1) * mm, "radius": 2 * mm});
            skCircle(sketch, "E4.19.13.0", {"center": v(198.66, -218.1) * mm, "radius": 2 * mm});
            skCircle(sketch, "E4.19.14.0", {"center": v(198.66, -234.1) * mm, "radius": 2 * mm});
            skCircle(sketch, "E4.19.15.0", {"center": v(198.66, -250.1) * mm, "radius": 2 * mm});
            skCircle(sketch, "E4.19.16.0", {"center": v(198.66, -266.1) * mm, "radius": 2 * mm});
            skCircle(sketch, "E4.19.17.0", {"center": v(198.66, -282.1) * mm, "radius": 2 * mm});
            skCircle(sketch, "E4.19.18.0", {"center": v(198.66, -298.1) * mm, "radius": 2 * mm});
            skCircle(sketch, "E4.19.19.0", {"center": v(198.66, -314.1) * mm, "radius": 2 * mm});
            skCircle(sketch, "E4.19.20.0", {"center": v(198.66, -330.1) * mm, "radius": 2 * mm});
            skCircle(sketch, "E4.19.21.0", {"center": v(198.66, -346.1) * mm, "radius": 2 * mm});
            skCircle(sketch, "E4.19.22.0", {"center": v(198.66, -362.1) * mm, "radius": 2 * mm});
            skCircle(sketch, "E4.19.23.0", {"center": v(198.66, -378.1) * mm, "radius": 2 * mm});
            skCircle(sketch, "E4.19.24.0", {"center": v(198.66, -394.1) * mm, "radius": 2 * mm});
            skCircle(sketch, "E4.19.25.0", {"center": v(198.66, -410.1) * mm, "radius": 2 * mm});
            skCircle(sketch, "E4.19.26.0", {"center": v(198.66, -426.1) * mm, "radius": 2 * mm});
            skCircle(sketch, "E4.19.27.0", {"center": v(198.66, -442.1) * mm, "radius": 2 * mm});
            skCircle(sketch, "E4.20.0.0", {"center": v(214.66, -10.1) * mm, "radius": 2 * mm});
            skCircle(sketch, "E4.20.1.0", {"center": v(214.66, -26.1) * mm, "radius": 2 * mm});
            skCircle(sketch, "E4.20.2.0", {"center": v(214.66, -42.1) * mm, "radius": 2 * mm});
            skCircle(sketch, "E4.20.3.0", {"center": v(214.66, -58.1) * mm, "radius": 2 * mm});
            skCircle(sketch, "E4.20.4.0", {"center": v(214.66, -74.1) * mm, "radius": 2 * mm});
            skCircle(sketch, "E4.20.5.0", {"center": v(214.66, -90.1) * mm, "radius": 2 * mm});
            skCircle(sketch, "E4.20.6.0", {"center": v(214.66, -106.1) * mm, "radius": 2 * mm});
            skCircle(sketch, "E4.20.7.0", {"center": v(214.66, -122.1) * mm, "radius": 2 * mm});
            skCircle(sketch, "E4.20.8.0", {"center": v(214.66, -138.1) * mm, "radius": 2 * mm});
            skCircle(sketch, "E4.20.9.0", {"center": v(214.66, -154.1) * mm, "radius": 2 * mm});
            skCircle(sketch, "E4.20.10.0", {"center": v(214.66, -170.1) * mm, "radius": 2 * mm});
            skCircle(sketch, "E4.20.11.0", {"center": v(214.66, -186.1) * mm, "radius": 2 * mm});
            skCircle(sketch, "E4.20.12.0", {"center": v(214.66, -202.1) * mm, "radius": 2 * mm});
            skCircle(sketch, "E4.20.13.0", {"center": v(214.66, -218.1) * mm, "radius": 2 * mm});
            skCircle(sketch, "E4.20.14.0", {"center": v(214.66, -234.1) * mm, "radius": 2 * mm});
            skCircle(sketch, "E4.20.15.0", {"center": v(214.66, -250.1) * mm, "radius": 2 * mm});
            skCircle(sketch, "E4.20.16.0", {"center": v(214.66, -266.1) * mm, "radius": 2 * mm});
            skCircle(sketch, "E4.20.17.0", {"center": v(214.66, -282.1) * mm, "radius": 2 * mm});
            skCircle(sketch, "E4.20.18.0", {"center": v(214.66, -298.1) * mm, "radius": 2 * mm});
            skCircle(sketch, "E4.20.19.0", {"center": v(214.66, -314.1) * mm, "radius": 2 * mm});
            skCircle(sketch, "E4.20.20.0", {"center": v(214.66, -330.1) * mm, "radius": 2 * mm});
            skCircle(sketch, "E4.20.21.0", {"center": v(214.66, -346.1) * mm, "radius": 2 * mm});
            skCircle(sketch, "E4.20.22.0", {"center": v(214.66, -362.1) * mm, "radius": 2 * mm});
            skCircle(sketch, "E4.20.23.0", {"center": v(214.66, -378.1) * mm, "radius": 2 * mm});
            skCircle(sketch, "E4.20.24.0", {"center": v(214.66, -394.1) * mm, "radius": 2 * mm});
            skCircle(sketch, "E4.20.25.0", {"center": v(214.66, -410.1) * mm, "radius": 2 * mm});
            skCircle(sketch, "E4.20.26.0", {"center": v(214.66, -426.1) * mm, "radius": 2 * mm});
            skCircle(sketch, "E4.20.27.0", {"center": v(214.66, -442.1) * mm, "radius": 2 * mm});
            skCircle(sketch, "E4.21.0.0", {"center": v(230.66, -10.1) * mm, "radius": 2 * mm});
            skCircle(sketch, "E4.21.1.0", {"center": v(230.66, -26.1) * mm, "radius": 2 * mm});
            skCircle(sketch, "E4.21.2.0", {"center": v(230.66, -42.1) * mm, "radius": 2 * mm});
            skCircle(sketch, "E4.21.3.0", {"center": v(230.66, -58.1) * mm, "radius": 2 * mm});
            skCircle(sketch, "E4.21.4.0", {"center": v(230.66, -74.1) * mm, "radius": 2 * mm});
            skCircle(sketch, "E4.21.5.0", {"center": v(230.66, -90.1) * mm, "radius": 2 * mm});
            skCircle(sketch, "E4.21.6.0", {"center": v(230.66, -106.1) * mm, "radius": 2 * mm});
            skCircle(sketch, "E4.21.7.0", {"center": v(230.66, -122.1) * mm, "radius": 2 * mm});
            skCircle(sketch, "E4.21.8.0", {"center": v(230.66, -138.1) * mm, "radius": 2 * mm});
            skCircle(sketch, "E4.21.9.0", {"center": v(230.66, -154.1) * mm, "radius": 2 * mm});
            skCircle(sketch, "E4.21.10.0", {"center": v(230.66, -170.1) * mm, "radius": 2 * mm});
            skCircle(sketch, "E4.21.11.0", {"center": v(230.66, -186.1) * mm, "radius": 2 * mm});
            skCircle(sketch, "E4.21.12.0", {"center": v(230.66, -202.1) * mm, "radius": 2 * mm});
            skCircle(sketch, "E4.21.13.0", {"center": v(230.66, -218.1) * mm, "radius": 2 * mm});
            skCircle(sketch, "E4.21.14.0", {"center": v(230.66, -234.1) * mm, "radius": 2 * mm});
            skCircle(sketch, "E4.21.15.0", {"center": v(230.66, -250.1) * mm, "radius": 2 * mm});
            skCircle(sketch, "E4.21.16.0", {"center": v(230.66, -266.1) * mm, "radius": 2 * mm});
            skCircle(sketch, "E4.21.17.0", {"center": v(230.66, -282.1) * mm, "radius": 2 * mm});
            skCircle(sketch, "E4.21.18.0", {"center": v(230.66, -298.1) * mm, "radius": 2 * mm});
            skCircle(sketch, "E4.21.19.0", {"center": v(230.66, -314.1) * mm, "radius": 2 * mm});
            skCircle(sketch, "E4.21.20.0", {"center": v(230.66, -330.1) * mm, "radius": 2 * mm});
            skCircle(sketch, "E4.21.21.0", {"center": v(230.66, -346.1) * mm, "radius": 2 * mm});
            skCircle(sketch, "E4.21.22.0", {"center": v(230.66, -362.1) * mm, "radius": 2 * mm});
            skCircle(sketch, "E4.21.23.0", {"center": v(230.66, -378.1) * mm, "radius": 2 * mm});
            skCircle(sketch, "E4.21.24.0", {"center": v(230.66, -394.1) * mm, "radius": 2 * mm});
            skCircle(sketch, "E4.21.25.0", {"center": v(230.66, -410.1) * mm, "radius": 2 * mm});
            skCircle(sketch, "E4.21.26.0", {"center": v(230.66, -426.1) * mm, "radius": 2 * mm});
            skCircle(sketch, "E4.21.27.0", {"center": v(230.66, -442.1) * mm, "radius": 2 * mm});
            skCircle(sketch, "E4.22.0.0", {"center": v(246.66, -10.1) * mm, "radius": 2 * mm});
            skCircle(sketch, "E4.22.1.0", {"center": v(246.66, -26.1) * mm, "radius": 2 * mm});
            skCircle(sketch, "E4.22.2.0", {"center": v(246.66, -42.1) * mm, "radius": 2 * mm});
            skCircle(sketch, "E4.22.3.0", {"center": v(246.66, -58.1) * mm, "radius": 2 * mm});
            skCircle(sketch, "E4.22.4.0", {"center": v(246.66, -74.1) * mm, "radius": 2 * mm});
            skCircle(sketch, "E4.22.5.0", {"center": v(246.66, -90.1) * mm, "radius": 2 * mm});
            skCircle(sketch, "E4.22.6.0", {"center": v(246.66, -106.1) * mm, "radius": 2 * mm});
            skCircle(sketch, "E4.22.7.0", {"center": v(246.66, -122.1) * mm, "radius": 2 * mm});
            skCircle(sketch, "E4.22.8.0", {"center": v(246.66, -138.1) * mm, "radius": 2 * mm});
            skCircle(sketch, "E4.22.9.0", {"center": v(246.66, -154.1) * mm, "radius": 2 * mm});
            skCircle(sketch, "E4.22.10.0", {"center": v(246.66, -170.1) * mm, "radius": 2 * mm});
            skCircle(sketch, "E4.22.11.0", {"center": v(246.66, -186.1) * mm, "radius": 2 * mm});
            skCircle(sketch, "E4.22.12.0", {"center": v(246.66, -202.1) * mm, "radius": 2 * mm});
            skCircle(sketch, "E4.22.13.0", {"center": v(246.66, -218.1) * mm, "radius": 2 * mm});
            skCircle(sketch, "E4.22.14.0", {"center": v(246.66, -234.1) * mm, "radius": 2 * mm});
            skCircle(sketch, "E4.22.15.0", {"center": v(246.66, -250.1) * mm, "radius": 2 * mm});
            skCircle(sketch, "E4.22.16.0", {"center": v(246.66, -266.1) * mm, "radius": 2 * mm});
            skCircle(sketch, "E4.22.17.0", {"center": v(246.66, -282.1) * mm, "radius": 2 * mm});
            skCircle(sketch, "E4.22.18.0", {"center": v(246.66, -298.1) * mm, "radius": 2 * mm});
            skCircle(sketch, "E4.22.19.0", {"center": v(246.66, -314.1) * mm, "radius": 2 * mm});
            skCircle(sketch, "E4.22.20.0", {"center": v(246.66, -330.1) * mm, "radius": 2 * mm});
            skCircle(sketch, "E4.22.21.0", {"center": v(246.66, -346.1) * mm, "radius": 2 * mm});
            skCircle(sketch, "E4.22.22.0", {"center": v(246.66, -362.1) * mm, "radius": 2 * mm});
            skCircle(sketch, "E4.22.23.0", {"center": v(246.66, -378.1) * mm, "radius": 2 * mm});
            skCircle(sketch, "E4.22.24.0", {"center": v(246.66, -394.1) * mm, "radius": 2 * mm});
            skCircle(sketch, "E4.22.25.0", {"center": v(246.66, -410.1) * mm, "radius": 2 * mm});
            skCircle(sketch, "E4.22.26.0", {"center": v(246.66, -426.1) * mm, "radius": 2 * mm});
            skCircle(sketch, "E4.22.27.0", {"center": v(246.66, -442.1) * mm, "radius": 2 * mm});
            skCircle(sketch, "E4.23.0.0", {"center": v(262.66, -10.1) * mm, "radius": 2 * mm});
            skCircle(sketch, "E4.23.1.0", {"center": v(262.66, -26.1) * mm, "radius": 2 * mm});
            skCircle(sketch, "E4.23.2.0", {"center": v(262.66, -42.1) * mm, "radius": 2 * mm});
            skCircle(sketch, "E4.23.3.0", {"center": v(262.66, -58.1) * mm, "radius": 2 * mm});
            skCircle(sketch, "E4.23.4.0", {"center": v(262.66, -74.1) * mm, "radius": 2 * mm});
            skCircle(sketch, "E4.23.5.0", {"center": v(262.66, -90.1) * mm, "radius": 2 * mm});
            skCircle(sketch, "E4.23.6.0", {"center": v(262.66, -106.1) * mm, "radius": 2 * mm});
            skCircle(sketch, "E4.23.7.0", {"center": v(262.66, -122.1) * mm, "radius": 2 * mm});
            skCircle(sketch, "E4.23.8.0", {"center": v(262.66, -138.1) * mm, "radius": 2 * mm});
            skCircle(sketch, "E4.23.9.0", {"center": v(262.66, -154.1) * mm, "radius": 2 * mm});
            skCircle(sketch, "E4.23.10.0", {"center": v(262.66, -170.1) * mm, "radius": 2 * mm});
            skCircle(sketch, "E4.23.11.0", {"center": v(262.66, -186.1) * mm, "radius": 2 * mm});
            skCircle(sketch, "E4.23.12.0", {"center": v(262.66, -202.1) * mm, "radius": 2 * mm});
            skCircle(sketch, "E4.23.13.0", {"center": v(262.66, -218.1) * mm, "radius": 2 * mm});
            skCircle(sketch, "E4.23.14.0", {"center": v(262.66, -234.1) * mm, "radius": 2 * mm});
            skCircle(sketch, "E4.23.15.0", {"center": v(262.66, -250.1) * mm, "radius": 2 * mm});
            skCircle(sketch, "E4.23.16.0", {"center": v(262.66, -266.1) * mm, "radius": 2 * mm});
            skCircle(sketch, "E4.23.17.0", {"center": v(262.66, -282.1) * mm, "radius": 2 * mm});
            skCircle(sketch, "E4.23.18.0", {"center": v(262.66, -298.1) * mm, "radius": 2 * mm});
            skCircle(sketch, "E4.23.19.0", {"center": v(262.66, -314.1) * mm, "radius": 2 * mm});
            skCircle(sketch, "E4.23.20.0", {"center": v(262.66, -330.1) * mm, "radius": 2 * mm});
            skCircle(sketch, "E4.23.21.0", {"center": v(262.66, -346.1) * mm, "radius": 2 * mm});
            skCircle(sketch, "E4.23.22.0", {"center": v(262.66, -362.1) * mm, "radius": 2 * mm});
            skCircle(sketch, "E4.23.23.0", {"center": v(262.66, -378.1) * mm, "radius": 2 * mm});
            skCircle(sketch, "E4.23.24.0", {"center": v(262.66, -394.1) * mm, "radius": 2 * mm});
            skCircle(sketch, "E4.23.25.0", {"center": v(262.66, -410.1) * mm, "radius": 2 * mm});
            skCircle(sketch, "E4.23.26.0", {"center": v(262.66, -426.1) * mm, "radius": 2 * mm});
            skCircle(sketch, "E4.23.27.0", {"center": v(262.66, -442.1) * mm, "radius": 2 * mm});
            skCircle(sketch, "E4.24.0.0", {"center": v(278.66, -10.1) * mm, "radius": 2 * mm});
            skCircle(sketch, "E4.24.1.0", {"center": v(278.66, -26.1) * mm, "radius": 2 * mm});
            skCircle(sketch, "E4.24.2.0", {"center": v(278.66, -42.1) * mm, "radius": 2 * mm});
            skCircle(sketch, "E4.24.3.0", {"center": v(278.66, -58.1) * mm, "radius": 2 * mm});
            skCircle(sketch, "E4.24.4.0", {"center": v(278.66, -74.1) * mm, "radius": 2 * mm});
            skCircle(sketch, "E4.24.5.0", {"center": v(278.66, -90.1) * mm, "radius": 2 * mm});
            skCircle(sketch, "E4.24.6.0", {"center": v(278.66, -106.1) * mm, "radius": 2 * mm});
            skCircle(sketch, "E4.24.7.0", {"center": v(278.66, -122.1) * mm, "radius": 2 * mm});
            skCircle(sketch, "E4.24.8.0", {"center": v(278.66, -138.1) * mm, "radius": 2 * mm});
            skCircle(sketch, "E4.24.9.0", {"center": v(278.66, -154.1) * mm, "radius": 2 * mm});
            skCircle(sketch, "E4.24.10.0", {"center": v(278.66, -170.1) * mm, "radius": 2 * mm});
            skCircle(sketch, "E4.24.11.0", {"center": v(278.66, -186.1) * mm, "radius": 2 * mm});
            skCircle(sketch, "E4.24.12.0", {"center": v(278.66, -202.1) * mm, "radius": 2 * mm});
            skCircle(sketch, "E4.24.13.0", {"center": v(278.66, -218.1) * mm, "radius": 2 * mm});
            skCircle(sketch, "E4.24.14.0", {"center": v(278.66, -234.1) * mm, "radius": 2 * mm});
            skCircle(sketch, "E4.24.15.0", {"center": v(278.66, -250.1) * mm, "radius": 2 * mm});
            skCircle(sketch, "E4.24.16.0", {"center": v(278.66, -266.1) * mm, "radius": 2 * mm});
            skCircle(sketch, "E4.24.17.0", {"center": v(278.66, -282.1) * mm, "radius": 2 * mm});
            skCircle(sketch, "E4.24.18.0", {"center": v(278.66, -298.1) * mm, "radius": 2 * mm});
            skCircle(sketch, "E4.24.19.0", {"center": v(278.66, -314.1) * mm, "radius": 2 * mm});
            skCircle(sketch, "E4.24.20.0", {"center": v(278.66, -330.1) * mm, "radius": 2 * mm});
            skCircle(sketch, "E4.24.21.0", {"center": v(278.66, -346.1) * mm, "radius": 2 * mm});
            skCircle(sketch, "E4.24.22.0", {"center": v(278.66, -362.1) * mm, "radius": 2 * mm});
            skCircle(sketch, "E4.24.23.0", {"center": v(278.66, -378.1) * mm, "radius": 2 * mm});
            skCircle(sketch, "E4.24.24.0", {"center": v(278.66, -394.1) * mm, "radius": 2 * mm});
            skCircle(sketch, "E4.24.25.0", {"center": v(278.66, -410.1) * mm, "radius": 2 * mm});
            skCircle(sketch, "E4.24.26.0", {"center": v(278.66, -426.1) * mm, "radius": 2 * mm});
            skCircle(sketch, "E4.24.27.0", {"center": v(278.66, -442.1) * mm, "radius": 2 * mm});
            skCircle(sketch, "E4.25.0.0", {"center": v(294.66, -10.1) * mm, "radius": 2 * mm});
            skCircle(sketch, "E4.25.1.0", {"center": v(294.66, -26.1) * mm, "radius": 2 * mm});
            skCircle(sketch, "E4.25.2.0", {"center": v(294.66, -42.1) * mm, "radius": 2 * mm});
            skCircle(sketch, "E4.25.3.0", {"center": v(294.66, -58.1) * mm, "radius": 2 * mm});
            skCircle(sketch, "E4.25.4.0", {"center": v(294.66, -74.1) * mm, "radius": 2 * mm});
            skCircle(sketch, "E4.25.5.0", {"center": v(294.66, -90.1) * mm, "radius": 2 * mm});
            skCircle(sketch, "E4.25.6.0", {"center": v(294.66, -106.1) * mm, "radius": 2 * mm});
            skCircle(sketch, "E4.25.7.0", {"center": v(294.66, -122.1) * mm, "radius": 2 * mm});
            skCircle(sketch, "E4.25.8.0", {"center": v(294.66, -138.1) * mm, "radius": 2 * mm});
            skCircle(sketch, "E4.25.9.0", {"center": v(294.66, -154.1) * mm, "radius": 2 * mm});
            skCircle(sketch, "E4.25.10.0", {"center": v(294.66, -170.1) * mm, "radius": 2 * mm});
            skCircle(sketch, "E4.25.11.0", {"center": v(294.66, -186.1) * mm, "radius": 2 * mm});
            skCircle(sketch, "E4.25.12.0", {"center": v(294.66, -202.1) * mm, "radius": 2 * mm});
            skCircle(sketch, "E4.25.13.0", {"center": v(294.66, -218.1) * mm, "radius": 2 * mm});
            skCircle(sketch, "E4.25.14.0", {"center": v(294.66, -234.1) * mm, "radius": 2 * mm});
            skCircle(sketch, "E4.25.15.0", {"center": v(294.66, -250.1) * mm, "radius": 2 * mm});
            skCircle(sketch, "E4.25.16.0", {"center": v(294.66, -266.1) * mm, "radius": 2 * mm});
            skCircle(sketch, "E4.25.17.0", {"center": v(294.66, -282.1) * mm, "radius": 2 * mm});
            skCircle(sketch, "E4.25.18.0", {"center": v(294.66, -298.1) * mm, "radius": 2 * mm});
            skCircle(sketch, "E4.25.19.0", {"center": v(294.66, -314.1) * mm, "radius": 2 * mm});
            skCircle(sketch, "E4.25.20.0", {"center": v(294.66, -330.1) * mm, "radius": 2 * mm});
            skCircle(sketch, "E4.25.21.0", {"center": v(294.66, -346.1) * mm, "radius": 2 * mm});
            skCircle(sketch, "E4.25.22.0", {"center": v(294.66, -362.1) * mm, "radius": 2 * mm});
            skCircle(sketch, "E4.25.23.0", {"center": v(294.66, -378.1) * mm, "radius": 2 * mm});
            skCircle(sketch, "E4.25.24.0", {"center": v(294.66, -394.1) * mm, "radius": 2 * mm});
            skCircle(sketch, "E4.25.25.0", {"center": v(294.66, -410.1) * mm, "radius": 2 * mm});
            skCircle(sketch, "E4.25.26.0", {"center": v(294.66, -426.1) * mm, "radius": 2 * mm});
            skCircle(sketch, "E4.25.27.0", {"center": v(294.66, -442.1) * mm, "radius": 2 * mm});
            skCircle(sketch, "E4.26.0.0", {"center": v(310.66, -10.1) * mm, "radius": 2 * mm});
            skCircle(sketch, "E4.26.1.0", {"center": v(310.66, -26.1) * mm, "radius": 2 * mm});
            skCircle(sketch, "E4.26.2.0", {"center": v(310.66, -42.1) * mm, "radius": 2 * mm});
            skCircle(sketch, "E4.26.3.0", {"center": v(310.66, -58.1) * mm, "radius": 2 * mm});
            skCircle(sketch, "E4.26.4.0", {"center": v(310.66, -74.1) * mm, "radius": 2 * mm});
            skCircle(sketch, "E4.26.5.0", {"center": v(310.66, -90.1) * mm, "radius": 2 * mm});
            skCircle(sketch, "E4.26.6.0", {"center": v(310.66, -106.1) * mm, "radius": 2 * mm});
            skCircle(sketch, "E4.26.7.0", {"center": v(310.66, -122.1) * mm, "radius": 2 * mm});
            skCircle(sketch, "E4.26.8.0", {"center": v(310.66, -138.1) * mm, "radius": 2 * mm});
            skCircle(sketch, "E4.26.9.0", {"center": v(310.66, -154.1) * mm, "radius": 2 * mm});
            skCircle(sketch, "E4.26.10.0", {"center": v(310.66, -170.1) * mm, "radius": 2 * mm});
            skCircle(sketch, "E4.26.11.0", {"center": v(310.66, -186.1) * mm, "radius": 2 * mm});
            skCircle(sketch, "E4.26.12.0", {"center": v(310.66, -202.1) * mm, "radius": 2 * mm});
            skCircle(sketch, "E4.26.13.0", {"center": v(310.66, -218.1) * mm, "radius": 2 * mm});
            skCircle(sketch, "E4.26.14.0", {"center": v(310.66, -234.1) * mm, "radius": 2 * mm});
            skCircle(sketch, "E4.26.15.0", {"center": v(310.66, -250.1) * mm, "radius": 2 * mm});
            skCircle(sketch, "E4.26.16.0", {"center": v(310.66, -266.1) * mm, "radius": 2 * mm});
            skCircle(sketch, "E4.26.17.0", {"center": v(310.66, -282.1) * mm, "radius": 2 * mm});
            skCircle(sketch, "E4.26.18.0", {"center": v(310.66, -298.1) * mm, "radius": 2 * mm});
            skCircle(sketch, "E4.26.19.0", {"center": v(310.66, -314.1) * mm, "radius": 2 * mm});
            skCircle(sketch, "E4.26.20.0", {"center": v(310.66, -330.1) * mm, "radius": 2 * mm});
            skCircle(sketch, "E4.26.21.0", {"center": v(310.66, -346.1) * mm, "radius": 2 * mm});
            skCircle(sketch, "E4.26.22.0", {"center": v(310.66, -362.1) * mm, "radius": 2 * mm});
            skCircle(sketch, "E4.26.23.0", {"center": v(310.66, -378.1) * mm, "radius": 2 * mm});
            skCircle(sketch, "E4.26.24.0", {"center": v(310.66, -394.1) * mm, "radius": 2 * mm});
            skCircle(sketch, "E4.26.25.0", {"center": v(310.66, -410.1) * mm, "radius": 2 * mm});
            skCircle(sketch, "E4.26.26.0", {"center": v(310.66, -426.1) * mm, "radius": 2 * mm});
            skCircle(sketch, "E4.26.27.0", {"center": v(310.66, -442.1) * mm, "radius": 2 * mm});
            skCircle(sketch, "E4.27.0.0", {"center": v(326.66, -10.1) * mm, "radius": 2 * mm});
            skCircle(sketch, "E4.27.1.0", {"center": v(326.66, -26.1) * mm, "radius": 2 * mm});
            skCircle(sketch, "E4.27.2.0", {"center": v(326.66, -42.1) * mm, "radius": 2 * mm});
            skCircle(sketch, "E4.27.3.0", {"center": v(326.66, -58.1) * mm, "radius": 2 * mm});
            skCircle(sketch, "E4.27.4.0", {"center": v(326.66, -74.1) * mm, "radius": 2 * mm});
            skCircle(sketch, "E4.27.5.0", {"center": v(326.66, -90.1) * mm, "radius": 2 * mm});
            skCircle(sketch, "E4.27.6.0", {"center": v(326.66, -106.1) * mm, "radius": 2 * mm});
            skCircle(sketch, "E4.27.7.0", {"center": v(326.66, -122.1) * mm, "radius": 2 * mm});
            skCircle(sketch, "E4.27.8.0", {"center": v(326.66, -138.1) * mm, "radius": 2 * mm});
            skCircle(sketch, "E4.27.9.0", {"center": v(326.66, -154.1) * mm, "radius": 2 * mm});
            skCircle(sketch, "E4.27.10.0", {"center": v(326.66, -170.1) * mm, "radius": 2 * mm});
            skCircle(sketch, "E4.27.11.0", {"center": v(326.66, -186.1) * mm, "radius": 2 * mm});
            skCircle(sketch, "E4.27.12.0", {"center": v(326.66, -202.1) * mm, "radius": 2 * mm});
            skCircle(sketch, "E4.27.13.0", {"center": v(326.66, -218.1) * mm, "radius": 2 * mm});
            skCircle(sketch, "E4.27.14.0", {"center": v(326.66, -234.1) * mm, "radius": 2 * mm});
            skCircle(sketch, "E4.27.15.0", {"center": v(326.66, -250.1) * mm, "radius": 2 * mm});
            skCircle(sketch, "E4.27.16.0", {"center": v(326.66, -266.1) * mm, "radius": 2 * mm});
            skCircle(sketch, "E4.27.17.0", {"center": v(326.66, -282.1) * mm, "radius": 2 * mm});
            skCircle(sketch, "E4.27.18.0", {"center": v(326.66, -298.1) * mm, "radius": 2 * mm});
            skCircle(sketch, "E4.27.19.0", {"center": v(326.66, -314.1) * mm, "radius": 2 * mm});
            skCircle(sketch, "E4.27.20.0", {"center": v(326.66, -330.1) * mm, "radius": 2 * mm});
            skCircle(sketch, "E4.27.21.0", {"center": v(326.66, -346.1) * mm, "radius": 2 * mm});
            skCircle(sketch, "E4.27.22.0", {"center": v(326.66, -362.1) * mm, "radius": 2 * mm});
            skCircle(sketch, "E4.27.23.0", {"center": v(326.66, -378.1) * mm, "radius": 2 * mm});
            skCircle(sketch, "E4.27.24.0", {"center": v(326.66, -394.1) * mm, "radius": 2 * mm});
            skCircle(sketch, "E4.27.25.0", {"center": v(326.66, -410.1) * mm, "radius": 2 * mm});
            skCircle(sketch, "E4.27.26.0", {"center": v(326.66, -426.1) * mm, "radius": 2 * mm});
            skCircle(sketch, "E4.27.27.0", {"center": v(326.66, -442.1) * mm, "radius": 2 * mm});
            skCircle(sketch, "E4.28.0.0", {"center": v(342.66, -10.1) * mm, "radius": 2 * mm});
            skCircle(sketch, "E4.28.1.0", {"center": v(342.66, -26.1) * mm, "radius": 2 * mm});
            skCircle(sketch, "E4.28.2.0", {"center": v(342.66, -42.1) * mm, "radius": 2 * mm});
            skCircle(sketch, "E4.28.3.0", {"center": v(342.66, -58.1) * mm, "radius": 2 * mm});
            skCircle(sketch, "E4.28.4.0", {"center": v(342.66, -74.1) * mm, "radius": 2 * mm});
            skCircle(sketch, "E4.28.5.0", {"center": v(342.66, -90.1) * mm, "radius": 2 * mm});
            skCircle(sketch, "E4.28.6.0", {"center": v(342.66, -106.1) * mm, "radius": 2 * mm});
            skCircle(sketch, "E4.28.7.0", {"center": v(342.66, -122.1) * mm, "radius": 2 * mm});
            skCircle(sketch, "E4.28.8.0", {"center": v(342.66, -138.1) * mm, "radius": 2 * mm});
            skCircle(sketch, "E4.28.9.0", {"center": v(342.66, -154.1) * mm, "radius": 2 * mm});
            skCircle(sketch, "E4.28.10.0", {"center": v(342.66, -170.1) * mm, "radius": 2 * mm});
            skCircle(sketch, "E4.28.11.0", {"center": v(342.66, -186.1) * mm, "radius": 2 * mm});
            skCircle(sketch, "E4.28.12.0", {"center": v(342.66, -202.1) * mm, "radius": 2 * mm});
            skCircle(sketch, "E4.28.13.0", {"center": v(342.66, -218.1) * mm, "radius": 2 * mm});
            skCircle(sketch, "E4.28.14.0", {"center": v(342.66, -234.1) * mm, "radius": 2 * mm});
            skCircle(sketch, "E4.28.15.0", {"center": v(342.66, -250.1) * mm, "radius": 2 * mm});
            skCircle(sketch, "E4.28.16.0", {"center": v(342.66, -266.1) * mm, "radius": 2 * mm});
            skCircle(sketch, "E4.28.17.0", {"center": v(342.66, -282.1) * mm, "radius": 2 * mm});
            skCircle(sketch, "E4.28.18.0", {"center": v(342.66, -298.1) * mm, "radius": 2 * mm});
            skCircle(sketch, "E4.28.19.0", {"center": v(342.66, -314.1) * mm, "radius": 2 * mm});
            skCircle(sketch, "E4.28.20.0", {"center": v(342.66, -330.1) * mm, "radius": 2 * mm});
            skCircle(sketch, "E4.28.21.0", {"center": v(342.66, -346.1) * mm, "radius": 2 * mm});
            skCircle(sketch, "E4.28.22.0", {"center": v(342.66, -362.1) * mm, "radius": 2 * mm});
            skCircle(sketch, "E4.28.23.0", {"center": v(342.66, -378.1) * mm, "radius": 2 * mm});
            skCircle(sketch, "E4.28.24.0", {"center": v(342.66, -394.1) * mm, "radius": 2 * mm});
            skCircle(sketch, "E4.28.25.0", {"center": v(342.66, -410.1) * mm, "radius": 2 * mm});
            skCircle(sketch, "E4.28.26.0", {"center": v(342.66, -426.1) * mm, "radius": 2 * mm});
            skCircle(sketch, "E4.28.27.0", {"center": v(342.66, -442.1) * mm, "radius": 2 * mm});
            skCircle(sketch, "E4.29.0.0", {"center": v(358.66, -10.1) * mm, "radius": 2 * mm});
            skCircle(sketch, "E4.29.1.0", {"center": v(358.66, -26.1) * mm, "radius": 2 * mm});
            skCircle(sketch, "E4.29.2.0", {"center": v(358.66, -42.1) * mm, "radius": 2 * mm});
            skCircle(sketch, "E4.29.3.0", {"center": v(358.66, -58.1) * mm, "radius": 2 * mm});
            skCircle(sketch, "E4.29.4.0", {"center": v(358.66, -74.1) * mm, "radius": 2 * mm});
            skCircle(sketch, "E4.29.5.0", {"center": v(358.66, -90.1) * mm, "radius": 2 * mm});
            skCircle(sketch, "E4.29.6.0", {"center": v(358.66, -106.1) * mm, "radius": 2 * mm});
            skCircle(sketch, "E4.29.7.0", {"center": v(358.66, -122.1) * mm, "radius": 2 * mm});
            skCircle(sketch, "E4.29.8.0", {"center": v(358.66, -138.1) * mm, "radius": 2 * mm});
            skCircle(sketch, "E4.29.9.0", {"center": v(358.66, -154.1) * mm, "radius": 2 * mm});
            skCircle(sketch, "E4.29.10.0", {"center": v(358.66, -170.1) * mm, "radius": 2 * mm});
            skCircle(sketch, "E4.29.11.0", {"center": v(358.66, -186.1) * mm, "radius": 2 * mm});
            skCircle(sketch, "E4.29.12.0", {"center": v(358.66, -202.1) * mm, "radius": 2 * mm});
            skCircle(sketch, "E4.29.13.0", {"center": v(358.66, -218.1) * mm, "radius": 2 * mm});
            skCircle(sketch, "E4.29.14.0", {"center": v(358.66, -234.1) * mm, "radius": 2 * mm});
            skCircle(sketch, "E4.29.15.0", {"center": v(358.66, -250.1) * mm, "radius": 2 * mm});
            skCircle(sketch, "E4.29.16.0", {"center": v(358.66, -266.1) * mm, "radius": 2 * mm});
            skCircle(sketch, "E4.29.17.0", {"center": v(358.66, -282.1) * mm, "radius": 2 * mm});
            skCircle(sketch, "E4.29.18.0", {"center": v(358.66, -298.1) * mm, "radius": 2 * mm});
            skCircle(sketch, "E4.29.19.0", {"center": v(358.66, -314.1) * mm, "radius": 2 * mm});
            skCircle(sketch, "E4.29.20.0", {"center": v(358.66, -330.1) * mm, "radius": 2 * mm});
            skCircle(sketch, "E4.29.21.0", {"center": v(358.66, -346.1) * mm, "radius": 2 * mm});
            skCircle(sketch, "E4.29.22.0", {"center": v(358.66, -362.1) * mm, "radius": 2 * mm});
            skCircle(sketch, "E4.29.23.0", {"center": v(358.66, -378.1) * mm, "radius": 2 * mm});
            skCircle(sketch, "E4.29.24.0", {"center": v(358.66, -394.1) * mm, "radius": 2 * mm});
            skCircle(sketch, "E4.29.25.0", {"center": v(358.66, -410.1) * mm, "radius": 2 * mm});
            skCircle(sketch, "E4.29.26.0", {"center": v(358.66, -426.1) * mm, "radius": 2 * mm});
            skCircle(sketch, "E4.29.27.0", {"center": v(358.66, -442.1) * mm, "radius": 2 * mm});
            skCircle(sketch, "E4.30.0.0", {"center": v(374.66, -10.1) * mm, "radius": 2 * mm});
            skCircle(sketch, "E4.30.1.0", {"center": v(374.66, -26.1) * mm, "radius": 2 * mm});
            skCircle(sketch, "E4.30.2.0", {"center": v(374.66, -42.1) * mm, "radius": 2 * mm});
            skCircle(sketch, "E4.30.3.0", {"center": v(374.66, -58.1) * mm, "radius": 2 * mm});
            skCircle(sketch, "E4.30.4.0", {"center": v(374.66, -74.1) * mm, "radius": 2 * mm});
            skCircle(sketch, "E4.30.5.0", {"center": v(374.66, -90.1) * mm, "radius": 2 * mm});
            skCircle(sketch, "E4.30.6.0", {"center": v(374.66, -106.1) * mm, "radius": 2 * mm});
            skCircle(sketch, "E4.30.7.0", {"center": v(374.66, -122.1) * mm, "radius": 2 * mm});
            skCircle(sketch, "E4.30.8.0", {"center": v(374.66, -138.1) * mm, "radius": 2 * mm});
            skCircle(sketch, "E4.30.9.0", {"center": v(374.66, -154.1) * mm, "radius": 2 * mm});
            skCircle(sketch, "E4.30.10.0", {"center": v(374.66, -170.1) * mm, "radius": 2 * mm});
            skCircle(sketch, "E4.30.11.0", {"center": v(374.66, -186.1) * mm, "radius": 2 * mm});
            skCircle(sketch, "E4.30.12.0", {"center": v(374.66, -202.1) * mm, "radius": 2 * mm});
            skCircle(sketch, "E4.30.13.0", {"center": v(374.66, -218.1) * mm, "radius": 2 * mm});
            skCircle(sketch, "E4.30.14.0", {"center": v(374.66, -234.1) * mm, "radius": 2 * mm});
            skCircle(sketch, "E4.30.15.0", {"center": v(374.66, -250.1) * mm, "radius": 2 * mm});
            skCircle(sketch, "E4.30.16.0", {"center": v(374.66, -266.1) * mm, "radius": 2 * mm});
            skCircle(sketch, "E4.30.17.0", {"center": v(374.66, -282.1) * mm, "radius": 2 * mm});
            skCircle(sketch, "E4.30.18.0", {"center": v(374.66, -298.1) * mm, "radius": 2 * mm});
            skCircle(sketch, "E4.30.19.0", {"center": v(374.66, -314.1) * mm, "radius": 2 * mm});
            skCircle(sketch, "E4.30.20.0", {"center": v(374.66, -330.1) * mm, "radius": 2 * mm});
            skCircle(sketch, "E4.30.21.0", {"center": v(374.66, -346.1) * mm, "radius": 2 * mm});
            skCircle(sketch, "E4.30.22.0", {"center": v(374.66, -362.1) * mm, "radius": 2 * mm});
            skCircle(sketch, "E4.30.23.0", {"center": v(374.66, -378.1) * mm, "radius": 2 * mm});
            skCircle(sketch, "E4.30.24.0", {"center": v(374.66, -394.1) * mm, "radius": 2 * mm});
            skCircle(sketch, "E4.30.25.0", {"center": v(374.66, -410.1) * mm, "radius": 2 * mm});
            skCircle(sketch, "E4.30.26.0", {"center": v(374.66, -426.1) * mm, "radius": 2 * mm});
            skCircle(sketch, "E4.30.27.0", {"center": v(374.66, -442.1) * mm, "radius": 2 * mm});
            skCircle(sketch, "E4.31.0.0", {"center": v(390.66, -10.1) * mm, "radius": 2 * mm});
            skCircle(sketch, "E4.31.1.0", {"center": v(390.66, -26.1) * mm, "radius": 2 * mm});
            skCircle(sketch, "E4.31.2.0", {"center": v(390.66, -42.1) * mm, "radius": 2 * mm});
            skCircle(sketch, "E4.31.3.0", {"center": v(390.66, -58.1) * mm, "radius": 2 * mm});
            skCircle(sketch, "E4.31.4.0", {"center": v(390.66, -74.1) * mm, "radius": 2 * mm});
            skCircle(sketch, "E4.31.5.0", {"center": v(390.66, -90.1) * mm, "radius": 2 * mm});
            skCircle(sketch, "E4.31.6.0", {"center": v(390.66, -106.1) * mm, "radius": 2 * mm});
            skCircle(sketch, "E4.31.7.0", {"center": v(390.66, -122.1) * mm, "radius": 2 * mm});
            skCircle(sketch, "E4.31.8.0", {"center": v(390.66, -138.1) * mm, "radius": 2 * mm});
            skCircle(sketch, "E4.31.9.0", {"center": v(390.66, -154.1) * mm, "radius": 2 * mm});
            skCircle(sketch, "E4.31.10.0", {"center": v(390.66, -170.1) * mm, "radius": 2 * mm});
            skCircle(sketch, "E4.31.11.0", {"center": v(390.66, -186.1) * mm, "radius": 2 * mm});
            skCircle(sketch, "E4.31.12.0", {"center": v(390.66, -202.1) * mm, "radius": 2 * mm});
            skCircle(sketch, "E4.31.13.0", {"center": v(390.66, -218.1) * mm, "radius": 2 * mm});
            skCircle(sketch, "E4.31.14.0", {"center": v(390.66, -234.1) * mm, "radius": 2 * mm});
            skCircle(sketch, "E4.31.15.0", {"center": v(390.66, -250.1) * mm, "radius": 2 * mm});
            skCircle(sketch, "E4.31.16.0", {"center": v(390.66, -266.1) * mm, "radius": 2 * mm});
            skCircle(sketch, "E4.31.17.0", {"center": v(390.66, -282.1) * mm, "radius": 2 * mm});
            skCircle(sketch, "E4.31.18.0", {"center": v(390.66, -298.1) * mm, "radius": 2 * mm});
            skCircle(sketch, "E4.31.19.0", {"center": v(390.66, -314.1) * mm, "radius": 2 * mm});
            skCircle(sketch, "E4.31.20.0", {"center": v(390.66, -330.1) * mm, "radius": 2 * mm});
            skCircle(sketch, "E4.31.21.0", {"center": v(390.66, -346.1) * mm, "radius": 2 * mm});
            skCircle(sketch, "E4.31.22.0", {"center": v(390.66, -362.1) * mm, "radius": 2 * mm});
            skCircle(sketch, "E4.31.23.0", {"center": v(390.66, -378.1) * mm, "radius": 2 * mm});
            skCircle(sketch, "E4.31.24.0", {"center": v(390.66, -394.1) * mm, "radius": 2 * mm});
            skCircle(sketch, "E4.31.25.0", {"center": v(390.66, -410.1) * mm, "radius": 2 * mm});
            skCircle(sketch, "E4.31.26.0", {"center": v(390.66, -426.1) * mm, "radius": 2 * mm});
            skCircle(sketch, "E4.31.27.0", {"center": v(390.66, -442.1) * mm, "radius": 2 * mm});
            skCircle(sketch, "E4.32.0.0", {"center": v(406.66, -10.1) * mm, "radius": 2 * mm});
            skCircle(sketch, "E4.32.1.0", {"center": v(406.66, -26.1) * mm, "radius": 2 * mm});
            skCircle(sketch, "E4.32.2.0", {"center": v(406.66, -42.1) * mm, "radius": 2 * mm});
            skCircle(sketch, "E4.32.3.0", {"center": v(406.66, -58.1) * mm, "radius": 2 * mm});
            skCircle(sketch, "E4.32.4.0", {"center": v(406.66, -74.1) * mm, "radius": 2 * mm});
            skCircle(sketch, "E4.32.5.0", {"center": v(406.66, -90.1) * mm, "radius": 2 * mm});
            skCircle(sketch, "E4.32.6.0", {"center": v(406.66, -106.1) * mm, "radius": 2 * mm});
            skCircle(sketch, "E4.32.7.0", {"center": v(406.66, -122.1) * mm, "radius": 2 * mm});
            skCircle(sketch, "E4.32.8.0", {"center": v(406.66, -138.1) * mm, "radius": 2 * mm});
            skCircle(sketch, "E4.32.9.0", {"center": v(406.66, -154.1) * mm, "radius": 2 * mm});
            skCircle(sketch, "E4.32.10.0", {"center": v(406.66, -170.1) * mm, "radius": 2 * mm});
            skCircle(sketch, "E4.32.11.0", {"center": v(406.66, -186.1) * mm, "radius": 2 * mm});
            skCircle(sketch, "E4.32.12.0", {"center": v(406.66, -202.1) * mm, "radius": 2 * mm});
            skCircle(sketch, "E4.32.13.0", {"center": v(406.66, -218.1) * mm, "radius": 2 * mm});
            skCircle(sketch, "E4.32.14.0", {"center": v(406.66, -234.1) * mm, "radius": 2 * mm});
            skCircle(sketch, "E4.32.15.0", {"center": v(406.66, -250.1) * mm, "radius": 2 * mm});
            skCircle(sketch, "E4.32.16.0", {"center": v(406.66, -266.1) * mm, "radius": 2 * mm});
            skCircle(sketch, "E4.32.17.0", {"center": v(406.66, -282.1) * mm, "radius": 2 * mm});
            skCircle(sketch, "E4.32.18.0", {"center": v(406.66, -298.1) * mm, "radius": 2 * mm});
            skCircle(sketch, "E4.32.19.0", {"center": v(406.66, -314.1) * mm, "radius": 2 * mm});
            skCircle(sketch, "E4.32.20.0", {"center": v(406.66, -330.1) * mm, "radius": 2 * mm});
            skCircle(sketch, "E4.32.21.0", {"center": v(406.66, -346.1) * mm, "radius": 2 * mm});
            skCircle(sketch, "E4.32.22.0", {"center": v(406.66, -362.1) * mm, "radius": 2 * mm});
            skCircle(sketch, "E4.32.23.0", {"center": v(406.66, -378.1) * mm, "radius": 2 * mm});
            skCircle(sketch, "E4.32.24.0", {"center": v(406.66, -394.1) * mm, "radius": 2 * mm});
            skCircle(sketch, "E4.32.25.0", {"center": v(406.66, -410.1) * mm, "radius": 2 * mm});
            skCircle(sketch, "E4.32.26.0", {"center": v(406.66, -426.1) * mm, "radius": 2 * mm});
            skCircle(sketch, "E4.32.27.0", {"center": v(406.66, -442.1) * mm, "radius": 2 * mm});
            skCircle(sketch, "E4.33.0.0", {"center": v(422.66, -10.1) * mm, "radius": 2 * mm});
            skCircle(sketch, "E4.33.1.0", {"center": v(422.66, -26.1) * mm, "radius": 2 * mm});
            skCircle(sketch, "E4.33.2.0", {"center": v(422.66, -42.1) * mm, "radius": 2 * mm});
            skCircle(sketch, "E4.33.3.0", {"center": v(422.66, -58.1) * mm, "radius": 2 * mm});
            skCircle(sketch, "E4.33.4.0", {"center": v(422.66, -74.1) * mm, "radius": 2 * mm});
            skCircle(sketch, "E4.33.5.0", {"center": v(422.66, -90.1) * mm, "radius": 2 * mm});
            skCircle(sketch, "E4.33.6.0", {"center": v(422.66, -106.1) * mm, "radius": 2 * mm});
            skCircle(sketch, "E4.33.7.0", {"center": v(422.66, -122.1) * mm, "radius": 2 * mm});
            skCircle(sketch, "E4.33.8.0", {"center": v(422.66, -138.1) * mm, "radius": 2 * mm});
            skCircle(sketch, "E4.33.9.0", {"center": v(422.66, -154.1) * mm, "radius": 2 * mm});
            skCircle(sketch, "E4.33.10.0", {"center": v(422.66, -170.1) * mm, "radius": 2 * mm});
            skCircle(sketch, "E4.33.11.0", {"center": v(422.66, -186.1) * mm, "radius": 2 * mm});
            skCircle(sketch, "E4.33.12.0", {"center": v(422.66, -202.1) * mm, "radius": 2 * mm});
            skCircle(sketch, "E4.33.13.0", {"center": v(422.66, -218.1) * mm, "radius": 2 * mm});
            skCircle(sketch, "E4.33.14.0", {"center": v(422.66, -234.1) * mm, "radius": 2 * mm});
            skCircle(sketch, "E4.33.15.0", {"center": v(422.66, -250.1) * mm, "radius": 2 * mm});
            skCircle(sketch, "E4.33.16.0", {"center": v(422.66, -266.1) * mm, "radius": 2 * mm});
            skCircle(sketch, "E4.33.17.0", {"center": v(422.66, -282.1) * mm, "radius": 2 * mm});
            skCircle(sketch, "E4.33.18.0", {"center": v(422.66, -298.1) * mm, "radius": 2 * mm});
            skCircle(sketch, "E4.33.19.0", {"center": v(422.66, -314.1) * mm, "radius": 2 * mm});
            skCircle(sketch, "E4.33.20.0", {"center": v(422.66, -330.1) * mm, "radius": 2 * mm});
            skCircle(sketch, "E4.33.21.0", {"center": v(422.66, -346.1) * mm, "radius": 2 * mm});
            skCircle(sketch, "E4.33.22.0", {"center": v(422.66, -362.1) * mm, "radius": 2 * mm});
            skCircle(sketch, "E4.33.23.0", {"center": v(422.66, -378.1) * mm, "radius": 2 * mm});
            skCircle(sketch, "E4.33.24.0", {"center": v(422.66, -394.1) * mm, "radius": 2 * mm});
            skCircle(sketch, "E4.33.25.0", {"center": v(422.66, -410.1) * mm, "radius": 2 * mm});
            skCircle(sketch, "E4.33.26.0", {"center": v(422.66, -426.1) * mm, "radius": 2 * mm});
            skCircle(sketch, "E4.33.27.0", {"center": v(422.66, -442.1) * mm, "radius": 2 * mm});
            skCircle(sketch, "E4.34.0.0", {"center": v(438.66, -10.1) * mm, "radius": 2 * mm});
            skCircle(sketch, "E4.34.1.0", {"center": v(438.66, -26.1) * mm, "radius": 2 * mm});
            skCircle(sketch, "E4.34.2.0", {"center": v(438.66, -42.1) * mm, "radius": 2 * mm});
            skCircle(sketch, "E4.34.3.0", {"center": v(438.66, -58.1) * mm, "radius": 2 * mm});
            skCircle(sketch, "E4.34.4.0", {"center": v(438.66, -74.1) * mm, "radius": 2 * mm});
            skCircle(sketch, "E4.34.5.0", {"center": v(438.66, -90.1) * mm, "radius": 2 * mm});
            skCircle(sketch, "E4.34.6.0", {"center": v(438.66, -106.1) * mm, "radius": 2 * mm});
            skCircle(sketch, "E4.34.7.0", {"center": v(438.66, -122.1) * mm, "radius": 2 * mm});
            skCircle(sketch, "E4.34.8.0", {"center": v(438.66, -138.1) * mm, "radius": 2 * mm});
            skCircle(sketch, "E4.34.9.0", {"center": v(438.66, -154.1) * mm, "radius": 2 * mm});
            skCircle(sketch, "E4.34.10.0", {"center": v(438.66, -170.1) * mm, "radius": 2 * mm});
            skCircle(sketch, "E4.34.11.0", {"center": v(438.66, -186.1) * mm, "radius": 2 * mm});
            skCircle(sketch, "E4.34.12.0", {"center": v(438.66, -202.1) * mm, "radius": 2 * mm});
            skCircle(sketch, "E4.34.13.0", {"center": v(438.66, -218.1) * mm, "radius": 2 * mm});
            skCircle(sketch, "E4.34.14.0", {"center": v(438.66, -234.1) * mm, "radius": 2 * mm});
            skCircle(sketch, "E4.34.15.0", {"center": v(438.66, -250.1) * mm, "radius": 2 * mm});
            skCircle(sketch, "E4.34.16.0", {"center": v(438.66, -266.1) * mm, "radius": 2 * mm});
            skCircle(sketch, "E4.34.17.0", {"center": v(438.66, -282.1) * mm, "radius": 2 * mm});
            skCircle(sketch, "E4.34.18.0", {"center": v(438.66, -298.1) * mm, "radius": 2 * mm});
            skCircle(sketch, "E4.34.19.0", {"center": v(438.66, -314.1) * mm, "radius": 2 * mm});
            skCircle(sketch, "E4.34.20.0", {"center": v(438.66, -330.1) * mm, "radius": 2 * mm});
            skCircle(sketch, "E4.34.21.0", {"center": v(438.66, -346.1) * mm, "radius": 2 * mm});
            skCircle(sketch, "E4.34.22.0", {"center": v(438.66, -362.1) * mm, "radius": 2 * mm});
            skCircle(sketch, "E4.34.23.0", {"center": v(438.66, -378.1) * mm, "radius": 2 * mm});
            skCircle(sketch, "E4.34.24.0", {"center": v(438.66, -394.1) * mm, "radius": 2 * mm});
            skCircle(sketch, "E4.34.25.0", {"center": v(438.66, -410.1) * mm, "radius": 2 * mm});
            skCircle(sketch, "E4.34.26.0", {"center": v(438.66, -426.1) * mm, "radius": 2 * mm});
            skCircle(sketch, "E4.34.27.0", {"center": v(438.66, -442.1) * mm, "radius": 2 * mm});
            skCircle(sketch, "E4.35.0.0", {"center": v(454.66, -10.1) * mm, "radius": 2 * mm});
            skCircle(sketch, "E4.35.1.0", {"center": v(454.66, -26.1) * mm, "radius": 2 * mm});
            skCircle(sketch, "E4.35.2.0", {"center": v(454.66, -42.1) * mm, "radius": 2 * mm});
            skCircle(sketch, "E4.35.3.0", {"center": v(454.66, -58.1) * mm, "radius": 2 * mm});
            skCircle(sketch, "E4.35.4.0", {"center": v(454.66, -74.1) * mm, "radius": 2 * mm});
            skCircle(sketch, "E4.35.5.0", {"center": v(454.66, -90.1) * mm, "radius": 2 * mm});
            skCircle(sketch, "E4.35.6.0", {"center": v(454.66, -106.1) * mm, "radius": 2 * mm});
            skCircle(sketch, "E4.35.7.0", {"center": v(454.66, -122.1) * mm, "radius": 2 * mm});
            skCircle(sketch, "E4.35.8.0", {"center": v(454.66, -138.1) * mm, "radius": 2 * mm});
            skCircle(sketch, "E4.35.9.0", {"center": v(454.66, -154.1) * mm, "radius": 2 * mm});
            skCircle(sketch, "E4.35.10.0", {"center": v(454.66, -170.1) * mm, "radius": 2 * mm});
            skCircle(sketch, "E4.35.11.0", {"center": v(454.66, -186.1) * mm, "radius": 2 * mm});
            skCircle(sketch, "E4.35.12.0", {"center": v(454.66, -202.1) * mm, "radius": 2 * mm});
            skCircle(sketch, "E4.35.13.0", {"center": v(454.66, -218.1) * mm, "radius": 2 * mm});
            skCircle(sketch, "E4.35.14.0", {"center": v(454.66, -234.1) * mm, "radius": 2 * mm});
            skCircle(sketch, "E4.35.15.0", {"center": v(454.66, -250.1) * mm, "radius": 2 * mm});
            skCircle(sketch, "E4.35.16.0", {"center": v(454.66, -266.1) * mm, "radius": 2 * mm});
            skCircle(sketch, "E4.35.17.0", {"center": v(454.66, -282.1) * mm, "radius": 2 * mm});
            skCircle(sketch, "E4.35.18.0", {"center": v(454.66, -298.1) * mm, "radius": 2 * mm});
            skCircle(sketch, "E4.35.19.0", {"center": v(454.66, -314.1) * mm, "radius": 2 * mm});
            skCircle(sketch, "E4.35.20.0", {"center": v(454.66, -330.1) * mm, "radius": 2 * mm});
            skCircle(sketch, "E4.35.21.0", {"center": v(454.66, -346.1) * mm, "radius": 2 * mm});
            skCircle(sketch, "E4.35.22.0", {"center": v(454.66, -362.1) * mm, "radius": 2 * mm});
            skCircle(sketch, "E4.35.23.0", {"center": v(454.66, -378.1) * mm, "radius": 2 * mm});
            skCircle(sketch, "E4.35.24.0", {"center": v(454.66, -394.1) * mm, "radius": 2 * mm});
            skCircle(sketch, "E4.35.25.0", {"center": v(454.66, -410.1) * mm, "radius": 2 * mm});
            skCircle(sketch, "E4.35.26.0", {"center": v(454.66, -426.1) * mm, "radius": 2 * mm});
            skCircle(sketch, "E4.35.27.0", {"center": v(454.66, -442.1) * mm, "radius": 2 * mm});
            skCircle(sketch, "E4.36.0.0", {"center": v(470.66, -10.1) * mm, "radius": 2 * mm});
            skCircle(sketch, "E4.36.1.0", {"center": v(470.66, -26.1) * mm, "radius": 2 * mm});
            skCircle(sketch, "E4.36.2.0", {"center": v(470.66, -42.1) * mm, "radius": 2 * mm});
            skCircle(sketch, "E4.36.3.0", {"center": v(470.66, -58.1) * mm, "radius": 2 * mm});
            skCircle(sketch, "E4.36.4.0", {"center": v(470.66, -74.1) * mm, "radius": 2 * mm});
            skCircle(sketch, "E4.36.5.0", {"center": v(470.66, -90.1) * mm, "radius": 2 * mm});
            skCircle(sketch, "E4.36.6.0", {"center": v(470.66, -106.1) * mm, "radius": 2 * mm});
            skCircle(sketch, "E4.36.7.0", {"center": v(470.66, -122.1) * mm, "radius": 2 * mm});
            skCircle(sketch, "E4.36.8.0", {"center": v(470.66, -138.1) * mm, "radius": 2 * mm});
            skCircle(sketch, "E4.36.9.0", {"center": v(470.66, -154.1) * mm, "radius": 2 * mm});
            skCircle(sketch, "E4.36.10.0", {"center": v(470.66, -170.1) * mm, "radius": 2 * mm});
            skCircle(sketch, "E4.36.11.0", {"center": v(470.66, -186.1) * mm, "radius": 2 * mm});
            skCircle(sketch, "E4.36.12.0", {"center": v(470.66, -202.1) * mm, "radius": 2 * mm});
            skCircle(sketch, "E4.36.13.0", {"center": v(470.66, -218.1) * mm, "radius": 2 * mm});
            skCircle(sketch, "E4.36.14.0", {"center": v(470.66, -234.1) * mm, "radius": 2 * mm});
            skCircle(sketch, "E4.36.15.0", {"center": v(470.66, -250.1) * mm, "radius": 2 * mm});
            skCircle(sketch, "E4.36.16.0", {"center": v(470.66, -266.1) * mm, "radius": 2 * mm});
            skCircle(sketch, "E4.36.17.0", {"center": v(470.66, -282.1) * mm, "radius": 2 * mm});
            skCircle(sketch, "E4.36.18.0", {"center": v(470.66, -298.1) * mm, "radius": 2 * mm});
            skCircle(sketch, "E4.36.19.0", {"center": v(470.66, -314.1) * mm, "radius": 2 * mm});
            skCircle(sketch, "E4.36.20.0", {"center": v(470.66, -330.1) * mm, "radius": 2 * mm});
            skCircle(sketch, "E4.36.21.0", {"center": v(470.66, -346.1) * mm, "radius": 2 * mm});
            skCircle(sketch, "E4.36.22.0", {"center": v(470.66, -362.1) * mm, "radius": 2 * mm});
            skCircle(sketch, "E4.36.23.0", {"center": v(470.66, -378.1) * mm, "radius": 2 * mm});
            skCircle(sketch, "E4.36.24.0", {"center": v(470.66, -394.1) * mm, "radius": 2 * mm});
            skCircle(sketch, "E4.36.25.0", {"center": v(470.66, -410.1) * mm, "radius": 2 * mm});
            skCircle(sketch, "E4.36.26.0", {"center": v(470.66, -426.1) * mm, "radius": 2 * mm});
            skCircle(sketch, "E4.36.27.0", {"center": v(470.66, -442.1) * mm, "radius": 2 * mm});
            skCircle(sketch, "E4.37.0.0", {"center": v(486.66, -10.1) * mm, "radius": 2 * mm});
            skCircle(sketch, "E4.37.1.0", {"center": v(486.66, -26.1) * mm, "radius": 2 * mm});
            skCircle(sketch, "E4.37.2.0", {"center": v(486.66, -42.1) * mm, "radius": 2 * mm});
            skCircle(sketch, "E4.37.3.0", {"center": v(486.66, -58.1) * mm, "radius": 2 * mm});
            skCircle(sketch, "E4.37.4.0", {"center": v(486.66, -74.1) * mm, "radius": 2 * mm});
            skCircle(sketch, "E4.37.5.0", {"center": v(486.66, -90.1) * mm, "radius": 2 * mm});
            skCircle(sketch, "E4.37.6.0", {"center": v(486.66, -106.1) * mm, "radius": 2 * mm});
            skCircle(sketch, "E4.37.7.0", {"center": v(486.66, -122.1) * mm, "radius": 2 * mm});
            skCircle(sketch, "E4.37.8.0", {"center": v(486.66, -138.1) * mm, "radius": 2 * mm});
            skCircle(sketch, "E4.37.9.0", {"center": v(486.66, -154.1) * mm, "radius": 2 * mm});
            skCircle(sketch, "E4.37.10.0", {"center": v(486.66, -170.1) * mm, "radius": 2 * mm});
            skCircle(sketch, "E4.37.11.0", {"center": v(486.66, -186.1) * mm, "radius": 2 * mm});
            skCircle(sketch, "E4.37.12.0", {"center": v(486.66, -202.1) * mm, "radius": 2 * mm});
            skCircle(sketch, "E4.37.13.0", {"center": v(486.66, -218.1) * mm, "radius": 2 * mm});
            skCircle(sketch, "E4.37.14.0", {"center": v(486.66, -234.1) * mm, "radius": 2 * mm});
            skCircle(sketch, "E4.37.15.0", {"center": v(486.66, -250.1) * mm, "radius": 2 * mm});
            skCircle(sketch, "E4.37.16.0", {"center": v(486.66, -266.1) * mm, "radius": 2 * mm});
            skCircle(sketch, "E4.37.17.0", {"center": v(486.66, -282.1) * mm, "radius": 2 * mm});
            skCircle(sketch, "E4.37.18.0", {"center": v(486.66, -298.1) * mm, "radius": 2 * mm});
            skCircle(sketch, "E4.37.19.0", {"center": v(486.66, -314.1) * mm, "radius": 2 * mm});
            skCircle(sketch, "E4.37.20.0", {"center": v(486.66, -330.1) * mm, "radius": 2 * mm});
            skCircle(sketch, "E4.37.21.0", {"center": v(486.66, -346.1) * mm, "radius": 2 * mm});
            skCircle(sketch, "E4.37.22.0", {"center": v(486.66, -362.1) * mm, "radius": 2 * mm});
            skCircle(sketch, "E4.37.23.0", {"center": v(486.66, -378.1) * mm, "radius": 2 * mm});
            skCircle(sketch, "E4.37.24.0", {"center": v(486.66, -394.1) * mm, "radius": 2 * mm});
            skCircle(sketch, "E4.37.25.0", {"center": v(486.66, -410.1) * mm, "radius": 2 * mm});
            skCircle(sketch, "E4.37.26.0", {"center": v(486.66, -426.1) * mm, "radius": 2 * mm});
            skCircle(sketch, "E4.37.27.0", {"center": v(486.66, -442.1) * mm, "radius": 2 * mm});
            skCircle(sketch, "E4.38.0.0", {"center": v(502.66, -10.1) * mm, "radius": 2 * mm});
            skCircle(sketch, "E4.38.1.0", {"center": v(502.66, -26.1) * mm, "radius": 2 * mm});
            skCircle(sketch, "E4.38.2.0", {"center": v(502.66, -42.1) * mm, "radius": 2 * mm});
            skCircle(sketch, "E4.38.3.0", {"center": v(502.66, -58.1) * mm, "radius": 2 * mm});
            skCircle(sketch, "E4.38.4.0", {"center": v(502.66, -74.1) * mm, "radius": 2 * mm});
            skCircle(sketch, "E4.38.5.0", {"center": v(502.66, -90.1) * mm, "radius": 2 * mm});
            skCircle(sketch, "E4.38.6.0", {"center": v(502.66, -106.1) * mm, "radius": 2 * mm});
            skCircle(sketch, "E4.38.7.0", {"center": v(502.66, -122.1) * mm, "radius": 2 * mm});
            skCircle(sketch, "E4.38.8.0", {"center": v(502.66, -138.1) * mm, "radius": 2 * mm});
            skCircle(sketch, "E4.38.9.0", {"center": v(502.66, -154.1) * mm, "radius": 2 * mm});
            skCircle(sketch, "E4.38.10.0", {"center": v(502.66, -170.1) * mm, "radius": 2 * mm});
            skCircle(sketch, "E4.38.11.0", {"center": v(502.66, -186.1) * mm, "radius": 2 * mm});
            skCircle(sketch, "E4.38.12.0", {"center": v(502.66, -202.1) * mm, "radius": 2 * mm});
            skCircle(sketch, "E4.38.13.0", {"center": v(502.66, -218.1) * mm, "radius": 2 * mm});
            skCircle(sketch, "E4.38.14.0", {"center": v(502.66, -234.1) * mm, "radius": 2 * mm});
            skCircle(sketch, "E4.38.15.0", {"center": v(502.66, -250.1) * mm, "radius": 2 * mm});
            skCircle(sketch, "E4.38.16.0", {"center": v(502.66, -266.1) * mm, "radius": 2 * mm});
            skCircle(sketch, "E4.38.17.0", {"center": v(502.66, -282.1) * mm, "radius": 2 * mm});
            skCircle(sketch, "E4.38.18.0", {"center": v(502.66, -298.1) * mm, "radius": 2 * mm});
            skCircle(sketch, "E4.38.19.0", {"center": v(502.66, -314.1) * mm, "radius": 2 * mm});
            skCircle(sketch, "E4.38.20.0", {"center": v(502.66, -330.1) * mm, "radius": 2 * mm});
            skCircle(sketch, "E4.38.21.0", {"center": v(502.66, -346.1) * mm, "radius": 2 * mm});
            skCircle(sketch, "E4.38.22.0", {"center": v(502.66, -362.1) * mm, "radius": 2 * mm});
            skCircle(sketch, "E4.38.23.0", {"center": v(502.66, -378.1) * mm, "radius": 2 * mm});
            skCircle(sketch, "E4.38.24.0", {"center": v(502.66, -394.1) * mm, "radius": 2 * mm});
            skCircle(sketch, "E4.38.25.0", {"center": v(502.66, -410.1) * mm, "radius": 2 * mm});
            skCircle(sketch, "E4.38.26.0", {"center": v(502.66, -426.1) * mm, "radius": 2 * mm});
            skCircle(sketch, "E4.38.27.0", {"center": v(502.66, -442.1) * mm, "radius": 2 * mm});
            skCircle(sketch, "E4.39.0.0", {"center": v(518.66, -10.1) * mm, "radius": 2 * mm});
            skCircle(sketch, "E4.39.1.0", {"center": v(518.66, -26.1) * mm, "radius": 2 * mm});
            skCircle(sketch, "E4.39.2.0", {"center": v(518.66, -42.1) * mm, "radius": 2 * mm});
            skCircle(sketch, "E4.39.3.0", {"center": v(518.66, -58.1) * mm, "radius": 2 * mm});
            skCircle(sketch, "E4.39.4.0", {"center": v(518.66, -74.1) * mm, "radius": 2 * mm});
            skCircle(sketch, "E4.39.5.0", {"center": v(518.66, -90.1) * mm, "radius": 2 * mm});
            skCircle(sketch, "E4.39.6.0", {"center": v(518.66, -106.1) * mm, "radius": 2 * mm});
            skCircle(sketch, "E4.39.7.0", {"center": v(518.66, -122.1) * mm, "radius": 2 * mm});
            skCircle(sketch, "E4.39.8.0", {"center": v(518.66, -138.1) * mm, "radius": 2 * mm});
            skCircle(sketch, "E4.39.9.0", {"center": v(518.66, -154.1) * mm, "radius": 2 * mm});
            skCircle(sketch, "E4.39.10.0", {"center": v(518.66, -170.1) * mm, "radius": 2 * mm});
            skCircle(sketch, "E4.39.11.0", {"center": v(518.66, -186.1) * mm, "radius": 2 * mm});
            skCircle(sketch, "E4.39.12.0", {"center": v(518.66, -202.1) * mm, "radius": 2 * mm});
            skCircle(sketch, "E4.39.13.0", {"center": v(518.66, -218.1) * mm, "radius": 2 * mm});
            skCircle(sketch, "E4.39.14.0", {"center": v(518.66, -234.1) * mm, "radius": 2 * mm});
            skCircle(sketch, "E4.39.15.0", {"center": v(518.66, -250.1) * mm, "radius": 2 * mm});
            skCircle(sketch, "E4.39.16.0", {"center": v(518.66, -266.1) * mm, "radius": 2 * mm});
            skCircle(sketch, "E4.39.17.0", {"center": v(518.66, -282.1) * mm, "radius": 2 * mm});
            skCircle(sketch, "E4.39.18.0", {"center": v(518.66, -298.1) * mm, "radius": 2 * mm});
            skCircle(sketch, "E4.39.19.0", {"center": v(518.66, -314.1) * mm, "radius": 2 * mm});
            skCircle(sketch, "E4.39.20.0", {"center": v(518.66, -330.1) * mm, "radius": 2 * mm});
            skCircle(sketch, "E4.39.21.0", {"center": v(518.66, -346.1) * mm, "radius": 2 * mm});
            skCircle(sketch, "E4.39.22.0", {"center": v(518.66, -362.1) * mm, "radius": 2 * mm});
            skCircle(sketch, "E4.39.23.0", {"center": v(518.66, -378.1) * mm, "radius": 2 * mm});
            skCircle(sketch, "E4.39.24.0", {"center": v(518.66, -394.1) * mm, "radius": 2 * mm});
            skCircle(sketch, "E4.39.25.0", {"center": v(518.66, -410.1) * mm, "radius": 2 * mm});
            skCircle(sketch, "E4.39.26.0", {"center": v(518.66, -426.1) * mm, "radius": 2 * mm});
            skCircle(sketch, "E4.39.27.0", {"center": v(518.66, -442.1) * mm, "radius": 2 * mm});
            skLineSegment(sketch, "E4.direction1", {"start": v(-105.34, -10.1) * mm, "end": v(-89.34, -10.1) * mm, "construction": true});
            skLineSegment(sketch, "E4.direction2", {"start": v(-105.34, -10.1) * mm, "end": v(-105.34, -26.1) * mm, "construction": true});
            skSolve(sketch);
        }
        {
            var Q0;
            Q0=makeQuery(id+"F0.imprint","IMPRINT",FACE,{"disambiguationData":[TD([[makeQuery(id+"F0.imprint","IMPRINT",EDGE,{"derivedFrom":sQuery(id+"F0.wireOp",EDGE,"E0.bottom")}),-1.0]])]});
            extrude(context, id + "F1", {"entities" : qUnion([Q0]), "depth" : 1 * mm, "offsetDistance" : 25 * mm});
        }
    });
